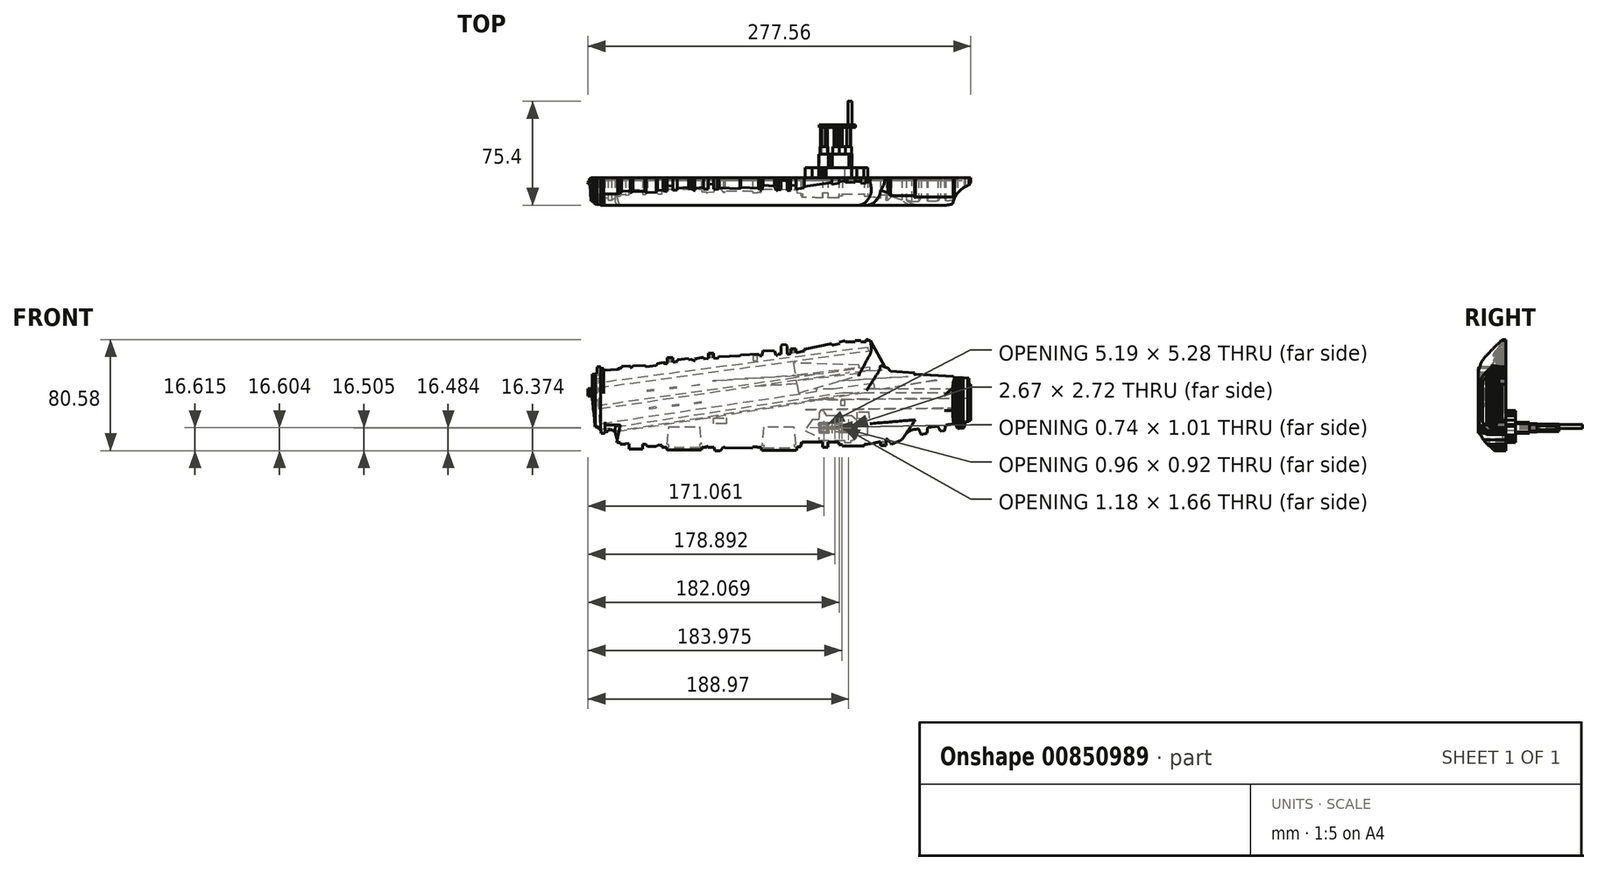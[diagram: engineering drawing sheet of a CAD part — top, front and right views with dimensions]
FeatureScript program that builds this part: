
annotation { "Feature Type Name" : "Feature", "Feature Type Description" : "" }
export const myFeature = defineFeature(function(context is Context, id is Id, definition is map)
    precondition{}
    {
        {
            var Q0;
            Q0=qCreatedBy(makeId("Front.planeOp"),FACE);
            var sketch = newSketch(context, id + "F0", { "sketchPlane" : qUnion([Q0])});
            skLineSegment(sketch, "E0", {"start": v(17.46, 94.58) * mm, "end": v(17.46, 84.08) * mm});
            skLineSegment(sketch, "E1", {"start": v(17.46, 84.08) * mm, "end": v(13.14, 84.08) * mm});
            skLineSegment(sketch, "E2", {"start": v(13.14, 84.08) * mm, "end": v(13.14, 78.8) * mm});
            skLineSegment(sketch, "E3", {"start": v(13.14, 78.8) * mm, "end": v(17.46, 78.8) * mm});
            skLineSegment(sketch, "E4", {"start": v(17.46, 78.8) * mm, "end": v(19.56, 56.5) * mm});
            skLineSegment(sketch, "E5", {"start": v(19.56, 56.5) * mm, "end": v(20.5, 56.3) * mm});
            skLineSegment(sketch, "E6", {"start": v(20.5, 56.3) * mm, "end": v(21.21, 56.3) * mm});
            skLineSegment(sketch, "E7", {"start": v(21.21, 56.3) * mm, "end": v(21.83, 57.14) * mm});
            skLineSegment(sketch, "E8", {"start": v(21.83, 57.14) * mm, "end": v(22.25, 54.43) * mm});
            skLineSegment(sketch, "E9", {"start": v(22.25, 54.43) * mm, "end": v(23.35, 54.6) * mm});
            skLineSegment(sketch, "E10", {"start": v(23.35, 54.6) * mm, "end": v(24.02, 54.26) * mm});
            skLineSegment(sketch, "E11", {"start": v(24.02, 54.26) * mm, "end": v(23.94, 51.57) * mm});
            skLineSegment(sketch, "E12", {"start": v(23.94, 51.57) * mm, "end": v(26.88, 51.57) * mm});
            skLineSegment(sketch, "E13", {"start": v(26.88, 51.57) * mm, "end": v(26.88, 53) * mm});
            skLineSegment(sketch, "E14", {"start": v(26.88, 53) * mm, "end": v(28.92, 53) * mm});
            skLineSegment(sketch, "E15", {"start": v(28.92, 53) * mm, "end": v(28.92, 54.15) * mm});
            skLineSegment(sketch, "E16", {"start": v(28.92, 54.15) * mm, "end": v(31.63, 54.21) * mm});
            skLineSegment(sketch, "E17", {"start": v(31.63, 54.21) * mm, "end": v(33.97, 52.9) * mm});
            skLineSegment(sketch, "E18", {"start": v(33.97, 52.9) * mm, "end": v(35.66, 46.84) * mm});
            skLineSegment(sketch, "E19", {"start": v(35.66, 46.84) * mm, "end": v(35.29, 45.02) * mm});
            skLineSegment(sketch, "E20", {"start": v(35.29, 45.02) * mm, "end": v(37.83, 45.02) * mm});
            skLineSegment(sketch, "E21", {"start": v(37.83, 45.02) * mm, "end": v(37.83, 43.82) * mm});
            skLineSegment(sketch, "E22", {"start": v(37.83, 43.82) * mm, "end": v(41.81, 43.7) * mm});
            skLineSegment(sketch, "E23", {"start": v(41.81, 43.7) * mm, "end": v(41.81, 44.43) * mm});
            skLineSegment(sketch, "E24", {"start": v(41.81, 44.43) * mm, "end": v(44.33, 44.18) * mm});
            skLineSegment(sketch, "E25", {"start": v(44.33, 44.18) * mm, "end": v(44.33, 40.16) * mm});
            skLineSegment(sketch, "E26", {"start": v(44.33, 40.16) * mm, "end": v(54.24, 40.16) * mm});
            skLineSegment(sketch, "E27", {"start": v(54.24, 40.16) * mm, "end": v(54.24, 43.75) * mm});
            skLineSegment(sketch, "E28", {"start": v(54.24, 43.75) * mm, "end": v(56.4, 43.75) * mm});
            skLineSegment(sketch, "E29", {"start": v(56.4, 43.75) * mm, "end": v(57.47, 42.08) * mm});
            skLineSegment(sketch, "E30", {"start": v(57.47, 42.08) * mm, "end": v(63.78, 42.08) * mm});
            skLineSegment(sketch, "E31", {"start": v(63.78, 42.08) * mm, "end": v(65.22, 43.15) * mm});
            skLineSegment(sketch, "E32", {"start": v(65.22, 43.15) * mm, "end": v(68.07, 43.15) * mm});
            skLineSegment(sketch, "E33", {"start": v(68.07, 43.15) * mm, "end": v(68.07, 41.42) * mm});
            skLineSegment(sketch, "E34", {"start": v(68.07, 41.42) * mm, "end": v(71.42, 41.42) * mm});
            skLineSegment(sketch, "E35", {"start": v(71.42, 41.42) * mm, "end": v(71.42, 39.98) * mm});
            skLineSegment(sketch, "E36", {"start": v(71.42, 39.98) * mm, "end": v(71.88, 39.65) * mm});
            skLineSegment(sketch, "E37", {"start": v(71.88, 39.65) * mm, "end": v(96.66, 39.72) * mm});
            skLineSegment(sketch, "E38", {"start": v(96.66, 39.72) * mm, "end": v(97.06, 40.28) * mm});
            skLineSegment(sketch, "E39", {"start": v(97.06, 40.28) * mm, "end": v(97.08, 41.63) * mm});
            skLineSegment(sketch, "E40", {"start": v(97.08, 41.63) * mm, "end": v(100.58, 41.58) * mm});
            skLineSegment(sketch, "E41", {"start": v(100.58, 41.58) * mm, "end": v(100.58, 42.76) * mm});
            skLineSegment(sketch, "E42", {"start": v(100.58, 42.76) * mm, "end": v(101.48, 41.63) * mm});
            skLineSegment(sketch, "E43", {"start": v(101.48, 41.63) * mm, "end": v(105.9, 41.55) * mm});
            skLineSegment(sketch, "E44", {"start": v(105.9, 41.55) * mm, "end": v(106.63, 39.13) * mm});
            skLineSegment(sketch, "E45", {"start": v(106.63, 39.13) * mm, "end": v(110.3, 39.13) * mm});
            skLineSegment(sketch, "E46", {"start": v(110.3, 39.13) * mm, "end": v(112.43, 41.6) * mm});
            skLineSegment(sketch, "E47", {"start": v(112.43, 41.6) * mm, "end": v(113.7, 41.6) * mm});
            skLineSegment(sketch, "E48", {"start": v(113.7, 41.6) * mm, "end": v(113.7, 41.14) * mm});
            skLineSegment(sketch, "E49", {"start": v(113.7, 41.14) * mm, "end": v(133.88, 41) * mm});
            skLineSegment(sketch, "E50", {"start": v(133.88, 41) * mm, "end": v(133.88, 41.77) * mm});
            skLineSegment(sketch, "E51", {"start": v(133.88, 41.77) * mm, "end": v(137.37, 41.75) * mm});
            skLineSegment(sketch, "E52", {"start": v(137.37, 41.75) * mm, "end": v(137.37, 41.45) * mm});
            skLineSegment(sketch, "E53", {"start": v(137.37, 41.45) * mm, "end": v(140.1, 41.43) * mm});
            skLineSegment(sketch, "E54", {"start": v(140.1, 41.43) * mm, "end": v(140.1, 39.91) * mm});
            skLineSegment(sketch, "E55", {"start": v(140.1, 39.91) * mm, "end": v(140.58, 39.34) * mm});
            skLineSegment(sketch, "E56", {"start": v(140.58, 39.34) * mm, "end": v(165.42, 39.34) * mm});
            skLineSegment(sketch, "E57", {"start": v(165.42, 39.34) * mm, "end": v(165.96, 39.92) * mm});
            skLineSegment(sketch, "E58", {"start": v(165.96, 39.92) * mm, "end": v(165.96, 41.75) * mm});
            skLineSegment(sketch, "E59", {"start": v(165.96, 41.75) * mm, "end": v(168.85, 41.9) * mm});
            skLineSegment(sketch, "E60", {"start": v(168.85, 41.9) * mm, "end": v(168.86, 43.4) * mm});
            skLineSegment(sketch, "E61", {"start": v(168.86, 43.4) * mm, "end": v(169.92, 45.23) * mm});
            skLineSegment(sketch, "E62", {"start": v(169.92, 45.23) * mm, "end": v(184.45, 45.23) * mm});
            skLineSegment(sketch, "E63", {"start": v(184.45, 45.23) * mm, "end": v(184.45, 41.6) * mm});
            skLineSegment(sketch, "E64", {"start": v(184.45, 41.6) * mm, "end": v(188.37, 41.56) * mm});
            skLineSegment(sketch, "E65", {"start": v(188.37, 41.56) * mm, "end": v(188.37, 45.38) * mm});
            skLineSegment(sketch, "E66", {"start": v(188.37, 45.38) * mm, "end": v(196.36, 45.38) * mm});
            skLineSegment(sketch, "E67", {"start": v(196.36, 45.38) * mm, "end": v(196.36, 43.58) * mm});
            skLineSegment(sketch, "E68", {"start": v(196.36, 43.58) * mm, "end": v(198.74, 43.56) * mm});
            skLineSegment(sketch, "E69", {"start": v(198.74, 43.56) * mm, "end": v(198.74, 42.38) * mm});
            skLineSegment(sketch, "E70", {"start": v(198.74, 42.38) * mm, "end": v(214.9, 42.38) * mm});
            skLineSegment(sketch, "E71", {"start": v(214.9, 42.38) * mm, "end": v(214.9, 43.75) * mm});
            skLineSegment(sketch, "E72", {"start": v(214.9, 43.75) * mm, "end": v(217.35, 43.73) * mm});
            skLineSegment(sketch, "E73", {"start": v(217.35, 43.73) * mm, "end": v(226.5, 45.59) * mm});
            skLineSegment(sketch, "E74", {"start": v(226.5, 45.59) * mm, "end": v(226.5, 42.93) * mm});
            skLineSegment(sketch, "E75", {"start": v(226.5, 42.93) * mm, "end": v(230.55, 42.93) * mm});
            skLineSegment(sketch, "E76", {"start": v(230.55, 42.93) * mm, "end": v(230.58, 47.27) * mm});
            skLineSegment(sketch, "E77", {"start": v(230.58, 47.27) * mm, "end": v(231.4, 47.6) * mm});
            skLineSegment(sketch, "E78", {"start": v(231.4, 47.6) * mm, "end": v(234.35, 43.8) * mm});
            skLineSegment(sketch, "E79", {"start": v(234.35, 43.8) * mm, "end": v(242.01, 46.9) * mm});
            skLineSegment(sketch, "E80", {"start": v(242.01, 46.9) * mm, "end": v(246.7, 53.94) * mm});
            skLineSegment(sketch, "E81", {"start": v(246.7, 53.94) * mm, "end": v(254.19, 54.94) * mm});
            skLineSegment(sketch, "E82", {"start": v(254.19, 54.94) * mm, "end": v(255.88, 50.81) * mm});
            skLineSegment(sketch, "E83", {"start": v(255.88, 50.81) * mm, "end": v(260.17, 51.58) * mm});
            skLineSegment(sketch, "E84", {"start": v(260.17, 51.58) * mm, "end": v(260.74, 56.02) * mm});
            skLineSegment(sketch, "E85", {"start": v(260.74, 56.02) * mm, "end": v(268.11, 56.83) * mm});
            skLineSegment(sketch, "E86", {"start": v(268.11, 56.83) * mm, "end": v(270.04, 53.3) * mm});
            skLineSegment(sketch, "E87", {"start": v(270.04, 53.3) * mm, "end": v(273, 53.67) * mm});
            skLineSegment(sketch, "E88", {"start": v(273, 53.67) * mm, "end": v(273.81, 57.7) * mm});
            skLineSegment(sketch, "E89", {"start": v(273.81, 57.7) * mm, "end": v(280.9, 58.7) * mm});
            skLineSegment(sketch, "E90", {"start": v(280.9, 58.7) * mm, "end": v(282.36, 55.14) * mm});
            skLineSegment(sketch, "E91", {"start": v(282.36, 55.14) * mm, "end": v(287.02, 55.7) * mm});
            skLineSegment(sketch, "E92", {"start": v(287.02, 55.7) * mm, "end": v(288, 59.97) * mm});
            skLineSegment(sketch, "E93", {"start": v(288, 59.97) * mm, "end": v(290.72, 60.26) * mm});
            skLineSegment(sketch, "E94", {"start": v(290.72, 60.26) * mm, "end": v(290.9, 60.95) * mm});
            skLineSegment(sketch, "E95", {"start": v(290.9, 60.95) * mm, "end": v(292, 60.94) * mm});
            skLineSegment(sketch, "E96", {"start": v(292, 60.94) * mm, "end": v(292, 87.32) * mm});
            skLineSegment(sketch, "E97", {"start": v(292, 87.32) * mm, "end": v(290.78, 87.33) * mm});
            skLineSegment(sketch, "E98", {"start": v(290.78, 87.33) * mm, "end": v(290.72, 91.74) * mm});
            skLineSegment(sketch, "E99", {"start": v(290.72, 91.74) * mm, "end": v(280.06, 92.14) * mm});
            skLineSegment(sketch, "E100", {"start": v(280.06, 92.14) * mm, "end": v(279.08, 92.88) * mm});
            skLineSegment(sketch, "E101", {"start": v(279.08, 92.88) * mm, "end": v(251.91, 94.68) * mm});
            skLineSegment(sketch, "E102", {"start": v(251.91, 94.68) * mm, "end": v(251.55, 94.22) * mm});
            skLineSegment(sketch, "E103", {"start": v(251.55, 94.22) * mm, "end": v(251.28, 94.44) * mm});
            skLineSegment(sketch, "E104", {"start": v(251.28, 94.44) * mm, "end": v(251.28, 95.53) * mm});
            skLineSegment(sketch, "E105", {"start": v(251.28, 95.53) * mm, "end": v(233.78, 96.7) * mm});
            skLineSegment(sketch, "E106", {"start": v(233.78, 96.7) * mm, "end": v(231.76, 99.17) * mm});
            skLineSegment(sketch, "E107", {"start": v(231.76, 99.17) * mm, "end": v(229.8, 99.83) * mm});
            skLineSegment(sketch, "E108", {"start": v(229.8, 99.83) * mm, "end": v(219.13, 119.12) * mm});
            skLineSegment(sketch, "E109", {"start": v(219.13, 119.12) * mm, "end": v(218.1, 118.56) * mm});
            skLineSegment(sketch, "E110", {"start": v(218.1, 118.56) * mm, "end": v(217.47, 119.7) * mm});
            skLineSegment(sketch, "E111", {"start": v(217.47, 119.7) * mm, "end": v(216.05, 119.7) * mm});
            skLineSegment(sketch, "E112", {"start": v(216.05, 119.7) * mm, "end": v(216.05, 117.93) * mm});
            skLineSegment(sketch, "E113", {"start": v(216.05, 117.93) * mm, "end": v(212.06, 117.95) * mm});
            skLineSegment(sketch, "E114", {"start": v(212.06, 117.95) * mm, "end": v(212.06, 119.12) * mm});
            skLineSegment(sketch, "E115", {"start": v(212.06, 119.12) * mm, "end": v(207.98, 119.15) * mm});
            skLineSegment(sketch, "E116", {"start": v(207.98, 119.15) * mm, "end": v(207.98, 117.97) * mm});
            skLineSegment(sketch, "E117", {"start": v(207.98, 117.97) * mm, "end": v(202.21, 117.97) * mm});
            skLineSegment(sketch, "E118", {"start": v(202.21, 117.97) * mm, "end": v(201.04, 117.66) * mm});
            skLineSegment(sketch, "E119", {"start": v(201.04, 117.66) * mm, "end": v(200.7, 118.91) * mm});
            skLineSegment(sketch, "E120", {"start": v(200.7, 118.91) * mm, "end": v(196.7, 117.85) * mm});
            skLineSegment(sketch, "E121", {"start": v(196.7, 117.85) * mm, "end": v(196.96, 116.88) * mm});
            skLineSegment(sketch, "E122", {"start": v(196.96, 116.88) * mm, "end": v(191.35, 115.66) * mm});
            skLineSegment(sketch, "E123", {"start": v(191.35, 115.66) * mm, "end": v(191.1, 116.78) * mm});
            skLineSegment(sketch, "E124", {"start": v(191.1, 116.78) * mm, "end": v(171.36, 112.66) * mm});
            skLineSegment(sketch, "E125", {"start": v(171.36, 112.66) * mm, "end": v(171.36, 111.56) * mm});
            skLineSegment(sketch, "E126", {"start": v(171.36, 111.56) * mm, "end": v(165.3, 110.2) * mm});
            skLineSegment(sketch, "E127", {"start": v(165.3, 110.2) * mm, "end": v(165.3, 113) * mm});
            skLineSegment(sketch, "E128", {"start": v(165.3, 113) * mm, "end": v(161.35, 113.04) * mm});
            skLineSegment(sketch, "E129", {"start": v(161.35, 113.04) * mm, "end": v(161.35, 109.4) * mm});
            skLineSegment(sketch, "E130", {"start": v(161.35, 109.4) * mm, "end": v(160.33, 109.04) * mm});
            skLineSegment(sketch, "E131", {"start": v(160.33, 109.04) * mm, "end": v(158.83, 109.05) * mm});
            skLineSegment(sketch, "E132", {"start": v(158.83, 109.05) * mm, "end": v(158.83, 114.8) * mm});
            skLineSegment(sketch, "E133", {"start": v(158.83, 114.8) * mm, "end": v(158.16, 116) * mm});
            skLineSegment(sketch, "E134", {"start": v(158.16, 116) * mm, "end": v(155.21, 116.02) * mm});
            skLineSegment(sketch, "E135", {"start": v(155.21, 116.02) * mm, "end": v(154.5, 114.8) * mm});
            skLineSegment(sketch, "E136", {"start": v(154.5, 114.8) * mm, "end": v(154.5, 109.29) * mm});
            skLineSegment(sketch, "E137", {"start": v(154.5, 109.29) * mm, "end": v(152.2, 109.17) * mm});
            skLineSegment(sketch, "E138", {"start": v(152.2, 109.17) * mm, "end": v(151.96, 108.28) * mm});
            skLineSegment(sketch, "E139", {"start": v(151.96, 108.28) * mm, "end": v(150.79, 108.3) * mm});
            skLineSegment(sketch, "E140", {"start": v(150.79, 108.3) * mm, "end": v(149.72, 111.51) * mm});
            skLineSegment(sketch, "E141", {"start": v(149.72, 111.51) * mm, "end": v(141.5, 111.57) * mm});
            skLineSegment(sketch, "E142", {"start": v(141.5, 111.57) * mm, "end": v(140.58, 107.83) * mm});
            skLineSegment(sketch, "E143", {"start": v(140.58, 107.83) * mm, "end": v(138.98, 107.84) * mm});
            skLineSegment(sketch, "E144", {"start": v(138.98, 107.84) * mm, "end": v(138.3, 109.06) * mm});
            skLineSegment(sketch, "E145", {"start": v(138.3, 109.06) * mm, "end": v(125.07, 108.65) * mm});
            skLineSegment(sketch, "E146", {"start": v(125.07, 108.65) * mm, "end": v(124.54, 107.84) * mm});
            skLineSegment(sketch, "E147", {"start": v(124.54, 107.84) * mm, "end": v(109.46, 107.3) * mm});
            skLineSegment(sketch, "E148", {"start": v(109.46, 107.3) * mm, "end": v(108.37, 106.06) * mm});
            skLineSegment(sketch, "E149", {"start": v(108.37, 106.06) * mm, "end": v(105.43, 106.25) * mm});
            skLineSegment(sketch, "E150", {"start": v(105.43, 106.25) * mm, "end": v(105.43, 109.69) * mm});
            skLineSegment(sketch, "E151", {"start": v(105.43, 109.69) * mm, "end": v(101.69, 109.69) * mm});
            skLineSegment(sketch, "E152", {"start": v(101.69, 109.69) * mm, "end": v(101.69, 106.06) * mm});
            skLineSegment(sketch, "E153", {"start": v(101.69, 106.06) * mm, "end": v(98.3, 105.58) * mm});
            skLineSegment(sketch, "E154", {"start": v(98.3, 105.58) * mm, "end": v(98.13, 106.82) * mm});
            skLineSegment(sketch, "E155", {"start": v(98.13, 106.82) * mm, "end": v(91.96, 105.8) * mm});
            skLineSegment(sketch, "E156", {"start": v(91.96, 105.8) * mm, "end": v(92.06, 104.38) * mm});
            skLineSegment(sketch, "E157", {"start": v(92.06, 104.38) * mm, "end": v(91.5, 104.34) * mm});
            skLineSegment(sketch, "E158", {"start": v(91.5, 104.34) * mm, "end": v(89.45, 105.28) * mm});
            skLineSegment(sketch, "E159", {"start": v(89.45, 105.28) * mm, "end": v(87.45, 105.03) * mm});
            skLineSegment(sketch, "E160", {"start": v(87.45, 105.03) * mm, "end": v(87.32, 106.06) * mm});
            skLineSegment(sketch, "E161", {"start": v(87.32, 106.06) * mm, "end": v(79.1, 104.92) * mm});
            skLineSegment(sketch, "E162", {"start": v(79.1, 104.92) * mm, "end": v(79.1, 103.75) * mm});
            skLineSegment(sketch, "E163", {"start": v(79.1, 103.75) * mm, "end": v(76, 103.25) * mm});
            skLineSegment(sketch, "E164", {"start": v(76, 103.25) * mm, "end": v(75.86, 106.5) * mm});
            skLineSegment(sketch, "E165", {"start": v(75.86, 106.5) * mm, "end": v(72.02, 106.53) * mm});
            skLineSegment(sketch, "E166", {"start": v(72.02, 106.53) * mm, "end": v(71.74, 102.31) * mm});
            skLineSegment(sketch, "E167", {"start": v(71.74, 102.31) * mm, "end": v(70.48, 102.21) * mm});
            skLineSegment(sketch, "E168", {"start": v(70.48, 102.21) * mm, "end": v(69.16, 103.07) * mm});
            skLineSegment(sketch, "E169", {"start": v(69.16, 103.07) * mm, "end": v(64.78, 102.32) * mm});
            skLineSegment(sketch, "E170", {"start": v(64.78, 102.32) * mm, "end": v(63.88, 100.91) * mm});
            skLineSegment(sketch, "E171", {"start": v(63.88, 100.91) * mm, "end": v(56.52, 100.1) * mm});
            skLineSegment(sketch, "E172", {"start": v(56.52, 100.1) * mm, "end": v(55.55, 101.04) * mm});
            skLineSegment(sketch, "E173", {"start": v(55.55, 101.04) * mm, "end": v(47.24, 100.47) * mm});
            skLineSegment(sketch, "E174", {"start": v(47.24, 100.47) * mm, "end": v(45.97, 99.37) * mm});
            skLineSegment(sketch, "E175", {"start": v(45.97, 99.37) * mm, "end": v(45.19, 99.37) * mm});
            skLineSegment(sketch, "E176", {"start": v(45.19, 99.37) * mm, "end": v(45.19, 100.47) * mm});
            skLineSegment(sketch, "E177", {"start": v(45.19, 100.47) * mm, "end": v(38.88, 100.3) * mm});
            skLineSegment(sketch, "E178", {"start": v(38.88, 100.3) * mm, "end": v(38.91, 98.97) * mm});
            skLineSegment(sketch, "E179", {"start": v(38.91, 98.97) * mm, "end": v(37.53, 98.98) * mm});
            skLineSegment(sketch, "E180", {"start": v(37.53, 98.98) * mm, "end": v(36.16, 97.95) * mm});
            skLineSegment(sketch, "E181", {"start": v(36.16, 97.95) * mm, "end": v(26, 97.3) * mm});
            skLineSegment(sketch, "E182", {"start": v(26, 97.3) * mm, "end": v(26, 98.56) * mm});
            skLineSegment(sketch, "E183", {"start": v(26, 98.56) * mm, "end": v(23.68, 98.72) * mm});
            skLineSegment(sketch, "E184", {"start": v(23.68, 98.72) * mm, "end": v(23.68, 99.83) * mm});
            skLineSegment(sketch, "E185", {"start": v(23.68, 99.83) * mm, "end": v(20.98, 100) * mm});
            skLineSegment(sketch, "E186", {"start": v(20.98, 100) * mm, "end": v(20.96, 95.8) * mm});
            skLineSegment(sketch, "E187", {"start": v(20.96, 95.8) * mm, "end": v(19.09, 94.58) * mm});
            skLineSegment(sketch, "E188", {"start": v(19.09, 94.58) * mm, "end": v(17.46, 94.58) * mm});
            skSolve(sketch);
        }
        {
            var Q0;
            Q0 = qSketchRegion(id + "F0", true);
            extrude(context, id + "F1", {"entities" : qUnion([Q0]), "oppositeDirection" : true, "depth" : 20 * mm, "offsetDistance" : 25 * mm});
        }
        {
            var Q0;
            Q0=qCreatedBy(makeId("Top.planeOp"),FACE);
            var sketch = newSketch(context, id + "F2", { "sketchPlane" : qUnion([Q0])});
            skLineSegment(sketch, "E189", {"start": v(17.01, 21.04) * mm, "end": v(17.01, 20.4) * mm});
            skLineSegment(sketch, "E190", {"start": v(17.01, 20.4) * mm, "end": v(16.02, 19.28) * mm});
            skLineSegment(sketch, "E191", {"start": v(16.02, 19.28) * mm, "end": v(15.49, 19.42) * mm});
            skLineSegment(sketch, "E192", {"start": v(15.49, 19.42) * mm, "end": v(15.49, 19.12) * mm});
            skLineSegment(sketch, "E193", {"start": v(15.49, 19.12) * mm, "end": v(18.13, 17.85) * mm});
            skLineSegment(sketch, "E194", {"start": v(18.13, 17.85) * mm, "end": v(18.47, 17.72) * mm});
            skLineSegment(sketch, "E195", {"start": v(18.47, 17.72) * mm, "end": v(18.47, 16.25) * mm});
            skLineSegment(sketch, "E196", {"start": v(18.47, 16.25) * mm, "end": v(16.5, 16.14) * mm});
            skLineSegment(sketch, "E197", {"start": v(16.5, 16.14) * mm, "end": v(16.5, 17.46) * mm});
            skLineSegment(sketch, "E198", {"start": v(16.5, 17.46) * mm, "end": v(16.43, 17.55) * mm});
            skLineSegment(sketch, "E199", {"start": v(16.43, 17.55) * mm, "end": v(16.28, 17.68) * mm});
            skLineSegment(sketch, "E200", {"start": v(16.28, 17.68) * mm, "end": v(16.2, 17.85) * mm});
            skLineSegment(sketch, "E201", {"start": v(16.2, 17.85) * mm, "end": v(16, 17.94) * mm});
            skLineSegment(sketch, "E202", {"start": v(16, 17.94) * mm, "end": v(15.9, 18.07) * mm});
            skLineSegment(sketch, "E203", {"start": v(15.9, 18.07) * mm, "end": v(15.6, 18.07) * mm});
            skLineSegment(sketch, "E204", {"start": v(15.6, 18.07) * mm, "end": v(15.24, 18.07) * mm});
            skLineSegment(sketch, "E205", {"start": v(15.24, 18.07) * mm, "end": v(15, 17.85) * mm});
            skLineSegment(sketch, "E206", {"start": v(15, 17.85) * mm, "end": v(14.79, 17.68) * mm});
            skLineSegment(sketch, "E207", {"start": v(14.79, 17.68) * mm, "end": v(14.62, 17.33) * mm});
            skLineSegment(sketch, "E208", {"start": v(14.62, 17.33) * mm, "end": v(14.54, 16.9) * mm});
            skLineSegment(sketch, "E209", {"start": v(14.54, 16.9) * mm, "end": v(14.63, 16.48) * mm});
            skLineSegment(sketch, "E210", {"start": v(14.63, 16.48) * mm, "end": v(14.7, 16.16) * mm});
            skLineSegment(sketch, "E211", {"start": v(14.7, 16.16) * mm, "end": v(14.45, 16.16) * mm});
            skLineSegment(sketch, "E212", {"start": v(14.45, 16.16) * mm, "end": v(14.45, 15.6) * mm});
            skLineSegment(sketch, "E213", {"start": v(14.45, 15.6) * mm, "end": v(15.23, 15.6) * mm});
            skLineSegment(sketch, "E214", {"start": v(15.23, 15.6) * mm, "end": v(15.23, 15.44) * mm});
            skLineSegment(sketch, "E215", {"start": v(15.23, 15.44) * mm, "end": v(15.74, 15.44) * mm});
            skLineSegment(sketch, "E216", {"start": v(15.74, 15.44) * mm, "end": v(15.74, 14.94) * mm});
            skLineSegment(sketch, "E217", {"start": v(15.74, 14.94) * mm, "end": v(15.95, 14.8) * mm});
            skLineSegment(sketch, "E218", {"start": v(15.95, 14.8) * mm, "end": v(16.5, 3.09) * mm});
            skLineSegment(sketch, "E219", {"start": v(16.5, 3.09) * mm, "end": v(17.59, 3.14) * mm});
            skLineSegment(sketch, "E220", {"start": v(17.59, 3.14) * mm, "end": v(17.47, 5.7) * mm});
            skLineSegment(sketch, "E221", {"start": v(17.47, 5.7) * mm, "end": v(18, 4.7) * mm});
            skLineSegment(sketch, "E222", {"start": v(18, 4.7) * mm, "end": v(18.13, 4.59) * mm});
            skLineSegment(sketch, "E223", {"start": v(18.13, 4.59) * mm, "end": v(18.28, 3.14) * mm});
            skLineSegment(sketch, "E224", {"start": v(18.28, 3.14) * mm, "end": v(18.38, 3.03) * mm});
            skLineSegment(sketch, "E225", {"start": v(18.38, 3.03) * mm, "end": v(18.47, 1.5) * mm});
            skLineSegment(sketch, "E226", {"start": v(18.47, 1.5) * mm, "end": v(19.06, 1.53) * mm});
            skLineSegment(sketch, "E227", {"start": v(19.06, 1.53) * mm, "end": v(19.65, 0.77) * mm});
            skLineSegment(sketch, "E228", {"start": v(19.65, 0.77) * mm, "end": v(23.67, 0.16) * mm});
            skLineSegment(sketch, "E229", {"start": v(23.67, 0.16) * mm, "end": v(23.67, -0.1) * mm});
            skLineSegment(sketch, "E230", {"start": v(23.67, -0.1) * mm, "end": v(11.26, -1.15) * mm});
            skLineSegment(sketch, "E231", {"start": v(11.26, -1.15) * mm, "end": v(11.26, 21.4) * mm});
            skLineSegment(sketch, "E232", {"start": v(11.26, 21.4) * mm, "end": v(17.01, 21.04) * mm});
            skLineSegment(sketch, "E233", {"start": v(294.55, 19.12) * mm, "end": v(291.95, 16.99) * mm});
            skLineSegment(sketch, "E234", {"start": v(291.95, 16.99) * mm, "end": v(291.7, 15.93) * mm});
            skLineSegment(sketch, "E235", {"start": v(291.7, 15.93) * mm, "end": v(291.1, 14.94) * mm});
            skLineSegment(sketch, "E236", {"start": v(291.1, 14.94) * mm, "end": v(289.71, 14.23) * mm});
            skLineSegment(sketch, "E237", {"start": v(289.71, 14.23) * mm, "end": v(286.46, 12.53) * mm});
            skLineSegment(sketch, "E238", {"start": v(286.46, 12.53) * mm, "end": v(284.52, 11.05) * mm});
            skLineSegment(sketch, "E239", {"start": v(284.52, 11.05) * mm, "end": v(283.26, 9.9) * mm});
            skLineSegment(sketch, "E240", {"start": v(283.26, 9.9) * mm, "end": v(281.72, 8.08) * mm});
            skLineSegment(sketch, "E241", {"start": v(281.72, 8.08) * mm, "end": v(280.52, 5.91) * mm});
            skLineSegment(sketch, "E242", {"start": v(280.52, 5.91) * mm, "end": v(279.38, 3.14) * mm});
            skLineSegment(sketch, "E243", {"start": v(279.38, 3.14) * mm, "end": v(278.8, 0.95) * mm});
            skLineSegment(sketch, "E244", {"start": v(278.8, 0.95) * mm, "end": v(278.9, -0.93) * mm});
            skLineSegment(sketch, "E245", {"start": v(278.9, -0.93) * mm, "end": v(293.76, -0.93) * mm});
            skLineSegment(sketch, "E246", {"start": v(293.76, -0.93) * mm, "end": v(295.93, 12.76) * mm});
            skLineSegment(sketch, "E247", {"start": v(295.93, 12.76) * mm, "end": v(294.55, 19.12) * mm});
            skSolve(sketch);
        }
        {
            var Q0;
            Q0 = qSketchRegion(id + "F2", true);
            extrude(context, id + "F3", {"entities" : qUnion([Q0]), "operationType" : NewBodyOperationType.REMOVE, "endBound" : BoundingType.THROUGH_ALL, "depth" : 25 * mm, "offsetDistance" : 25 * mm});
        }
        {
            var Q0;
            Q0=makeQuery(id+"F1.opExtrude","CAP_EDGE",EDGE,{"disambiguationData":[OSD([sQuery(id+"F0.wireOp",EDGE,"E49")])],"isStart":true});
            var Q1;
            Q1=makeQuery(id+"F1.opExtrude","CAP_EDGE",EDGE,{"disambiguationData":[OSD([sQuery(id+"F0.wireOp",EDGE,"E173")])],"isStart":true});
            chamfer(context, id + "F4", {"entities" : qUnion([Q0, Q1]), "width" : 10 * mm, "tangentPropagation" : true});
        }
        {
            var Q0;
            Q0=makeQuery(id+"F1.opExtrude","CAP_EDGE",EDGE,{"disambiguationData":[OSD([sQuery(id+"F0.wireOp",EDGE,"E101")])],"isStart":true});
            var Q1;
            Q1=makeQuery(id+"F1.opExtrude","CAP_EDGE",EDGE,{"disambiguationData":[OSD([sQuery(id+"F0.wireOp",EDGE,"E83")])],"isStart":true});
            var Q2;
            Q2=makeQuery(id+"F1.opExtrude","SWEPT_EDGE",EDGE,{"disambiguationData":[OSD([sQuery(id+"F0.wireOp",EDGE,"E80"),sQuery(id+"F0.wireOp",EDGE,"E81")])]});
            chamfer(context, id + "F5", {"entities" : qUnion([Q0, Q1, Q2]), "width" : 6 * mm, "tangentPropagation" : true});
        }
        {
            var Q0;
            Q0=makeQuery(id+"F1.opExtrude","CAP_EDGE",EDGE,{"disambiguationData":[OSD([sQuery(id+"F0.wireOp",EDGE,"E14")])],"isStart":true});
            chamfer(context, id + "F6", {"entities" : qUnion([Q0]), "width" : 5 * mm, "tangentPropagation" : true});
        }
        {
            var Q0;
            Q0=makeQuery(id+"F3.boolean.opBoolean","INTERSECT",EDGE,{"derivedFrom":[makeQuery(id+"F1.opExtrude","CAP_FACE",FACE,{"disambiguationData":[OSD([sQuery(id+"F0.wireOp",EDGE,"E0"),sQuery(id+"F0.wireOp",EDGE,"E1"),sQuery(id+"F0.wireOp",EDGE,"E2"),sQuery(id+"F0.wireOp",EDGE,"E3"),sQuery(id+"F0.wireOp",EDGE,"E4"),sQuery(id+"F0.wireOp",EDGE,"E5"),sQuery(id+"F0.wireOp",EDGE,"E6"),sQuery(id+"F0.wireOp",EDGE,"E7"),sQuery(id+"F0.wireOp",EDGE,"E8"),sQuery(id+"F0.wireOp",EDGE,"E9"),sQuery(id+"F0.wireOp",EDGE,"E10"),sQuery(id+"F0.wireOp",EDGE,"E11"),sQuery(id+"F0.wireOp",EDGE,"E12"),sQuery(id+"F0.wireOp",EDGE,"E13"),sQuery(id+"F0.wireOp",EDGE,"E14"),sQuery(id+"F0.wireOp",EDGE,"E15"),sQuery(id+"F0.wireOp",EDGE,"E16"),sQuery(id+"F0.wireOp",EDGE,"E17"),sQuery(id+"F0.wireOp",EDGE,"E18"),sQuery(id+"F0.wireOp",EDGE,"E19"),sQuery(id+"F0.wireOp",EDGE,"E20"),sQuery(id+"F0.wireOp",EDGE,"E21"),sQuery(id+"F0.wireOp",EDGE,"E22"),sQuery(id+"F0.wireOp",EDGE,"E23"),sQuery(id+"F0.wireOp",EDGE,"E24"),sQuery(id+"F0.wireOp",EDGE,"E25"),sQuery(id+"F0.wireOp",EDGE,"E26"),sQuery(id+"F0.wireOp",EDGE,"E27"),sQuery(id+"F0.wireOp",EDGE,"E28"),sQuery(id+"F0.wireOp",EDGE,"E29"),sQuery(id+"F0.wireOp",EDGE,"E30"),sQuery(id+"F0.wireOp",EDGE,"E31"),sQuery(id+"F0.wireOp",EDGE,"E32"),sQuery(id+"F0.wireOp",EDGE,"E33"),sQuery(id+"F0.wireOp",EDGE,"E34"),sQuery(id+"F0.wireOp",EDGE,"E35"),sQuery(id+"F0.wireOp",EDGE,"E36"),sQuery(id+"F0.wireOp",EDGE,"E37"),sQuery(id+"F0.wireOp",EDGE,"E38"),sQuery(id+"F0.wireOp",EDGE,"E39"),sQuery(id+"F0.wireOp",EDGE,"E40"),sQuery(id+"F0.wireOp",EDGE,"E41"),sQuery(id+"F0.wireOp",EDGE,"E42"),sQuery(id+"F0.wireOp",EDGE,"E43"),sQuery(id+"F0.wireOp",EDGE,"E44"),sQuery(id+"F0.wireOp",EDGE,"E45"),sQuery(id+"F0.wireOp",EDGE,"E46"),sQuery(id+"F0.wireOp",EDGE,"E47"),sQuery(id+"F0.wireOp",EDGE,"E48"),sQuery(id+"F0.wireOp",EDGE,"E49"),sQuery(id+"F0.wireOp",EDGE,"E50"),sQuery(id+"F0.wireOp",EDGE,"E51"),sQuery(id+"F0.wireOp",EDGE,"E52"),sQuery(id+"F0.wireOp",EDGE,"E53"),sQuery(id+"F0.wireOp",EDGE,"E54"),sQuery(id+"F0.wireOp",EDGE,"E55"),sQuery(id+"F0.wireOp",EDGE,"E56"),sQuery(id+"F0.wireOp",EDGE,"E57"),sQuery(id+"F0.wireOp",EDGE,"E58"),sQuery(id+"F0.wireOp",EDGE,"E59"),sQuery(id+"F0.wireOp",EDGE,"E60"),sQuery(id+"F0.wireOp",EDGE,"E61"),sQuery(id+"F0.wireOp",EDGE,"E62"),sQuery(id+"F0.wireOp",EDGE,"E63"),sQuery(id+"F0.wireOp",EDGE,"E64"),sQuery(id+"F0.wireOp",EDGE,"E65"),sQuery(id+"F0.wireOp",EDGE,"E66"),sQuery(id+"F0.wireOp",EDGE,"E67"),sQuery(id+"F0.wireOp",EDGE,"E68"),sQuery(id+"F0.wireOp",EDGE,"E69"),sQuery(id+"F0.wireOp",EDGE,"E70"),sQuery(id+"F0.wireOp",EDGE,"E71"),sQuery(id+"F0.wireOp",EDGE,"E72"),sQuery(id+"F0.wireOp",EDGE,"E73"),sQuery(id+"F0.wireOp",EDGE,"E74"),sQuery(id+"F0.wireOp",EDGE,"E75"),sQuery(id+"F0.wireOp",EDGE,"E76"),sQuery(id+"F0.wireOp",EDGE,"E77"),sQuery(id+"F0.wireOp",EDGE,"E78"),sQuery(id+"F0.wireOp",EDGE,"E79"),sQuery(id+"F0.wireOp",EDGE,"E80"),sQuery(id+"F0.wireOp",EDGE,"E81"),sQuery(id+"F0.wireOp",EDGE,"E82"),sQuery(id+"F0.wireOp",EDGE,"E83"),sQuery(id+"F0.wireOp",EDGE,"E84"),sQuery(id+"F0.wireOp",EDGE,"E85"),sQuery(id+"F0.wireOp",EDGE,"E86"),sQuery(id+"F0.wireOp",EDGE,"E87"),sQuery(id+"F0.wireOp",EDGE,"E88"),sQuery(id+"F0.wireOp",EDGE,"E89"),sQuery(id+"F0.wireOp",EDGE,"E90"),sQuery(id+"F0.wireOp",EDGE,"E91"),sQuery(id+"F0.wireOp",EDGE,"E92"),sQuery(id+"F0.wireOp",EDGE,"E93"),sQuery(id+"F0.wireOp",EDGE,"E94"),sQuery(id+"F0.wireOp",EDGE,"E95"),sQuery(id+"F0.wireOp",EDGE,"E96"),sQuery(id+"F0.wireOp",EDGE,"E97"),sQuery(id+"F0.wireOp",EDGE,"E98"),sQuery(id+"F0.wireOp",EDGE,"E99"),sQuery(id+"F0.wireOp",EDGE,"E100"),sQuery(id+"F0.wireOp",EDGE,"E101"),sQuery(id+"F0.wireOp",EDGE,"E102"),sQuery(id+"F0.wireOp",EDGE,"E103"),sQuery(id+"F0.wireOp",EDGE,"E104"),sQuery(id+"F0.wireOp",EDGE,"E105"),sQuery(id+"F0.wireOp",EDGE,"E106"),sQuery(id+"F0.wireOp",EDGE,"E107"),sQuery(id+"F0.wireOp",EDGE,"E108"),sQuery(id+"F0.wireOp",EDGE,"E109"),sQuery(id+"F0.wireOp",EDGE,"E110"),sQuery(id+"F0.wireOp",EDGE,"E111"),sQuery(id+"F0.wireOp",EDGE,"E112"),sQuery(id+"F0.wireOp",EDGE,"E113"),sQuery(id+"F0.wireOp",EDGE,"E114"),sQuery(id+"F0.wireOp",EDGE,"E115"),sQuery(id+"F0.wireOp",EDGE,"E116"),sQuery(id+"F0.wireOp",EDGE,"E117"),sQuery(id+"F0.wireOp",EDGE,"E118"),sQuery(id+"F0.wireOp",EDGE,"E119"),sQuery(id+"F0.wireOp",EDGE,"E120"),sQuery(id+"F0.wireOp",EDGE,"E121"),sQuery(id+"F0.wireOp",EDGE,"E122"),sQuery(id+"F0.wireOp",EDGE,"E123"),sQuery(id+"F0.wireOp",EDGE,"E124"),sQuery(id+"F0.wireOp",EDGE,"E125"),sQuery(id+"F0.wireOp",EDGE,"E126"),sQuery(id+"F0.wireOp",EDGE,"E127"),sQuery(id+"F0.wireOp",EDGE,"E128"),sQuery(id+"F0.wireOp",EDGE,"E129"),sQuery(id+"F0.wireOp",EDGE,"E130"),sQuery(id+"F0.wireOp",EDGE,"E131"),sQuery(id+"F0.wireOp",EDGE,"E132"),sQuery(id+"F0.wireOp",EDGE,"E133"),sQuery(id+"F0.wireOp",EDGE,"E134"),sQuery(id+"F0.wireOp",EDGE,"E135"),sQuery(id+"F0.wireOp",EDGE,"E136"),sQuery(id+"F0.wireOp",EDGE,"E137"),sQuery(id+"F0.wireOp",EDGE,"E138"),sQuery(id+"F0.wireOp",EDGE,"E139"),sQuery(id+"F0.wireOp",EDGE,"E140"),sQuery(id+"F0.wireOp",EDGE,"E141"),sQuery(id+"F0.wireOp",EDGE,"E142"),sQuery(id+"F0.wireOp",EDGE,"E143"),sQuery(id+"F0.wireOp",EDGE,"E144"),sQuery(id+"F0.wireOp",EDGE,"E145"),sQuery(id+"F0.wireOp",EDGE,"E146"),sQuery(id+"F0.wireOp",EDGE,"E147"),sQuery(id+"F0.wireOp",EDGE,"E148"),sQuery(id+"F0.wireOp",EDGE,"E149"),sQuery(id+"F0.wireOp",EDGE,"E150"),sQuery(id+"F0.wireOp",EDGE,"E151"),sQuery(id+"F0.wireOp",EDGE,"E152"),sQuery(id+"F0.wireOp",EDGE,"E153"),sQuery(id+"F0.wireOp",EDGE,"E154"),sQuery(id+"F0.wireOp",EDGE,"E155"),sQuery(id+"F0.wireOp",EDGE,"E156"),sQuery(id+"F0.wireOp",EDGE,"E157"),sQuery(id+"F0.wireOp",EDGE,"E158"),sQuery(id+"F0.wireOp",EDGE,"E159"),sQuery(id+"F0.wireOp",EDGE,"E160"),sQuery(id+"F0.wireOp",EDGE,"E161"),sQuery(id+"F0.wireOp",EDGE,"E162"),sQuery(id+"F0.wireOp",EDGE,"E163"),sQuery(id+"F0.wireOp",EDGE,"E164"),sQuery(id+"F0.wireOp",EDGE,"E165"),sQuery(id+"F0.wireOp",EDGE,"E166"),sQuery(id+"F0.wireOp",EDGE,"E167"),sQuery(id+"F0.wireOp",EDGE,"E168"),sQuery(id+"F0.wireOp",EDGE,"E169"),sQuery(id+"F0.wireOp",EDGE,"E170"),sQuery(id+"F0.wireOp",EDGE,"E171"),sQuery(id+"F0.wireOp",EDGE,"E172"),sQuery(id+"F0.wireOp",EDGE,"E173"),sQuery(id+"F0.wireOp",EDGE,"E174"),sQuery(id+"F0.wireOp",EDGE,"E175"),sQuery(id+"F0.wireOp",EDGE,"E176"),sQuery(id+"F0.wireOp",EDGE,"E177"),sQuery(id+"F0.wireOp",EDGE,"E178"),sQuery(id+"F0.wireOp",EDGE,"E179"),sQuery(id+"F0.wireOp",EDGE,"E180"),sQuery(id+"F0.wireOp",EDGE,"E181"),sQuery(id+"F0.wireOp",EDGE,"E182"),sQuery(id+"F0.wireOp",EDGE,"E183"),sQuery(id+"F0.wireOp",EDGE,"E184"),sQuery(id+"F0.wireOp",EDGE,"E185"),sQuery(id+"F0.wireOp",EDGE,"E186"),sQuery(id+"F0.wireOp",EDGE,"E187"),sQuery(id+"F0.wireOp",EDGE,"E188")])],"isStart":true}),makeQuery(id+"F3.opExtrude","SWEPT_FACE",FACE,{"disambiguationData":[OSD([sQuery(id+"F2.wireOp",EDGE,"E244")])]})]});
            fillet(context, id + "F7", {"entities" : qUnion([Q0]), "radius" : 20 * mm, "tangentPropagation" : true, "allowEdgeOverflow" : false});
        }
        {
            var Q0;
            {var subQ0=sQuery(id+"F0.wireOp",EDGE,"E49");Q0=makeQuery(id+"F4.opChamfer","BLEND_EDGE",EDGE,{"blendedFrom":[makeQuery(id+"F1.opExtrude","CAP_EDGE",EDGE,{"disambiguationData":[OSD([subQ0])],"isStart":true}),makeQuery(id+"F1.opExtrude","CAP_FACE",FACE,{"disambiguationData":[OSD([sQuery(id+"F0.wireOp",EDGE,"E0"),sQuery(id+"F0.wireOp",EDGE,"E1"),sQuery(id+"F0.wireOp",EDGE,"E2"),sQuery(id+"F0.wireOp",EDGE,"E3"),sQuery(id+"F0.wireOp",EDGE,"E4"),sQuery(id+"F0.wireOp",EDGE,"E5"),sQuery(id+"F0.wireOp",EDGE,"E6"),sQuery(id+"F0.wireOp",EDGE,"E7"),sQuery(id+"F0.wireOp",EDGE,"E8"),sQuery(id+"F0.wireOp",EDGE,"E9"),sQuery(id+"F0.wireOp",EDGE,"E10"),sQuery(id+"F0.wireOp",EDGE,"E11"),sQuery(id+"F0.wireOp",EDGE,"E12"),sQuery(id+"F0.wireOp",EDGE,"E13"),sQuery(id+"F0.wireOp",EDGE,"E14"),sQuery(id+"F0.wireOp",EDGE,"E15"),sQuery(id+"F0.wireOp",EDGE,"E16"),sQuery(id+"F0.wireOp",EDGE,"E17"),sQuery(id+"F0.wireOp",EDGE,"E18"),sQuery(id+"F0.wireOp",EDGE,"E19"),sQuery(id+"F0.wireOp",EDGE,"E20"),sQuery(id+"F0.wireOp",EDGE,"E21"),sQuery(id+"F0.wireOp",EDGE,"E22"),sQuery(id+"F0.wireOp",EDGE,"E23"),sQuery(id+"F0.wireOp",EDGE,"E24"),sQuery(id+"F0.wireOp",EDGE,"E25"),sQuery(id+"F0.wireOp",EDGE,"E26"),sQuery(id+"F0.wireOp",EDGE,"E27"),sQuery(id+"F0.wireOp",EDGE,"E28"),sQuery(id+"F0.wireOp",EDGE,"E29"),sQuery(id+"F0.wireOp",EDGE,"E30"),sQuery(id+"F0.wireOp",EDGE,"E31"),sQuery(id+"F0.wireOp",EDGE,"E32"),sQuery(id+"F0.wireOp",EDGE,"E33"),sQuery(id+"F0.wireOp",EDGE,"E34"),sQuery(id+"F0.wireOp",EDGE,"E35"),sQuery(id+"F0.wireOp",EDGE,"E36"),sQuery(id+"F0.wireOp",EDGE,"E37"),sQuery(id+"F0.wireOp",EDGE,"E38"),sQuery(id+"F0.wireOp",EDGE,"E39"),sQuery(id+"F0.wireOp",EDGE,"E40"),sQuery(id+"F0.wireOp",EDGE,"E41"),sQuery(id+"F0.wireOp",EDGE,"E42"),sQuery(id+"F0.wireOp",EDGE,"E43"),sQuery(id+"F0.wireOp",EDGE,"E44"),sQuery(id+"F0.wireOp",EDGE,"E45"),sQuery(id+"F0.wireOp",EDGE,"E46"),sQuery(id+"F0.wireOp",EDGE,"E47"),sQuery(id+"F0.wireOp",EDGE,"E48"),subQ0,sQuery(id+"F0.wireOp",EDGE,"E50"),sQuery(id+"F0.wireOp",EDGE,"E51"),sQuery(id+"F0.wireOp",EDGE,"E52"),sQuery(id+"F0.wireOp",EDGE,"E53"),sQuery(id+"F0.wireOp",EDGE,"E54"),sQuery(id+"F0.wireOp",EDGE,"E55"),sQuery(id+"F0.wireOp",EDGE,"E56"),sQuery(id+"F0.wireOp",EDGE,"E57"),sQuery(id+"F0.wireOp",EDGE,"E58"),sQuery(id+"F0.wireOp",EDGE,"E59"),sQuery(id+"F0.wireOp",EDGE,"E60"),sQuery(id+"F0.wireOp",EDGE,"E61"),sQuery(id+"F0.wireOp",EDGE,"E62"),sQuery(id+"F0.wireOp",EDGE,"E63"),sQuery(id+"F0.wireOp",EDGE,"E64"),sQuery(id+"F0.wireOp",EDGE,"E65"),sQuery(id+"F0.wireOp",EDGE,"E66"),sQuery(id+"F0.wireOp",EDGE,"E67"),sQuery(id+"F0.wireOp",EDGE,"E68"),sQuery(id+"F0.wireOp",EDGE,"E69"),sQuery(id+"F0.wireOp",EDGE,"E70"),sQuery(id+"F0.wireOp",EDGE,"E71"),sQuery(id+"F0.wireOp",EDGE,"E72"),sQuery(id+"F0.wireOp",EDGE,"E73"),sQuery(id+"F0.wireOp",EDGE,"E74"),sQuery(id+"F0.wireOp",EDGE,"E75"),sQuery(id+"F0.wireOp",EDGE,"E76"),sQuery(id+"F0.wireOp",EDGE,"E77"),sQuery(id+"F0.wireOp",EDGE,"E78"),sQuery(id+"F0.wireOp",EDGE,"E79"),sQuery(id+"F0.wireOp",EDGE,"E80"),sQuery(id+"F0.wireOp",EDGE,"E81"),sQuery(id+"F0.wireOp",EDGE,"E82"),sQuery(id+"F0.wireOp",EDGE,"E83"),sQuery(id+"F0.wireOp",EDGE,"E84"),sQuery(id+"F0.wireOp",EDGE,"E85"),sQuery(id+"F0.wireOp",EDGE,"E86"),sQuery(id+"F0.wireOp",EDGE,"E87"),sQuery(id+"F0.wireOp",EDGE,"E88"),sQuery(id+"F0.wireOp",EDGE,"E89"),sQuery(id+"F0.wireOp",EDGE,"E90"),sQuery(id+"F0.wireOp",EDGE,"E91"),sQuery(id+"F0.wireOp",EDGE,"E92"),sQuery(id+"F0.wireOp",EDGE,"E93"),sQuery(id+"F0.wireOp",EDGE,"E94"),sQuery(id+"F0.wireOp",EDGE,"E95"),sQuery(id+"F0.wireOp",EDGE,"E96"),sQuery(id+"F0.wireOp",EDGE,"E97"),sQuery(id+"F0.wireOp",EDGE,"E98"),sQuery(id+"F0.wireOp",EDGE,"E99"),sQuery(id+"F0.wireOp",EDGE,"E100"),sQuery(id+"F0.wireOp",EDGE,"E101"),sQuery(id+"F0.wireOp",EDGE,"E102"),sQuery(id+"F0.wireOp",EDGE,"E103"),sQuery(id+"F0.wireOp",EDGE,"E104"),sQuery(id+"F0.wireOp",EDGE,"E105"),sQuery(id+"F0.wireOp",EDGE,"E106"),sQuery(id+"F0.wireOp",EDGE,"E107"),sQuery(id+"F0.wireOp",EDGE,"E108"),sQuery(id+"F0.wireOp",EDGE,"E109"),sQuery(id+"F0.wireOp",EDGE,"E110"),sQuery(id+"F0.wireOp",EDGE,"E111"),sQuery(id+"F0.wireOp",EDGE,"E112"),sQuery(id+"F0.wireOp",EDGE,"E113"),sQuery(id+"F0.wireOp",EDGE,"E114"),sQuery(id+"F0.wireOp",EDGE,"E115"),sQuery(id+"F0.wireOp",EDGE,"E116"),sQuery(id+"F0.wireOp",EDGE,"E117"),sQuery(id+"F0.wireOp",EDGE,"E118"),sQuery(id+"F0.wireOp",EDGE,"E119"),sQuery(id+"F0.wireOp",EDGE,"E120"),sQuery(id+"F0.wireOp",EDGE,"E121"),sQuery(id+"F0.wireOp",EDGE,"E122"),sQuery(id+"F0.wireOp",EDGE,"E123"),sQuery(id+"F0.wireOp",EDGE,"E124"),sQuery(id+"F0.wireOp",EDGE,"E125"),sQuery(id+"F0.wireOp",EDGE,"E126"),sQuery(id+"F0.wireOp",EDGE,"E127"),sQuery(id+"F0.wireOp",EDGE,"E128"),sQuery(id+"F0.wireOp",EDGE,"E129"),sQuery(id+"F0.wireOp",EDGE,"E130"),sQuery(id+"F0.wireOp",EDGE,"E131"),sQuery(id+"F0.wireOp",EDGE,"E132"),sQuery(id+"F0.wireOp",EDGE,"E133"),sQuery(id+"F0.wireOp",EDGE,"E134"),sQuery(id+"F0.wireOp",EDGE,"E135"),sQuery(id+"F0.wireOp",EDGE,"E136"),sQuery(id+"F0.wireOp",EDGE,"E137"),sQuery(id+"F0.wireOp",EDGE,"E138"),sQuery(id+"F0.wireOp",EDGE,"E139"),sQuery(id+"F0.wireOp",EDGE,"E140"),sQuery(id+"F0.wireOp",EDGE,"E141"),sQuery(id+"F0.wireOp",EDGE,"E142"),sQuery(id+"F0.wireOp",EDGE,"E143"),sQuery(id+"F0.wireOp",EDGE,"E144"),sQuery(id+"F0.wireOp",EDGE,"E145"),sQuery(id+"F0.wireOp",EDGE,"E146"),sQuery(id+"F0.wireOp",EDGE,"E147"),sQuery(id+"F0.wireOp",EDGE,"E148"),sQuery(id+"F0.wireOp",EDGE,"E149"),sQuery(id+"F0.wireOp",EDGE,"E150"),sQuery(id+"F0.wireOp",EDGE,"E151"),sQuery(id+"F0.wireOp",EDGE,"E152"),sQuery(id+"F0.wireOp",EDGE,"E153"),sQuery(id+"F0.wireOp",EDGE,"E154"),sQuery(id+"F0.wireOp",EDGE,"E155"),sQuery(id+"F0.wireOp",EDGE,"E156"),sQuery(id+"F0.wireOp",EDGE,"E157"),sQuery(id+"F0.wireOp",EDGE,"E158"),sQuery(id+"F0.wireOp",EDGE,"E159"),sQuery(id+"F0.wireOp",EDGE,"E160"),sQuery(id+"F0.wireOp",EDGE,"E161"),sQuery(id+"F0.wireOp",EDGE,"E162"),sQuery(id+"F0.wireOp",EDGE,"E163"),sQuery(id+"F0.wireOp",EDGE,"E164"),sQuery(id+"F0.wireOp",EDGE,"E165"),sQuery(id+"F0.wireOp",EDGE,"E166"),sQuery(id+"F0.wireOp",EDGE,"E167"),sQuery(id+"F0.wireOp",EDGE,"E168"),sQuery(id+"F0.wireOp",EDGE,"E169"),sQuery(id+"F0.wireOp",EDGE,"E170"),sQuery(id+"F0.wireOp",EDGE,"E171"),sQuery(id+"F0.wireOp",EDGE,"E172"),sQuery(id+"F0.wireOp",EDGE,"E173"),sQuery(id+"F0.wireOp",EDGE,"E174"),sQuery(id+"F0.wireOp",EDGE,"E175"),sQuery(id+"F0.wireOp",EDGE,"E176"),sQuery(id+"F0.wireOp",EDGE,"E177"),sQuery(id+"F0.wireOp",EDGE,"E178"),sQuery(id+"F0.wireOp",EDGE,"E179"),sQuery(id+"F0.wireOp",EDGE,"E180"),sQuery(id+"F0.wireOp",EDGE,"E181"),sQuery(id+"F0.wireOp",EDGE,"E182"),sQuery(id+"F0.wireOp",EDGE,"E183"),sQuery(id+"F0.wireOp",EDGE,"E184"),sQuery(id+"F0.wireOp",EDGE,"E185"),sQuery(id+"F0.wireOp",EDGE,"E186"),sQuery(id+"F0.wireOp",EDGE,"E187"),sQuery(id+"F0.wireOp",EDGE,"E188")])],"isStart":true})],"blendedInto":[makeQuery(id+"F1.opExtrude","CAP_FACE",FACE,{"disambiguationData":[OSD([sQuery(id+"F0.wireOp",EDGE,"E0"),sQuery(id+"F0.wireOp",EDGE,"E1"),sQuery(id+"F0.wireOp",EDGE,"E2"),sQuery(id+"F0.wireOp",EDGE,"E3"),sQuery(id+"F0.wireOp",EDGE,"E4"),sQuery(id+"F0.wireOp",EDGE,"E5"),sQuery(id+"F0.wireOp",EDGE,"E6"),sQuery(id+"F0.wireOp",EDGE,"E7"),sQuery(id+"F0.wireOp",EDGE,"E8"),sQuery(id+"F0.wireOp",EDGE,"E9"),sQuery(id+"F0.wireOp",EDGE,"E10"),sQuery(id+"F0.wireOp",EDGE,"E11"),sQuery(id+"F0.wireOp",EDGE,"E12"),sQuery(id+"F0.wireOp",EDGE,"E13"),sQuery(id+"F0.wireOp",EDGE,"E14"),sQuery(id+"F0.wireOp",EDGE,"E15"),sQuery(id+"F0.wireOp",EDGE,"E16"),sQuery(id+"F0.wireOp",EDGE,"E17"),sQuery(id+"F0.wireOp",EDGE,"E18"),sQuery(id+"F0.wireOp",EDGE,"E19"),sQuery(id+"F0.wireOp",EDGE,"E20"),sQuery(id+"F0.wireOp",EDGE,"E21"),sQuery(id+"F0.wireOp",EDGE,"E22"),sQuery(id+"F0.wireOp",EDGE,"E23"),sQuery(id+"F0.wireOp",EDGE,"E24"),sQuery(id+"F0.wireOp",EDGE,"E25"),sQuery(id+"F0.wireOp",EDGE,"E26"),sQuery(id+"F0.wireOp",EDGE,"E27"),sQuery(id+"F0.wireOp",EDGE,"E28"),sQuery(id+"F0.wireOp",EDGE,"E29"),sQuery(id+"F0.wireOp",EDGE,"E30"),sQuery(id+"F0.wireOp",EDGE,"E31"),sQuery(id+"F0.wireOp",EDGE,"E32"),sQuery(id+"F0.wireOp",EDGE,"E33"),sQuery(id+"F0.wireOp",EDGE,"E34"),sQuery(id+"F0.wireOp",EDGE,"E35"),sQuery(id+"F0.wireOp",EDGE,"E36"),sQuery(id+"F0.wireOp",EDGE,"E37"),sQuery(id+"F0.wireOp",EDGE,"E38"),sQuery(id+"F0.wireOp",EDGE,"E39"),sQuery(id+"F0.wireOp",EDGE,"E40"),sQuery(id+"F0.wireOp",EDGE,"E41"),sQuery(id+"F0.wireOp",EDGE,"E42"),sQuery(id+"F0.wireOp",EDGE,"E43"),sQuery(id+"F0.wireOp",EDGE,"E44"),sQuery(id+"F0.wireOp",EDGE,"E45"),sQuery(id+"F0.wireOp",EDGE,"E46"),sQuery(id+"F0.wireOp",EDGE,"E47"),sQuery(id+"F0.wireOp",EDGE,"E48"),subQ0,sQuery(id+"F0.wireOp",EDGE,"E50"),sQuery(id+"F0.wireOp",EDGE,"E51"),sQuery(id+"F0.wireOp",EDGE,"E52"),sQuery(id+"F0.wireOp",EDGE,"E53"),sQuery(id+"F0.wireOp",EDGE,"E54"),sQuery(id+"F0.wireOp",EDGE,"E55"),sQuery(id+"F0.wireOp",EDGE,"E56"),sQuery(id+"F0.wireOp",EDGE,"E57"),sQuery(id+"F0.wireOp",EDGE,"E58"),sQuery(id+"F0.wireOp",EDGE,"E59"),sQuery(id+"F0.wireOp",EDGE,"E60"),sQuery(id+"F0.wireOp",EDGE,"E61"),sQuery(id+"F0.wireOp",EDGE,"E62"),sQuery(id+"F0.wireOp",EDGE,"E63"),sQuery(id+"F0.wireOp",EDGE,"E64"),sQuery(id+"F0.wireOp",EDGE,"E65"),sQuery(id+"F0.wireOp",EDGE,"E66"),sQuery(id+"F0.wireOp",EDGE,"E67"),sQuery(id+"F0.wireOp",EDGE,"E68"),sQuery(id+"F0.wireOp",EDGE,"E69"),sQuery(id+"F0.wireOp",EDGE,"E70"),sQuery(id+"F0.wireOp",EDGE,"E71"),sQuery(id+"F0.wireOp",EDGE,"E72"),sQuery(id+"F0.wireOp",EDGE,"E73"),sQuery(id+"F0.wireOp",EDGE,"E74"),sQuery(id+"F0.wireOp",EDGE,"E75"),sQuery(id+"F0.wireOp",EDGE,"E76"),sQuery(id+"F0.wireOp",EDGE,"E77"),sQuery(id+"F0.wireOp",EDGE,"E78"),sQuery(id+"F0.wireOp",EDGE,"E79"),sQuery(id+"F0.wireOp",EDGE,"E80"),sQuery(id+"F0.wireOp",EDGE,"E81"),sQuery(id+"F0.wireOp",EDGE,"E82"),sQuery(id+"F0.wireOp",EDGE,"E83"),sQuery(id+"F0.wireOp",EDGE,"E84"),sQuery(id+"F0.wireOp",EDGE,"E85"),sQuery(id+"F0.wireOp",EDGE,"E86"),sQuery(id+"F0.wireOp",EDGE,"E87"),sQuery(id+"F0.wireOp",EDGE,"E88"),sQuery(id+"F0.wireOp",EDGE,"E89"),sQuery(id+"F0.wireOp",EDGE,"E90"),sQuery(id+"F0.wireOp",EDGE,"E91"),sQuery(id+"F0.wireOp",EDGE,"E92"),sQuery(id+"F0.wireOp",EDGE,"E93"),sQuery(id+"F0.wireOp",EDGE,"E94"),sQuery(id+"F0.wireOp",EDGE,"E95"),sQuery(id+"F0.wireOp",EDGE,"E96"),sQuery(id+"F0.wireOp",EDGE,"E97"),sQuery(id+"F0.wireOp",EDGE,"E98"),sQuery(id+"F0.wireOp",EDGE,"E99"),sQuery(id+"F0.wireOp",EDGE,"E100"),sQuery(id+"F0.wireOp",EDGE,"E101"),sQuery(id+"F0.wireOp",EDGE,"E102"),sQuery(id+"F0.wireOp",EDGE,"E103"),sQuery(id+"F0.wireOp",EDGE,"E104"),sQuery(id+"F0.wireOp",EDGE,"E105"),sQuery(id+"F0.wireOp",EDGE,"E106"),sQuery(id+"F0.wireOp",EDGE,"E107"),sQuery(id+"F0.wireOp",EDGE,"E108"),sQuery(id+"F0.wireOp",EDGE,"E109"),sQuery(id+"F0.wireOp",EDGE,"E110"),sQuery(id+"F0.wireOp",EDGE,"E111"),sQuery(id+"F0.wireOp",EDGE,"E112"),sQuery(id+"F0.wireOp",EDGE,"E113"),sQuery(id+"F0.wireOp",EDGE,"E114"),sQuery(id+"F0.wireOp",EDGE,"E115"),sQuery(id+"F0.wireOp",EDGE,"E116"),sQuery(id+"F0.wireOp",EDGE,"E117"),sQuery(id+"F0.wireOp",EDGE,"E118"),sQuery(id+"F0.wireOp",EDGE,"E119"),sQuery(id+"F0.wireOp",EDGE,"E120"),sQuery(id+"F0.wireOp",EDGE,"E121"),sQuery(id+"F0.wireOp",EDGE,"E122"),sQuery(id+"F0.wireOp",EDGE,"E123"),sQuery(id+"F0.wireOp",EDGE,"E124"),sQuery(id+"F0.wireOp",EDGE,"E125"),sQuery(id+"F0.wireOp",EDGE,"E126"),sQuery(id+"F0.wireOp",EDGE,"E127"),sQuery(id+"F0.wireOp",EDGE,"E128"),sQuery(id+"F0.wireOp",EDGE,"E129"),sQuery(id+"F0.wireOp",EDGE,"E130"),sQuery(id+"F0.wireOp",EDGE,"E131"),sQuery(id+"F0.wireOp",EDGE,"E132"),sQuery(id+"F0.wireOp",EDGE,"E133"),sQuery(id+"F0.wireOp",EDGE,"E134"),sQuery(id+"F0.wireOp",EDGE,"E135"),sQuery(id+"F0.wireOp",EDGE,"E136"),sQuery(id+"F0.wireOp",EDGE,"E137"),sQuery(id+"F0.wireOp",EDGE,"E138"),sQuery(id+"F0.wireOp",EDGE,"E139"),sQuery(id+"F0.wireOp",EDGE,"E140"),sQuery(id+"F0.wireOp",EDGE,"E141"),sQuery(id+"F0.wireOp",EDGE,"E142"),sQuery(id+"F0.wireOp",EDGE,"E143"),sQuery(id+"F0.wireOp",EDGE,"E144"),sQuery(id+"F0.wireOp",EDGE,"E145"),sQuery(id+"F0.wireOp",EDGE,"E146"),sQuery(id+"F0.wireOp",EDGE,"E147"),sQuery(id+"F0.wireOp",EDGE,"E148"),sQuery(id+"F0.wireOp",EDGE,"E149"),sQuery(id+"F0.wireOp",EDGE,"E150"),sQuery(id+"F0.wireOp",EDGE,"E151"),sQuery(id+"F0.wireOp",EDGE,"E152"),sQuery(id+"F0.wireOp",EDGE,"E153"),sQuery(id+"F0.wireOp",EDGE,"E154"),sQuery(id+"F0.wireOp",EDGE,"E155"),sQuery(id+"F0.wireOp",EDGE,"E156"),sQuery(id+"F0.wireOp",EDGE,"E157"),sQuery(id+"F0.wireOp",EDGE,"E158"),sQuery(id+"F0.wireOp",EDGE,"E159"),sQuery(id+"F0.wireOp",EDGE,"E160"),sQuery(id+"F0.wireOp",EDGE,"E161"),sQuery(id+"F0.wireOp",EDGE,"E162"),sQuery(id+"F0.wireOp",EDGE,"E163"),sQuery(id+"F0.wireOp",EDGE,"E164"),sQuery(id+"F0.wireOp",EDGE,"E165"),sQuery(id+"F0.wireOp",EDGE,"E166"),sQuery(id+"F0.wireOp",EDGE,"E167"),sQuery(id+"F0.wireOp",EDGE,"E168"),sQuery(id+"F0.wireOp",EDGE,"E169"),sQuery(id+"F0.wireOp",EDGE,"E170"),sQuery(id+"F0.wireOp",EDGE,"E171"),sQuery(id+"F0.wireOp",EDGE,"E172"),sQuery(id+"F0.wireOp",EDGE,"E173"),sQuery(id+"F0.wireOp",EDGE,"E174"),sQuery(id+"F0.wireOp",EDGE,"E175"),sQuery(id+"F0.wireOp",EDGE,"E176"),sQuery(id+"F0.wireOp",EDGE,"E177"),sQuery(id+"F0.wireOp",EDGE,"E178"),sQuery(id+"F0.wireOp",EDGE,"E179"),sQuery(id+"F0.wireOp",EDGE,"E180"),sQuery(id+"F0.wireOp",EDGE,"E181"),sQuery(id+"F0.wireOp",EDGE,"E182"),sQuery(id+"F0.wireOp",EDGE,"E183"),sQuery(id+"F0.wireOp",EDGE,"E184"),sQuery(id+"F0.wireOp",EDGE,"E185"),sQuery(id+"F0.wireOp",EDGE,"E186"),sQuery(id+"F0.wireOp",EDGE,"E187"),sQuery(id+"F0.wireOp",EDGE,"E188")])],"isStart":true})]});}
            var Q1;
            {var subQ0=sQuery(id+"F0.wireOp",EDGE,"E173");Q1=makeQuery(id+"F4.opChamfer","BLEND_EDGE",EDGE,{"blendedFrom":[makeQuery(id+"F1.opExtrude","CAP_EDGE",EDGE,{"disambiguationData":[OSD([subQ0])],"isStart":true}),makeQuery(id+"F1.opExtrude","CAP_FACE",FACE,{"disambiguationData":[OSD([sQuery(id+"F0.wireOp",EDGE,"E0"),sQuery(id+"F0.wireOp",EDGE,"E1"),sQuery(id+"F0.wireOp",EDGE,"E2"),sQuery(id+"F0.wireOp",EDGE,"E3"),sQuery(id+"F0.wireOp",EDGE,"E4"),sQuery(id+"F0.wireOp",EDGE,"E5"),sQuery(id+"F0.wireOp",EDGE,"E6"),sQuery(id+"F0.wireOp",EDGE,"E7"),sQuery(id+"F0.wireOp",EDGE,"E8"),sQuery(id+"F0.wireOp",EDGE,"E9"),sQuery(id+"F0.wireOp",EDGE,"E10"),sQuery(id+"F0.wireOp",EDGE,"E11"),sQuery(id+"F0.wireOp",EDGE,"E12"),sQuery(id+"F0.wireOp",EDGE,"E13"),sQuery(id+"F0.wireOp",EDGE,"E14"),sQuery(id+"F0.wireOp",EDGE,"E15"),sQuery(id+"F0.wireOp",EDGE,"E16"),sQuery(id+"F0.wireOp",EDGE,"E17"),sQuery(id+"F0.wireOp",EDGE,"E18"),sQuery(id+"F0.wireOp",EDGE,"E19"),sQuery(id+"F0.wireOp",EDGE,"E20"),sQuery(id+"F0.wireOp",EDGE,"E21"),sQuery(id+"F0.wireOp",EDGE,"E22"),sQuery(id+"F0.wireOp",EDGE,"E23"),sQuery(id+"F0.wireOp",EDGE,"E24"),sQuery(id+"F0.wireOp",EDGE,"E25"),sQuery(id+"F0.wireOp",EDGE,"E26"),sQuery(id+"F0.wireOp",EDGE,"E27"),sQuery(id+"F0.wireOp",EDGE,"E28"),sQuery(id+"F0.wireOp",EDGE,"E29"),sQuery(id+"F0.wireOp",EDGE,"E30"),sQuery(id+"F0.wireOp",EDGE,"E31"),sQuery(id+"F0.wireOp",EDGE,"E32"),sQuery(id+"F0.wireOp",EDGE,"E33"),sQuery(id+"F0.wireOp",EDGE,"E34"),sQuery(id+"F0.wireOp",EDGE,"E35"),sQuery(id+"F0.wireOp",EDGE,"E36"),sQuery(id+"F0.wireOp",EDGE,"E37"),sQuery(id+"F0.wireOp",EDGE,"E38"),sQuery(id+"F0.wireOp",EDGE,"E39"),sQuery(id+"F0.wireOp",EDGE,"E40"),sQuery(id+"F0.wireOp",EDGE,"E41"),sQuery(id+"F0.wireOp",EDGE,"E42"),sQuery(id+"F0.wireOp",EDGE,"E43"),sQuery(id+"F0.wireOp",EDGE,"E44"),sQuery(id+"F0.wireOp",EDGE,"E45"),sQuery(id+"F0.wireOp",EDGE,"E46"),sQuery(id+"F0.wireOp",EDGE,"E47"),sQuery(id+"F0.wireOp",EDGE,"E48"),sQuery(id+"F0.wireOp",EDGE,"E49"),sQuery(id+"F0.wireOp",EDGE,"E50"),sQuery(id+"F0.wireOp",EDGE,"E51"),sQuery(id+"F0.wireOp",EDGE,"E52"),sQuery(id+"F0.wireOp",EDGE,"E53"),sQuery(id+"F0.wireOp",EDGE,"E54"),sQuery(id+"F0.wireOp",EDGE,"E55"),sQuery(id+"F0.wireOp",EDGE,"E56"),sQuery(id+"F0.wireOp",EDGE,"E57"),sQuery(id+"F0.wireOp",EDGE,"E58"),sQuery(id+"F0.wireOp",EDGE,"E59"),sQuery(id+"F0.wireOp",EDGE,"E60"),sQuery(id+"F0.wireOp",EDGE,"E61"),sQuery(id+"F0.wireOp",EDGE,"E62"),sQuery(id+"F0.wireOp",EDGE,"E63"),sQuery(id+"F0.wireOp",EDGE,"E64"),sQuery(id+"F0.wireOp",EDGE,"E65"),sQuery(id+"F0.wireOp",EDGE,"E66"),sQuery(id+"F0.wireOp",EDGE,"E67"),sQuery(id+"F0.wireOp",EDGE,"E68"),sQuery(id+"F0.wireOp",EDGE,"E69"),sQuery(id+"F0.wireOp",EDGE,"E70"),sQuery(id+"F0.wireOp",EDGE,"E71"),sQuery(id+"F0.wireOp",EDGE,"E72"),sQuery(id+"F0.wireOp",EDGE,"E73"),sQuery(id+"F0.wireOp",EDGE,"E74"),sQuery(id+"F0.wireOp",EDGE,"E75"),sQuery(id+"F0.wireOp",EDGE,"E76"),sQuery(id+"F0.wireOp",EDGE,"E77"),sQuery(id+"F0.wireOp",EDGE,"E78"),sQuery(id+"F0.wireOp",EDGE,"E79"),sQuery(id+"F0.wireOp",EDGE,"E80"),sQuery(id+"F0.wireOp",EDGE,"E81"),sQuery(id+"F0.wireOp",EDGE,"E82"),sQuery(id+"F0.wireOp",EDGE,"E83"),sQuery(id+"F0.wireOp",EDGE,"E84"),sQuery(id+"F0.wireOp",EDGE,"E85"),sQuery(id+"F0.wireOp",EDGE,"E86"),sQuery(id+"F0.wireOp",EDGE,"E87"),sQuery(id+"F0.wireOp",EDGE,"E88"),sQuery(id+"F0.wireOp",EDGE,"E89"),sQuery(id+"F0.wireOp",EDGE,"E90"),sQuery(id+"F0.wireOp",EDGE,"E91"),sQuery(id+"F0.wireOp",EDGE,"E92"),sQuery(id+"F0.wireOp",EDGE,"E93"),sQuery(id+"F0.wireOp",EDGE,"E94"),sQuery(id+"F0.wireOp",EDGE,"E95"),sQuery(id+"F0.wireOp",EDGE,"E96"),sQuery(id+"F0.wireOp",EDGE,"E97"),sQuery(id+"F0.wireOp",EDGE,"E98"),sQuery(id+"F0.wireOp",EDGE,"E99"),sQuery(id+"F0.wireOp",EDGE,"E100"),sQuery(id+"F0.wireOp",EDGE,"E101"),sQuery(id+"F0.wireOp",EDGE,"E102"),sQuery(id+"F0.wireOp",EDGE,"E103"),sQuery(id+"F0.wireOp",EDGE,"E104"),sQuery(id+"F0.wireOp",EDGE,"E105"),sQuery(id+"F0.wireOp",EDGE,"E106"),sQuery(id+"F0.wireOp",EDGE,"E107"),sQuery(id+"F0.wireOp",EDGE,"E108"),sQuery(id+"F0.wireOp",EDGE,"E109"),sQuery(id+"F0.wireOp",EDGE,"E110"),sQuery(id+"F0.wireOp",EDGE,"E111"),sQuery(id+"F0.wireOp",EDGE,"E112"),sQuery(id+"F0.wireOp",EDGE,"E113"),sQuery(id+"F0.wireOp",EDGE,"E114"),sQuery(id+"F0.wireOp",EDGE,"E115"),sQuery(id+"F0.wireOp",EDGE,"E116"),sQuery(id+"F0.wireOp",EDGE,"E117"),sQuery(id+"F0.wireOp",EDGE,"E118"),sQuery(id+"F0.wireOp",EDGE,"E119"),sQuery(id+"F0.wireOp",EDGE,"E120"),sQuery(id+"F0.wireOp",EDGE,"E121"),sQuery(id+"F0.wireOp",EDGE,"E122"),sQuery(id+"F0.wireOp",EDGE,"E123"),sQuery(id+"F0.wireOp",EDGE,"E124"),sQuery(id+"F0.wireOp",EDGE,"E125"),sQuery(id+"F0.wireOp",EDGE,"E126"),sQuery(id+"F0.wireOp",EDGE,"E127"),sQuery(id+"F0.wireOp",EDGE,"E128"),sQuery(id+"F0.wireOp",EDGE,"E129"),sQuery(id+"F0.wireOp",EDGE,"E130"),sQuery(id+"F0.wireOp",EDGE,"E131"),sQuery(id+"F0.wireOp",EDGE,"E132"),sQuery(id+"F0.wireOp",EDGE,"E133"),sQuery(id+"F0.wireOp",EDGE,"E134"),sQuery(id+"F0.wireOp",EDGE,"E135"),sQuery(id+"F0.wireOp",EDGE,"E136"),sQuery(id+"F0.wireOp",EDGE,"E137"),sQuery(id+"F0.wireOp",EDGE,"E138"),sQuery(id+"F0.wireOp",EDGE,"E139"),sQuery(id+"F0.wireOp",EDGE,"E140"),sQuery(id+"F0.wireOp",EDGE,"E141"),sQuery(id+"F0.wireOp",EDGE,"E142"),sQuery(id+"F0.wireOp",EDGE,"E143"),sQuery(id+"F0.wireOp",EDGE,"E144"),sQuery(id+"F0.wireOp",EDGE,"E145"),sQuery(id+"F0.wireOp",EDGE,"E146"),sQuery(id+"F0.wireOp",EDGE,"E147"),sQuery(id+"F0.wireOp",EDGE,"E148"),sQuery(id+"F0.wireOp",EDGE,"E149"),sQuery(id+"F0.wireOp",EDGE,"E150"),sQuery(id+"F0.wireOp",EDGE,"E151"),sQuery(id+"F0.wireOp",EDGE,"E152"),sQuery(id+"F0.wireOp",EDGE,"E153"),sQuery(id+"F0.wireOp",EDGE,"E154"),sQuery(id+"F0.wireOp",EDGE,"E155"),sQuery(id+"F0.wireOp",EDGE,"E156"),sQuery(id+"F0.wireOp",EDGE,"E157"),sQuery(id+"F0.wireOp",EDGE,"E158"),sQuery(id+"F0.wireOp",EDGE,"E159"),sQuery(id+"F0.wireOp",EDGE,"E160"),sQuery(id+"F0.wireOp",EDGE,"E161"),sQuery(id+"F0.wireOp",EDGE,"E162"),sQuery(id+"F0.wireOp",EDGE,"E163"),sQuery(id+"F0.wireOp",EDGE,"E164"),sQuery(id+"F0.wireOp",EDGE,"E165"),sQuery(id+"F0.wireOp",EDGE,"E166"),sQuery(id+"F0.wireOp",EDGE,"E167"),sQuery(id+"F0.wireOp",EDGE,"E168"),sQuery(id+"F0.wireOp",EDGE,"E169"),sQuery(id+"F0.wireOp",EDGE,"E170"),sQuery(id+"F0.wireOp",EDGE,"E171"),sQuery(id+"F0.wireOp",EDGE,"E172"),subQ0,sQuery(id+"F0.wireOp",EDGE,"E174"),sQuery(id+"F0.wireOp",EDGE,"E175"),sQuery(id+"F0.wireOp",EDGE,"E176"),sQuery(id+"F0.wireOp",EDGE,"E177"),sQuery(id+"F0.wireOp",EDGE,"E178"),sQuery(id+"F0.wireOp",EDGE,"E179"),sQuery(id+"F0.wireOp",EDGE,"E180"),sQuery(id+"F0.wireOp",EDGE,"E181"),sQuery(id+"F0.wireOp",EDGE,"E182"),sQuery(id+"F0.wireOp",EDGE,"E183"),sQuery(id+"F0.wireOp",EDGE,"E184"),sQuery(id+"F0.wireOp",EDGE,"E185"),sQuery(id+"F0.wireOp",EDGE,"E186"),sQuery(id+"F0.wireOp",EDGE,"E187"),sQuery(id+"F0.wireOp",EDGE,"E188")])],"isStart":true})],"blendedInto":[makeQuery(id+"F1.opExtrude","CAP_FACE",FACE,{"disambiguationData":[OSD([sQuery(id+"F0.wireOp",EDGE,"E0"),sQuery(id+"F0.wireOp",EDGE,"E1"),sQuery(id+"F0.wireOp",EDGE,"E2"),sQuery(id+"F0.wireOp",EDGE,"E3"),sQuery(id+"F0.wireOp",EDGE,"E4"),sQuery(id+"F0.wireOp",EDGE,"E5"),sQuery(id+"F0.wireOp",EDGE,"E6"),sQuery(id+"F0.wireOp",EDGE,"E7"),sQuery(id+"F0.wireOp",EDGE,"E8"),sQuery(id+"F0.wireOp",EDGE,"E9"),sQuery(id+"F0.wireOp",EDGE,"E10"),sQuery(id+"F0.wireOp",EDGE,"E11"),sQuery(id+"F0.wireOp",EDGE,"E12"),sQuery(id+"F0.wireOp",EDGE,"E13"),sQuery(id+"F0.wireOp",EDGE,"E14"),sQuery(id+"F0.wireOp",EDGE,"E15"),sQuery(id+"F0.wireOp",EDGE,"E16"),sQuery(id+"F0.wireOp",EDGE,"E17"),sQuery(id+"F0.wireOp",EDGE,"E18"),sQuery(id+"F0.wireOp",EDGE,"E19"),sQuery(id+"F0.wireOp",EDGE,"E20"),sQuery(id+"F0.wireOp",EDGE,"E21"),sQuery(id+"F0.wireOp",EDGE,"E22"),sQuery(id+"F0.wireOp",EDGE,"E23"),sQuery(id+"F0.wireOp",EDGE,"E24"),sQuery(id+"F0.wireOp",EDGE,"E25"),sQuery(id+"F0.wireOp",EDGE,"E26"),sQuery(id+"F0.wireOp",EDGE,"E27"),sQuery(id+"F0.wireOp",EDGE,"E28"),sQuery(id+"F0.wireOp",EDGE,"E29"),sQuery(id+"F0.wireOp",EDGE,"E30"),sQuery(id+"F0.wireOp",EDGE,"E31"),sQuery(id+"F0.wireOp",EDGE,"E32"),sQuery(id+"F0.wireOp",EDGE,"E33"),sQuery(id+"F0.wireOp",EDGE,"E34"),sQuery(id+"F0.wireOp",EDGE,"E35"),sQuery(id+"F0.wireOp",EDGE,"E36"),sQuery(id+"F0.wireOp",EDGE,"E37"),sQuery(id+"F0.wireOp",EDGE,"E38"),sQuery(id+"F0.wireOp",EDGE,"E39"),sQuery(id+"F0.wireOp",EDGE,"E40"),sQuery(id+"F0.wireOp",EDGE,"E41"),sQuery(id+"F0.wireOp",EDGE,"E42"),sQuery(id+"F0.wireOp",EDGE,"E43"),sQuery(id+"F0.wireOp",EDGE,"E44"),sQuery(id+"F0.wireOp",EDGE,"E45"),sQuery(id+"F0.wireOp",EDGE,"E46"),sQuery(id+"F0.wireOp",EDGE,"E47"),sQuery(id+"F0.wireOp",EDGE,"E48"),sQuery(id+"F0.wireOp",EDGE,"E49"),sQuery(id+"F0.wireOp",EDGE,"E50"),sQuery(id+"F0.wireOp",EDGE,"E51"),sQuery(id+"F0.wireOp",EDGE,"E52"),sQuery(id+"F0.wireOp",EDGE,"E53"),sQuery(id+"F0.wireOp",EDGE,"E54"),sQuery(id+"F0.wireOp",EDGE,"E55"),sQuery(id+"F0.wireOp",EDGE,"E56"),sQuery(id+"F0.wireOp",EDGE,"E57"),sQuery(id+"F0.wireOp",EDGE,"E58"),sQuery(id+"F0.wireOp",EDGE,"E59"),sQuery(id+"F0.wireOp",EDGE,"E60"),sQuery(id+"F0.wireOp",EDGE,"E61"),sQuery(id+"F0.wireOp",EDGE,"E62"),sQuery(id+"F0.wireOp",EDGE,"E63"),sQuery(id+"F0.wireOp",EDGE,"E64"),sQuery(id+"F0.wireOp",EDGE,"E65"),sQuery(id+"F0.wireOp",EDGE,"E66"),sQuery(id+"F0.wireOp",EDGE,"E67"),sQuery(id+"F0.wireOp",EDGE,"E68"),sQuery(id+"F0.wireOp",EDGE,"E69"),sQuery(id+"F0.wireOp",EDGE,"E70"),sQuery(id+"F0.wireOp",EDGE,"E71"),sQuery(id+"F0.wireOp",EDGE,"E72"),sQuery(id+"F0.wireOp",EDGE,"E73"),sQuery(id+"F0.wireOp",EDGE,"E74"),sQuery(id+"F0.wireOp",EDGE,"E75"),sQuery(id+"F0.wireOp",EDGE,"E76"),sQuery(id+"F0.wireOp",EDGE,"E77"),sQuery(id+"F0.wireOp",EDGE,"E78"),sQuery(id+"F0.wireOp",EDGE,"E79"),sQuery(id+"F0.wireOp",EDGE,"E80"),sQuery(id+"F0.wireOp",EDGE,"E81"),sQuery(id+"F0.wireOp",EDGE,"E82"),sQuery(id+"F0.wireOp",EDGE,"E83"),sQuery(id+"F0.wireOp",EDGE,"E84"),sQuery(id+"F0.wireOp",EDGE,"E85"),sQuery(id+"F0.wireOp",EDGE,"E86"),sQuery(id+"F0.wireOp",EDGE,"E87"),sQuery(id+"F0.wireOp",EDGE,"E88"),sQuery(id+"F0.wireOp",EDGE,"E89"),sQuery(id+"F0.wireOp",EDGE,"E90"),sQuery(id+"F0.wireOp",EDGE,"E91"),sQuery(id+"F0.wireOp",EDGE,"E92"),sQuery(id+"F0.wireOp",EDGE,"E93"),sQuery(id+"F0.wireOp",EDGE,"E94"),sQuery(id+"F0.wireOp",EDGE,"E95"),sQuery(id+"F0.wireOp",EDGE,"E96"),sQuery(id+"F0.wireOp",EDGE,"E97"),sQuery(id+"F0.wireOp",EDGE,"E98"),sQuery(id+"F0.wireOp",EDGE,"E99"),sQuery(id+"F0.wireOp",EDGE,"E100"),sQuery(id+"F0.wireOp",EDGE,"E101"),sQuery(id+"F0.wireOp",EDGE,"E102"),sQuery(id+"F0.wireOp",EDGE,"E103"),sQuery(id+"F0.wireOp",EDGE,"E104"),sQuery(id+"F0.wireOp",EDGE,"E105"),sQuery(id+"F0.wireOp",EDGE,"E106"),sQuery(id+"F0.wireOp",EDGE,"E107"),sQuery(id+"F0.wireOp",EDGE,"E108"),sQuery(id+"F0.wireOp",EDGE,"E109"),sQuery(id+"F0.wireOp",EDGE,"E110"),sQuery(id+"F0.wireOp",EDGE,"E111"),sQuery(id+"F0.wireOp",EDGE,"E112"),sQuery(id+"F0.wireOp",EDGE,"E113"),sQuery(id+"F0.wireOp",EDGE,"E114"),sQuery(id+"F0.wireOp",EDGE,"E115"),sQuery(id+"F0.wireOp",EDGE,"E116"),sQuery(id+"F0.wireOp",EDGE,"E117"),sQuery(id+"F0.wireOp",EDGE,"E118"),sQuery(id+"F0.wireOp",EDGE,"E119"),sQuery(id+"F0.wireOp",EDGE,"E120"),sQuery(id+"F0.wireOp",EDGE,"E121"),sQuery(id+"F0.wireOp",EDGE,"E122"),sQuery(id+"F0.wireOp",EDGE,"E123"),sQuery(id+"F0.wireOp",EDGE,"E124"),sQuery(id+"F0.wireOp",EDGE,"E125"),sQuery(id+"F0.wireOp",EDGE,"E126"),sQuery(id+"F0.wireOp",EDGE,"E127"),sQuery(id+"F0.wireOp",EDGE,"E128"),sQuery(id+"F0.wireOp",EDGE,"E129"),sQuery(id+"F0.wireOp",EDGE,"E130"),sQuery(id+"F0.wireOp",EDGE,"E131"),sQuery(id+"F0.wireOp",EDGE,"E132"),sQuery(id+"F0.wireOp",EDGE,"E133"),sQuery(id+"F0.wireOp",EDGE,"E134"),sQuery(id+"F0.wireOp",EDGE,"E135"),sQuery(id+"F0.wireOp",EDGE,"E136"),sQuery(id+"F0.wireOp",EDGE,"E137"),sQuery(id+"F0.wireOp",EDGE,"E138"),sQuery(id+"F0.wireOp",EDGE,"E139"),sQuery(id+"F0.wireOp",EDGE,"E140"),sQuery(id+"F0.wireOp",EDGE,"E141"),sQuery(id+"F0.wireOp",EDGE,"E142"),sQuery(id+"F0.wireOp",EDGE,"E143"),sQuery(id+"F0.wireOp",EDGE,"E144"),sQuery(id+"F0.wireOp",EDGE,"E145"),sQuery(id+"F0.wireOp",EDGE,"E146"),sQuery(id+"F0.wireOp",EDGE,"E147"),sQuery(id+"F0.wireOp",EDGE,"E148"),sQuery(id+"F0.wireOp",EDGE,"E149"),sQuery(id+"F0.wireOp",EDGE,"E150"),sQuery(id+"F0.wireOp",EDGE,"E151"),sQuery(id+"F0.wireOp",EDGE,"E152"),sQuery(id+"F0.wireOp",EDGE,"E153"),sQuery(id+"F0.wireOp",EDGE,"E154"),sQuery(id+"F0.wireOp",EDGE,"E155"),sQuery(id+"F0.wireOp",EDGE,"E156"),sQuery(id+"F0.wireOp",EDGE,"E157"),sQuery(id+"F0.wireOp",EDGE,"E158"),sQuery(id+"F0.wireOp",EDGE,"E159"),sQuery(id+"F0.wireOp",EDGE,"E160"),sQuery(id+"F0.wireOp",EDGE,"E161"),sQuery(id+"F0.wireOp",EDGE,"E162"),sQuery(id+"F0.wireOp",EDGE,"E163"),sQuery(id+"F0.wireOp",EDGE,"E164"),sQuery(id+"F0.wireOp",EDGE,"E165"),sQuery(id+"F0.wireOp",EDGE,"E166"),sQuery(id+"F0.wireOp",EDGE,"E167"),sQuery(id+"F0.wireOp",EDGE,"E168"),sQuery(id+"F0.wireOp",EDGE,"E169"),sQuery(id+"F0.wireOp",EDGE,"E170"),sQuery(id+"F0.wireOp",EDGE,"E171"),sQuery(id+"F0.wireOp",EDGE,"E172"),subQ0,sQuery(id+"F0.wireOp",EDGE,"E174"),sQuery(id+"F0.wireOp",EDGE,"E175"),sQuery(id+"F0.wireOp",EDGE,"E176"),sQuery(id+"F0.wireOp",EDGE,"E177"),sQuery(id+"F0.wireOp",EDGE,"E178"),sQuery(id+"F0.wireOp",EDGE,"E179"),sQuery(id+"F0.wireOp",EDGE,"E180"),sQuery(id+"F0.wireOp",EDGE,"E181"),sQuery(id+"F0.wireOp",EDGE,"E182"),sQuery(id+"F0.wireOp",EDGE,"E183"),sQuery(id+"F0.wireOp",EDGE,"E184"),sQuery(id+"F0.wireOp",EDGE,"E185"),sQuery(id+"F0.wireOp",EDGE,"E186"),sQuery(id+"F0.wireOp",EDGE,"E187"),sQuery(id+"F0.wireOp",EDGE,"E188")])],"isStart":true})]});}
            var Q2;
            Q2=makeQuery(id+"F1.opExtrude","CAP_EDGE",EDGE,{"disambiguationData":[OSD([sQuery(id+"F0.wireOp",EDGE,"E108")])],"isStart":true});
            var Q3;
            {var subQ0=sQuery(id+"F0.wireOp",EDGE,"E101");Q3=makeQuery(id+"F5.opChamfer","BLEND_EDGE",EDGE,{"blendedFrom":[makeQuery(id+"F1.opExtrude","CAP_EDGE",EDGE,{"disambiguationData":[OSD([subQ0])],"isStart":true}),makeQuery(id+"F1.opExtrude","CAP_FACE",FACE,{"disambiguationData":[OSD([sQuery(id+"F0.wireOp",EDGE,"E0"),sQuery(id+"F0.wireOp",EDGE,"E1"),sQuery(id+"F0.wireOp",EDGE,"E2"),sQuery(id+"F0.wireOp",EDGE,"E3"),sQuery(id+"F0.wireOp",EDGE,"E4"),sQuery(id+"F0.wireOp",EDGE,"E5"),sQuery(id+"F0.wireOp",EDGE,"E6"),sQuery(id+"F0.wireOp",EDGE,"E7"),sQuery(id+"F0.wireOp",EDGE,"E8"),sQuery(id+"F0.wireOp",EDGE,"E9"),sQuery(id+"F0.wireOp",EDGE,"E10"),sQuery(id+"F0.wireOp",EDGE,"E11"),sQuery(id+"F0.wireOp",EDGE,"E12"),sQuery(id+"F0.wireOp",EDGE,"E13"),sQuery(id+"F0.wireOp",EDGE,"E14"),sQuery(id+"F0.wireOp",EDGE,"E15"),sQuery(id+"F0.wireOp",EDGE,"E16"),sQuery(id+"F0.wireOp",EDGE,"E17"),sQuery(id+"F0.wireOp",EDGE,"E18"),sQuery(id+"F0.wireOp",EDGE,"E19"),sQuery(id+"F0.wireOp",EDGE,"E20"),sQuery(id+"F0.wireOp",EDGE,"E21"),sQuery(id+"F0.wireOp",EDGE,"E22"),sQuery(id+"F0.wireOp",EDGE,"E23"),sQuery(id+"F0.wireOp",EDGE,"E24"),sQuery(id+"F0.wireOp",EDGE,"E25"),sQuery(id+"F0.wireOp",EDGE,"E26"),sQuery(id+"F0.wireOp",EDGE,"E27"),sQuery(id+"F0.wireOp",EDGE,"E28"),sQuery(id+"F0.wireOp",EDGE,"E29"),sQuery(id+"F0.wireOp",EDGE,"E30"),sQuery(id+"F0.wireOp",EDGE,"E31"),sQuery(id+"F0.wireOp",EDGE,"E32"),sQuery(id+"F0.wireOp",EDGE,"E33"),sQuery(id+"F0.wireOp",EDGE,"E34"),sQuery(id+"F0.wireOp",EDGE,"E35"),sQuery(id+"F0.wireOp",EDGE,"E36"),sQuery(id+"F0.wireOp",EDGE,"E37"),sQuery(id+"F0.wireOp",EDGE,"E38"),sQuery(id+"F0.wireOp",EDGE,"E39"),sQuery(id+"F0.wireOp",EDGE,"E40"),sQuery(id+"F0.wireOp",EDGE,"E41"),sQuery(id+"F0.wireOp",EDGE,"E42"),sQuery(id+"F0.wireOp",EDGE,"E43"),sQuery(id+"F0.wireOp",EDGE,"E44"),sQuery(id+"F0.wireOp",EDGE,"E45"),sQuery(id+"F0.wireOp",EDGE,"E46"),sQuery(id+"F0.wireOp",EDGE,"E47"),sQuery(id+"F0.wireOp",EDGE,"E48"),sQuery(id+"F0.wireOp",EDGE,"E49"),sQuery(id+"F0.wireOp",EDGE,"E50"),sQuery(id+"F0.wireOp",EDGE,"E51"),sQuery(id+"F0.wireOp",EDGE,"E52"),sQuery(id+"F0.wireOp",EDGE,"E53"),sQuery(id+"F0.wireOp",EDGE,"E54"),sQuery(id+"F0.wireOp",EDGE,"E55"),sQuery(id+"F0.wireOp",EDGE,"E56"),sQuery(id+"F0.wireOp",EDGE,"E57"),sQuery(id+"F0.wireOp",EDGE,"E58"),sQuery(id+"F0.wireOp",EDGE,"E59"),sQuery(id+"F0.wireOp",EDGE,"E60"),sQuery(id+"F0.wireOp",EDGE,"E61"),sQuery(id+"F0.wireOp",EDGE,"E62"),sQuery(id+"F0.wireOp",EDGE,"E63"),sQuery(id+"F0.wireOp",EDGE,"E64"),sQuery(id+"F0.wireOp",EDGE,"E65"),sQuery(id+"F0.wireOp",EDGE,"E66"),sQuery(id+"F0.wireOp",EDGE,"E67"),sQuery(id+"F0.wireOp",EDGE,"E68"),sQuery(id+"F0.wireOp",EDGE,"E69"),sQuery(id+"F0.wireOp",EDGE,"E70"),sQuery(id+"F0.wireOp",EDGE,"E71"),sQuery(id+"F0.wireOp",EDGE,"E72"),sQuery(id+"F0.wireOp",EDGE,"E73"),sQuery(id+"F0.wireOp",EDGE,"E74"),sQuery(id+"F0.wireOp",EDGE,"E75"),sQuery(id+"F0.wireOp",EDGE,"E76"),sQuery(id+"F0.wireOp",EDGE,"E77"),sQuery(id+"F0.wireOp",EDGE,"E78"),sQuery(id+"F0.wireOp",EDGE,"E79"),sQuery(id+"F0.wireOp",EDGE,"E80"),sQuery(id+"F0.wireOp",EDGE,"E81"),sQuery(id+"F0.wireOp",EDGE,"E82"),sQuery(id+"F0.wireOp",EDGE,"E83"),sQuery(id+"F0.wireOp",EDGE,"E84"),sQuery(id+"F0.wireOp",EDGE,"E85"),sQuery(id+"F0.wireOp",EDGE,"E86"),sQuery(id+"F0.wireOp",EDGE,"E87"),sQuery(id+"F0.wireOp",EDGE,"E88"),sQuery(id+"F0.wireOp",EDGE,"E89"),sQuery(id+"F0.wireOp",EDGE,"E90"),sQuery(id+"F0.wireOp",EDGE,"E91"),sQuery(id+"F0.wireOp",EDGE,"E92"),sQuery(id+"F0.wireOp",EDGE,"E93"),sQuery(id+"F0.wireOp",EDGE,"E94"),sQuery(id+"F0.wireOp",EDGE,"E95"),sQuery(id+"F0.wireOp",EDGE,"E96"),sQuery(id+"F0.wireOp",EDGE,"E97"),sQuery(id+"F0.wireOp",EDGE,"E98"),sQuery(id+"F0.wireOp",EDGE,"E99"),sQuery(id+"F0.wireOp",EDGE,"E100"),subQ0,sQuery(id+"F0.wireOp",EDGE,"E102"),sQuery(id+"F0.wireOp",EDGE,"E103"),sQuery(id+"F0.wireOp",EDGE,"E104"),sQuery(id+"F0.wireOp",EDGE,"E105"),sQuery(id+"F0.wireOp",EDGE,"E106"),sQuery(id+"F0.wireOp",EDGE,"E107"),sQuery(id+"F0.wireOp",EDGE,"E108"),sQuery(id+"F0.wireOp",EDGE,"E109"),sQuery(id+"F0.wireOp",EDGE,"E110"),sQuery(id+"F0.wireOp",EDGE,"E111"),sQuery(id+"F0.wireOp",EDGE,"E112"),sQuery(id+"F0.wireOp",EDGE,"E113"),sQuery(id+"F0.wireOp",EDGE,"E114"),sQuery(id+"F0.wireOp",EDGE,"E115"),sQuery(id+"F0.wireOp",EDGE,"E116"),sQuery(id+"F0.wireOp",EDGE,"E117"),sQuery(id+"F0.wireOp",EDGE,"E118"),sQuery(id+"F0.wireOp",EDGE,"E119"),sQuery(id+"F0.wireOp",EDGE,"E120"),sQuery(id+"F0.wireOp",EDGE,"E121"),sQuery(id+"F0.wireOp",EDGE,"E122"),sQuery(id+"F0.wireOp",EDGE,"E123"),sQuery(id+"F0.wireOp",EDGE,"E124"),sQuery(id+"F0.wireOp",EDGE,"E125"),sQuery(id+"F0.wireOp",EDGE,"E126"),sQuery(id+"F0.wireOp",EDGE,"E127"),sQuery(id+"F0.wireOp",EDGE,"E128"),sQuery(id+"F0.wireOp",EDGE,"E129"),sQuery(id+"F0.wireOp",EDGE,"E130"),sQuery(id+"F0.wireOp",EDGE,"E131"),sQuery(id+"F0.wireOp",EDGE,"E132"),sQuery(id+"F0.wireOp",EDGE,"E133"),sQuery(id+"F0.wireOp",EDGE,"E134"),sQuery(id+"F0.wireOp",EDGE,"E135"),sQuery(id+"F0.wireOp",EDGE,"E136"),sQuery(id+"F0.wireOp",EDGE,"E137"),sQuery(id+"F0.wireOp",EDGE,"E138"),sQuery(id+"F0.wireOp",EDGE,"E139"),sQuery(id+"F0.wireOp",EDGE,"E140"),sQuery(id+"F0.wireOp",EDGE,"E141"),sQuery(id+"F0.wireOp",EDGE,"E142"),sQuery(id+"F0.wireOp",EDGE,"E143"),sQuery(id+"F0.wireOp",EDGE,"E144"),sQuery(id+"F0.wireOp",EDGE,"E145"),sQuery(id+"F0.wireOp",EDGE,"E146"),sQuery(id+"F0.wireOp",EDGE,"E147"),sQuery(id+"F0.wireOp",EDGE,"E148"),sQuery(id+"F0.wireOp",EDGE,"E149"),sQuery(id+"F0.wireOp",EDGE,"E150"),sQuery(id+"F0.wireOp",EDGE,"E151"),sQuery(id+"F0.wireOp",EDGE,"E152"),sQuery(id+"F0.wireOp",EDGE,"E153"),sQuery(id+"F0.wireOp",EDGE,"E154"),sQuery(id+"F0.wireOp",EDGE,"E155"),sQuery(id+"F0.wireOp",EDGE,"E156"),sQuery(id+"F0.wireOp",EDGE,"E157"),sQuery(id+"F0.wireOp",EDGE,"E158"),sQuery(id+"F0.wireOp",EDGE,"E159"),sQuery(id+"F0.wireOp",EDGE,"E160"),sQuery(id+"F0.wireOp",EDGE,"E161"),sQuery(id+"F0.wireOp",EDGE,"E162"),sQuery(id+"F0.wireOp",EDGE,"E163"),sQuery(id+"F0.wireOp",EDGE,"E164"),sQuery(id+"F0.wireOp",EDGE,"E165"),sQuery(id+"F0.wireOp",EDGE,"E166"),sQuery(id+"F0.wireOp",EDGE,"E167"),sQuery(id+"F0.wireOp",EDGE,"E168"),sQuery(id+"F0.wireOp",EDGE,"E169"),sQuery(id+"F0.wireOp",EDGE,"E170"),sQuery(id+"F0.wireOp",EDGE,"E171"),sQuery(id+"F0.wireOp",EDGE,"E172"),sQuery(id+"F0.wireOp",EDGE,"E173"),sQuery(id+"F0.wireOp",EDGE,"E174"),sQuery(id+"F0.wireOp",EDGE,"E175"),sQuery(id+"F0.wireOp",EDGE,"E176"),sQuery(id+"F0.wireOp",EDGE,"E177"),sQuery(id+"F0.wireOp",EDGE,"E178"),sQuery(id+"F0.wireOp",EDGE,"E179"),sQuery(id+"F0.wireOp",EDGE,"E180"),sQuery(id+"F0.wireOp",EDGE,"E181"),sQuery(id+"F0.wireOp",EDGE,"E182"),sQuery(id+"F0.wireOp",EDGE,"E183"),sQuery(id+"F0.wireOp",EDGE,"E184"),sQuery(id+"F0.wireOp",EDGE,"E185"),sQuery(id+"F0.wireOp",EDGE,"E186"),sQuery(id+"F0.wireOp",EDGE,"E187"),sQuery(id+"F0.wireOp",EDGE,"E188")])],"isStart":true})],"blendedInto":[makeQuery(id+"F1.opExtrude","CAP_FACE",FACE,{"disambiguationData":[OSD([sQuery(id+"F0.wireOp",EDGE,"E0"),sQuery(id+"F0.wireOp",EDGE,"E1"),sQuery(id+"F0.wireOp",EDGE,"E2"),sQuery(id+"F0.wireOp",EDGE,"E3"),sQuery(id+"F0.wireOp",EDGE,"E4"),sQuery(id+"F0.wireOp",EDGE,"E5"),sQuery(id+"F0.wireOp",EDGE,"E6"),sQuery(id+"F0.wireOp",EDGE,"E7"),sQuery(id+"F0.wireOp",EDGE,"E8"),sQuery(id+"F0.wireOp",EDGE,"E9"),sQuery(id+"F0.wireOp",EDGE,"E10"),sQuery(id+"F0.wireOp",EDGE,"E11"),sQuery(id+"F0.wireOp",EDGE,"E12"),sQuery(id+"F0.wireOp",EDGE,"E13"),sQuery(id+"F0.wireOp",EDGE,"E14"),sQuery(id+"F0.wireOp",EDGE,"E15"),sQuery(id+"F0.wireOp",EDGE,"E16"),sQuery(id+"F0.wireOp",EDGE,"E17"),sQuery(id+"F0.wireOp",EDGE,"E18"),sQuery(id+"F0.wireOp",EDGE,"E19"),sQuery(id+"F0.wireOp",EDGE,"E20"),sQuery(id+"F0.wireOp",EDGE,"E21"),sQuery(id+"F0.wireOp",EDGE,"E22"),sQuery(id+"F0.wireOp",EDGE,"E23"),sQuery(id+"F0.wireOp",EDGE,"E24"),sQuery(id+"F0.wireOp",EDGE,"E25"),sQuery(id+"F0.wireOp",EDGE,"E26"),sQuery(id+"F0.wireOp",EDGE,"E27"),sQuery(id+"F0.wireOp",EDGE,"E28"),sQuery(id+"F0.wireOp",EDGE,"E29"),sQuery(id+"F0.wireOp",EDGE,"E30"),sQuery(id+"F0.wireOp",EDGE,"E31"),sQuery(id+"F0.wireOp",EDGE,"E32"),sQuery(id+"F0.wireOp",EDGE,"E33"),sQuery(id+"F0.wireOp",EDGE,"E34"),sQuery(id+"F0.wireOp",EDGE,"E35"),sQuery(id+"F0.wireOp",EDGE,"E36"),sQuery(id+"F0.wireOp",EDGE,"E37"),sQuery(id+"F0.wireOp",EDGE,"E38"),sQuery(id+"F0.wireOp",EDGE,"E39"),sQuery(id+"F0.wireOp",EDGE,"E40"),sQuery(id+"F0.wireOp",EDGE,"E41"),sQuery(id+"F0.wireOp",EDGE,"E42"),sQuery(id+"F0.wireOp",EDGE,"E43"),sQuery(id+"F0.wireOp",EDGE,"E44"),sQuery(id+"F0.wireOp",EDGE,"E45"),sQuery(id+"F0.wireOp",EDGE,"E46"),sQuery(id+"F0.wireOp",EDGE,"E47"),sQuery(id+"F0.wireOp",EDGE,"E48"),sQuery(id+"F0.wireOp",EDGE,"E49"),sQuery(id+"F0.wireOp",EDGE,"E50"),sQuery(id+"F0.wireOp",EDGE,"E51"),sQuery(id+"F0.wireOp",EDGE,"E52"),sQuery(id+"F0.wireOp",EDGE,"E53"),sQuery(id+"F0.wireOp",EDGE,"E54"),sQuery(id+"F0.wireOp",EDGE,"E55"),sQuery(id+"F0.wireOp",EDGE,"E56"),sQuery(id+"F0.wireOp",EDGE,"E57"),sQuery(id+"F0.wireOp",EDGE,"E58"),sQuery(id+"F0.wireOp",EDGE,"E59"),sQuery(id+"F0.wireOp",EDGE,"E60"),sQuery(id+"F0.wireOp",EDGE,"E61"),sQuery(id+"F0.wireOp",EDGE,"E62"),sQuery(id+"F0.wireOp",EDGE,"E63"),sQuery(id+"F0.wireOp",EDGE,"E64"),sQuery(id+"F0.wireOp",EDGE,"E65"),sQuery(id+"F0.wireOp",EDGE,"E66"),sQuery(id+"F0.wireOp",EDGE,"E67"),sQuery(id+"F0.wireOp",EDGE,"E68"),sQuery(id+"F0.wireOp",EDGE,"E69"),sQuery(id+"F0.wireOp",EDGE,"E70"),sQuery(id+"F0.wireOp",EDGE,"E71"),sQuery(id+"F0.wireOp",EDGE,"E72"),sQuery(id+"F0.wireOp",EDGE,"E73"),sQuery(id+"F0.wireOp",EDGE,"E74"),sQuery(id+"F0.wireOp",EDGE,"E75"),sQuery(id+"F0.wireOp",EDGE,"E76"),sQuery(id+"F0.wireOp",EDGE,"E77"),sQuery(id+"F0.wireOp",EDGE,"E78"),sQuery(id+"F0.wireOp",EDGE,"E79"),sQuery(id+"F0.wireOp",EDGE,"E80"),sQuery(id+"F0.wireOp",EDGE,"E81"),sQuery(id+"F0.wireOp",EDGE,"E82"),sQuery(id+"F0.wireOp",EDGE,"E83"),sQuery(id+"F0.wireOp",EDGE,"E84"),sQuery(id+"F0.wireOp",EDGE,"E85"),sQuery(id+"F0.wireOp",EDGE,"E86"),sQuery(id+"F0.wireOp",EDGE,"E87"),sQuery(id+"F0.wireOp",EDGE,"E88"),sQuery(id+"F0.wireOp",EDGE,"E89"),sQuery(id+"F0.wireOp",EDGE,"E90"),sQuery(id+"F0.wireOp",EDGE,"E91"),sQuery(id+"F0.wireOp",EDGE,"E92"),sQuery(id+"F0.wireOp",EDGE,"E93"),sQuery(id+"F0.wireOp",EDGE,"E94"),sQuery(id+"F0.wireOp",EDGE,"E95"),sQuery(id+"F0.wireOp",EDGE,"E96"),sQuery(id+"F0.wireOp",EDGE,"E97"),sQuery(id+"F0.wireOp",EDGE,"E98"),sQuery(id+"F0.wireOp",EDGE,"E99"),sQuery(id+"F0.wireOp",EDGE,"E100"),subQ0,sQuery(id+"F0.wireOp",EDGE,"E102"),sQuery(id+"F0.wireOp",EDGE,"E103"),sQuery(id+"F0.wireOp",EDGE,"E104"),sQuery(id+"F0.wireOp",EDGE,"E105"),sQuery(id+"F0.wireOp",EDGE,"E106"),sQuery(id+"F0.wireOp",EDGE,"E107"),sQuery(id+"F0.wireOp",EDGE,"E108"),sQuery(id+"F0.wireOp",EDGE,"E109"),sQuery(id+"F0.wireOp",EDGE,"E110"),sQuery(id+"F0.wireOp",EDGE,"E111"),sQuery(id+"F0.wireOp",EDGE,"E112"),sQuery(id+"F0.wireOp",EDGE,"E113"),sQuery(id+"F0.wireOp",EDGE,"E114"),sQuery(id+"F0.wireOp",EDGE,"E115"),sQuery(id+"F0.wireOp",EDGE,"E116"),sQuery(id+"F0.wireOp",EDGE,"E117"),sQuery(id+"F0.wireOp",EDGE,"E118"),sQuery(id+"F0.wireOp",EDGE,"E119"),sQuery(id+"F0.wireOp",EDGE,"E120"),sQuery(id+"F0.wireOp",EDGE,"E121"),sQuery(id+"F0.wireOp",EDGE,"E122"),sQuery(id+"F0.wireOp",EDGE,"E123"),sQuery(id+"F0.wireOp",EDGE,"E124"),sQuery(id+"F0.wireOp",EDGE,"E125"),sQuery(id+"F0.wireOp",EDGE,"E126"),sQuery(id+"F0.wireOp",EDGE,"E127"),sQuery(id+"F0.wireOp",EDGE,"E128"),sQuery(id+"F0.wireOp",EDGE,"E129"),sQuery(id+"F0.wireOp",EDGE,"E130"),sQuery(id+"F0.wireOp",EDGE,"E131"),sQuery(id+"F0.wireOp",EDGE,"E132"),sQuery(id+"F0.wireOp",EDGE,"E133"),sQuery(id+"F0.wireOp",EDGE,"E134"),sQuery(id+"F0.wireOp",EDGE,"E135"),sQuery(id+"F0.wireOp",EDGE,"E136"),sQuery(id+"F0.wireOp",EDGE,"E137"),sQuery(id+"F0.wireOp",EDGE,"E138"),sQuery(id+"F0.wireOp",EDGE,"E139"),sQuery(id+"F0.wireOp",EDGE,"E140"),sQuery(id+"F0.wireOp",EDGE,"E141"),sQuery(id+"F0.wireOp",EDGE,"E142"),sQuery(id+"F0.wireOp",EDGE,"E143"),sQuery(id+"F0.wireOp",EDGE,"E144"),sQuery(id+"F0.wireOp",EDGE,"E145"),sQuery(id+"F0.wireOp",EDGE,"E146"),sQuery(id+"F0.wireOp",EDGE,"E147"),sQuery(id+"F0.wireOp",EDGE,"E148"),sQuery(id+"F0.wireOp",EDGE,"E149"),sQuery(id+"F0.wireOp",EDGE,"E150"),sQuery(id+"F0.wireOp",EDGE,"E151"),sQuery(id+"F0.wireOp",EDGE,"E152"),sQuery(id+"F0.wireOp",EDGE,"E153"),sQuery(id+"F0.wireOp",EDGE,"E154"),sQuery(id+"F0.wireOp",EDGE,"E155"),sQuery(id+"F0.wireOp",EDGE,"E156"),sQuery(id+"F0.wireOp",EDGE,"E157"),sQuery(id+"F0.wireOp",EDGE,"E158"),sQuery(id+"F0.wireOp",EDGE,"E159"),sQuery(id+"F0.wireOp",EDGE,"E160"),sQuery(id+"F0.wireOp",EDGE,"E161"),sQuery(id+"F0.wireOp",EDGE,"E162"),sQuery(id+"F0.wireOp",EDGE,"E163"),sQuery(id+"F0.wireOp",EDGE,"E164"),sQuery(id+"F0.wireOp",EDGE,"E165"),sQuery(id+"F0.wireOp",EDGE,"E166"),sQuery(id+"F0.wireOp",EDGE,"E167"),sQuery(id+"F0.wireOp",EDGE,"E168"),sQuery(id+"F0.wireOp",EDGE,"E169"),sQuery(id+"F0.wireOp",EDGE,"E170"),sQuery(id+"F0.wireOp",EDGE,"E171"),sQuery(id+"F0.wireOp",EDGE,"E172"),sQuery(id+"F0.wireOp",EDGE,"E173"),sQuery(id+"F0.wireOp",EDGE,"E174"),sQuery(id+"F0.wireOp",EDGE,"E175"),sQuery(id+"F0.wireOp",EDGE,"E176"),sQuery(id+"F0.wireOp",EDGE,"E177"),sQuery(id+"F0.wireOp",EDGE,"E178"),sQuery(id+"F0.wireOp",EDGE,"E179"),sQuery(id+"F0.wireOp",EDGE,"E180"),sQuery(id+"F0.wireOp",EDGE,"E181"),sQuery(id+"F0.wireOp",EDGE,"E182"),sQuery(id+"F0.wireOp",EDGE,"E183"),sQuery(id+"F0.wireOp",EDGE,"E184"),sQuery(id+"F0.wireOp",EDGE,"E185"),sQuery(id+"F0.wireOp",EDGE,"E186"),sQuery(id+"F0.wireOp",EDGE,"E187"),sQuery(id+"F0.wireOp",EDGE,"E188")])],"isStart":true})]});}
            fillet(context, id + "F8", {"entities" : qUnion([Q0, Q1, Q2, Q3]), "radius" : 20 * mm, "tangentPropagation" : true, "allowEdgeOverflow" : false});
        }
        {
            var Q0;
            {var subQ0=sQuery(id+"F0.wireOp",EDGE,"E83");Q0=makeQuery(id+"F5.opChamfer","BLEND_EDGE",EDGE,{"blendedFrom":[makeQuery(id+"F1.opExtrude","CAP_EDGE",EDGE,{"disambiguationData":[OSD([subQ0])],"isStart":true}),makeQuery(id+"F1.opExtrude","CAP_FACE",FACE,{"disambiguationData":[OSD([sQuery(id+"F0.wireOp",EDGE,"E0"),sQuery(id+"F0.wireOp",EDGE,"E1"),sQuery(id+"F0.wireOp",EDGE,"E2"),sQuery(id+"F0.wireOp",EDGE,"E3"),sQuery(id+"F0.wireOp",EDGE,"E4"),sQuery(id+"F0.wireOp",EDGE,"E5"),sQuery(id+"F0.wireOp",EDGE,"E6"),sQuery(id+"F0.wireOp",EDGE,"E7"),sQuery(id+"F0.wireOp",EDGE,"E8"),sQuery(id+"F0.wireOp",EDGE,"E9"),sQuery(id+"F0.wireOp",EDGE,"E10"),sQuery(id+"F0.wireOp",EDGE,"E11"),sQuery(id+"F0.wireOp",EDGE,"E12"),sQuery(id+"F0.wireOp",EDGE,"E13"),sQuery(id+"F0.wireOp",EDGE,"E14"),sQuery(id+"F0.wireOp",EDGE,"E15"),sQuery(id+"F0.wireOp",EDGE,"E16"),sQuery(id+"F0.wireOp",EDGE,"E17"),sQuery(id+"F0.wireOp",EDGE,"E18"),sQuery(id+"F0.wireOp",EDGE,"E19"),sQuery(id+"F0.wireOp",EDGE,"E20"),sQuery(id+"F0.wireOp",EDGE,"E21"),sQuery(id+"F0.wireOp",EDGE,"E22"),sQuery(id+"F0.wireOp",EDGE,"E23"),sQuery(id+"F0.wireOp",EDGE,"E24"),sQuery(id+"F0.wireOp",EDGE,"E25"),sQuery(id+"F0.wireOp",EDGE,"E26"),sQuery(id+"F0.wireOp",EDGE,"E27"),sQuery(id+"F0.wireOp",EDGE,"E28"),sQuery(id+"F0.wireOp",EDGE,"E29"),sQuery(id+"F0.wireOp",EDGE,"E30"),sQuery(id+"F0.wireOp",EDGE,"E31"),sQuery(id+"F0.wireOp",EDGE,"E32"),sQuery(id+"F0.wireOp",EDGE,"E33"),sQuery(id+"F0.wireOp",EDGE,"E34"),sQuery(id+"F0.wireOp",EDGE,"E35"),sQuery(id+"F0.wireOp",EDGE,"E36"),sQuery(id+"F0.wireOp",EDGE,"E37"),sQuery(id+"F0.wireOp",EDGE,"E38"),sQuery(id+"F0.wireOp",EDGE,"E39"),sQuery(id+"F0.wireOp",EDGE,"E40"),sQuery(id+"F0.wireOp",EDGE,"E41"),sQuery(id+"F0.wireOp",EDGE,"E42"),sQuery(id+"F0.wireOp",EDGE,"E43"),sQuery(id+"F0.wireOp",EDGE,"E44"),sQuery(id+"F0.wireOp",EDGE,"E45"),sQuery(id+"F0.wireOp",EDGE,"E46"),sQuery(id+"F0.wireOp",EDGE,"E47"),sQuery(id+"F0.wireOp",EDGE,"E48"),sQuery(id+"F0.wireOp",EDGE,"E49"),sQuery(id+"F0.wireOp",EDGE,"E50"),sQuery(id+"F0.wireOp",EDGE,"E51"),sQuery(id+"F0.wireOp",EDGE,"E52"),sQuery(id+"F0.wireOp",EDGE,"E53"),sQuery(id+"F0.wireOp",EDGE,"E54"),sQuery(id+"F0.wireOp",EDGE,"E55"),sQuery(id+"F0.wireOp",EDGE,"E56"),sQuery(id+"F0.wireOp",EDGE,"E57"),sQuery(id+"F0.wireOp",EDGE,"E58"),sQuery(id+"F0.wireOp",EDGE,"E59"),sQuery(id+"F0.wireOp",EDGE,"E60"),sQuery(id+"F0.wireOp",EDGE,"E61"),sQuery(id+"F0.wireOp",EDGE,"E62"),sQuery(id+"F0.wireOp",EDGE,"E63"),sQuery(id+"F0.wireOp",EDGE,"E64"),sQuery(id+"F0.wireOp",EDGE,"E65"),sQuery(id+"F0.wireOp",EDGE,"E66"),sQuery(id+"F0.wireOp",EDGE,"E67"),sQuery(id+"F0.wireOp",EDGE,"E68"),sQuery(id+"F0.wireOp",EDGE,"E69"),sQuery(id+"F0.wireOp",EDGE,"E70"),sQuery(id+"F0.wireOp",EDGE,"E71"),sQuery(id+"F0.wireOp",EDGE,"E72"),sQuery(id+"F0.wireOp",EDGE,"E73"),sQuery(id+"F0.wireOp",EDGE,"E74"),sQuery(id+"F0.wireOp",EDGE,"E75"),sQuery(id+"F0.wireOp",EDGE,"E76"),sQuery(id+"F0.wireOp",EDGE,"E77"),sQuery(id+"F0.wireOp",EDGE,"E78"),sQuery(id+"F0.wireOp",EDGE,"E79"),sQuery(id+"F0.wireOp",EDGE,"E80"),sQuery(id+"F0.wireOp",EDGE,"E81"),sQuery(id+"F0.wireOp",EDGE,"E82"),subQ0,sQuery(id+"F0.wireOp",EDGE,"E84"),sQuery(id+"F0.wireOp",EDGE,"E85"),sQuery(id+"F0.wireOp",EDGE,"E86"),sQuery(id+"F0.wireOp",EDGE,"E87"),sQuery(id+"F0.wireOp",EDGE,"E88"),sQuery(id+"F0.wireOp",EDGE,"E89"),sQuery(id+"F0.wireOp",EDGE,"E90"),sQuery(id+"F0.wireOp",EDGE,"E91"),sQuery(id+"F0.wireOp",EDGE,"E92"),sQuery(id+"F0.wireOp",EDGE,"E93"),sQuery(id+"F0.wireOp",EDGE,"E94"),sQuery(id+"F0.wireOp",EDGE,"E95"),sQuery(id+"F0.wireOp",EDGE,"E96"),sQuery(id+"F0.wireOp",EDGE,"E97"),sQuery(id+"F0.wireOp",EDGE,"E98"),sQuery(id+"F0.wireOp",EDGE,"E99"),sQuery(id+"F0.wireOp",EDGE,"E100"),sQuery(id+"F0.wireOp",EDGE,"E101"),sQuery(id+"F0.wireOp",EDGE,"E102"),sQuery(id+"F0.wireOp",EDGE,"E103"),sQuery(id+"F0.wireOp",EDGE,"E104"),sQuery(id+"F0.wireOp",EDGE,"E105"),sQuery(id+"F0.wireOp",EDGE,"E106"),sQuery(id+"F0.wireOp",EDGE,"E107"),sQuery(id+"F0.wireOp",EDGE,"E108"),sQuery(id+"F0.wireOp",EDGE,"E109"),sQuery(id+"F0.wireOp",EDGE,"E110"),sQuery(id+"F0.wireOp",EDGE,"E111"),sQuery(id+"F0.wireOp",EDGE,"E112"),sQuery(id+"F0.wireOp",EDGE,"E113"),sQuery(id+"F0.wireOp",EDGE,"E114"),sQuery(id+"F0.wireOp",EDGE,"E115"),sQuery(id+"F0.wireOp",EDGE,"E116"),sQuery(id+"F0.wireOp",EDGE,"E117"),sQuery(id+"F0.wireOp",EDGE,"E118"),sQuery(id+"F0.wireOp",EDGE,"E119"),sQuery(id+"F0.wireOp",EDGE,"E120"),sQuery(id+"F0.wireOp",EDGE,"E121"),sQuery(id+"F0.wireOp",EDGE,"E122"),sQuery(id+"F0.wireOp",EDGE,"E123"),sQuery(id+"F0.wireOp",EDGE,"E124"),sQuery(id+"F0.wireOp",EDGE,"E125"),sQuery(id+"F0.wireOp",EDGE,"E126"),sQuery(id+"F0.wireOp",EDGE,"E127"),sQuery(id+"F0.wireOp",EDGE,"E128"),sQuery(id+"F0.wireOp",EDGE,"E129"),sQuery(id+"F0.wireOp",EDGE,"E130"),sQuery(id+"F0.wireOp",EDGE,"E131"),sQuery(id+"F0.wireOp",EDGE,"E132"),sQuery(id+"F0.wireOp",EDGE,"E133"),sQuery(id+"F0.wireOp",EDGE,"E134"),sQuery(id+"F0.wireOp",EDGE,"E135"),sQuery(id+"F0.wireOp",EDGE,"E136"),sQuery(id+"F0.wireOp",EDGE,"E137"),sQuery(id+"F0.wireOp",EDGE,"E138"),sQuery(id+"F0.wireOp",EDGE,"E139"),sQuery(id+"F0.wireOp",EDGE,"E140"),sQuery(id+"F0.wireOp",EDGE,"E141"),sQuery(id+"F0.wireOp",EDGE,"E142"),sQuery(id+"F0.wireOp",EDGE,"E143"),sQuery(id+"F0.wireOp",EDGE,"E144"),sQuery(id+"F0.wireOp",EDGE,"E145"),sQuery(id+"F0.wireOp",EDGE,"E146"),sQuery(id+"F0.wireOp",EDGE,"E147"),sQuery(id+"F0.wireOp",EDGE,"E148"),sQuery(id+"F0.wireOp",EDGE,"E149"),sQuery(id+"F0.wireOp",EDGE,"E150"),sQuery(id+"F0.wireOp",EDGE,"E151"),sQuery(id+"F0.wireOp",EDGE,"E152"),sQuery(id+"F0.wireOp",EDGE,"E153"),sQuery(id+"F0.wireOp",EDGE,"E154"),sQuery(id+"F0.wireOp",EDGE,"E155"),sQuery(id+"F0.wireOp",EDGE,"E156"),sQuery(id+"F0.wireOp",EDGE,"E157"),sQuery(id+"F0.wireOp",EDGE,"E158"),sQuery(id+"F0.wireOp",EDGE,"E159"),sQuery(id+"F0.wireOp",EDGE,"E160"),sQuery(id+"F0.wireOp",EDGE,"E161"),sQuery(id+"F0.wireOp",EDGE,"E162"),sQuery(id+"F0.wireOp",EDGE,"E163"),sQuery(id+"F0.wireOp",EDGE,"E164"),sQuery(id+"F0.wireOp",EDGE,"E165"),sQuery(id+"F0.wireOp",EDGE,"E166"),sQuery(id+"F0.wireOp",EDGE,"E167"),sQuery(id+"F0.wireOp",EDGE,"E168"),sQuery(id+"F0.wireOp",EDGE,"E169"),sQuery(id+"F0.wireOp",EDGE,"E170"),sQuery(id+"F0.wireOp",EDGE,"E171"),sQuery(id+"F0.wireOp",EDGE,"E172"),sQuery(id+"F0.wireOp",EDGE,"E173"),sQuery(id+"F0.wireOp",EDGE,"E174"),sQuery(id+"F0.wireOp",EDGE,"E175"),sQuery(id+"F0.wireOp",EDGE,"E176"),sQuery(id+"F0.wireOp",EDGE,"E177"),sQuery(id+"F0.wireOp",EDGE,"E178"),sQuery(id+"F0.wireOp",EDGE,"E179"),sQuery(id+"F0.wireOp",EDGE,"E180"),sQuery(id+"F0.wireOp",EDGE,"E181"),sQuery(id+"F0.wireOp",EDGE,"E182"),sQuery(id+"F0.wireOp",EDGE,"E183"),sQuery(id+"F0.wireOp",EDGE,"E184"),sQuery(id+"F0.wireOp",EDGE,"E185"),sQuery(id+"F0.wireOp",EDGE,"E186"),sQuery(id+"F0.wireOp",EDGE,"E187"),sQuery(id+"F0.wireOp",EDGE,"E188")])],"isStart":true})],"blendedInto":[makeQuery(id+"F1.opExtrude","CAP_FACE",FACE,{"disambiguationData":[OSD([sQuery(id+"F0.wireOp",EDGE,"E0"),sQuery(id+"F0.wireOp",EDGE,"E1"),sQuery(id+"F0.wireOp",EDGE,"E2"),sQuery(id+"F0.wireOp",EDGE,"E3"),sQuery(id+"F0.wireOp",EDGE,"E4"),sQuery(id+"F0.wireOp",EDGE,"E5"),sQuery(id+"F0.wireOp",EDGE,"E6"),sQuery(id+"F0.wireOp",EDGE,"E7"),sQuery(id+"F0.wireOp",EDGE,"E8"),sQuery(id+"F0.wireOp",EDGE,"E9"),sQuery(id+"F0.wireOp",EDGE,"E10"),sQuery(id+"F0.wireOp",EDGE,"E11"),sQuery(id+"F0.wireOp",EDGE,"E12"),sQuery(id+"F0.wireOp",EDGE,"E13"),sQuery(id+"F0.wireOp",EDGE,"E14"),sQuery(id+"F0.wireOp",EDGE,"E15"),sQuery(id+"F0.wireOp",EDGE,"E16"),sQuery(id+"F0.wireOp",EDGE,"E17"),sQuery(id+"F0.wireOp",EDGE,"E18"),sQuery(id+"F0.wireOp",EDGE,"E19"),sQuery(id+"F0.wireOp",EDGE,"E20"),sQuery(id+"F0.wireOp",EDGE,"E21"),sQuery(id+"F0.wireOp",EDGE,"E22"),sQuery(id+"F0.wireOp",EDGE,"E23"),sQuery(id+"F0.wireOp",EDGE,"E24"),sQuery(id+"F0.wireOp",EDGE,"E25"),sQuery(id+"F0.wireOp",EDGE,"E26"),sQuery(id+"F0.wireOp",EDGE,"E27"),sQuery(id+"F0.wireOp",EDGE,"E28"),sQuery(id+"F0.wireOp",EDGE,"E29"),sQuery(id+"F0.wireOp",EDGE,"E30"),sQuery(id+"F0.wireOp",EDGE,"E31"),sQuery(id+"F0.wireOp",EDGE,"E32"),sQuery(id+"F0.wireOp",EDGE,"E33"),sQuery(id+"F0.wireOp",EDGE,"E34"),sQuery(id+"F0.wireOp",EDGE,"E35"),sQuery(id+"F0.wireOp",EDGE,"E36"),sQuery(id+"F0.wireOp",EDGE,"E37"),sQuery(id+"F0.wireOp",EDGE,"E38"),sQuery(id+"F0.wireOp",EDGE,"E39"),sQuery(id+"F0.wireOp",EDGE,"E40"),sQuery(id+"F0.wireOp",EDGE,"E41"),sQuery(id+"F0.wireOp",EDGE,"E42"),sQuery(id+"F0.wireOp",EDGE,"E43"),sQuery(id+"F0.wireOp",EDGE,"E44"),sQuery(id+"F0.wireOp",EDGE,"E45"),sQuery(id+"F0.wireOp",EDGE,"E46"),sQuery(id+"F0.wireOp",EDGE,"E47"),sQuery(id+"F0.wireOp",EDGE,"E48"),sQuery(id+"F0.wireOp",EDGE,"E49"),sQuery(id+"F0.wireOp",EDGE,"E50"),sQuery(id+"F0.wireOp",EDGE,"E51"),sQuery(id+"F0.wireOp",EDGE,"E52"),sQuery(id+"F0.wireOp",EDGE,"E53"),sQuery(id+"F0.wireOp",EDGE,"E54"),sQuery(id+"F0.wireOp",EDGE,"E55"),sQuery(id+"F0.wireOp",EDGE,"E56"),sQuery(id+"F0.wireOp",EDGE,"E57"),sQuery(id+"F0.wireOp",EDGE,"E58"),sQuery(id+"F0.wireOp",EDGE,"E59"),sQuery(id+"F0.wireOp",EDGE,"E60"),sQuery(id+"F0.wireOp",EDGE,"E61"),sQuery(id+"F0.wireOp",EDGE,"E62"),sQuery(id+"F0.wireOp",EDGE,"E63"),sQuery(id+"F0.wireOp",EDGE,"E64"),sQuery(id+"F0.wireOp",EDGE,"E65"),sQuery(id+"F0.wireOp",EDGE,"E66"),sQuery(id+"F0.wireOp",EDGE,"E67"),sQuery(id+"F0.wireOp",EDGE,"E68"),sQuery(id+"F0.wireOp",EDGE,"E69"),sQuery(id+"F0.wireOp",EDGE,"E70"),sQuery(id+"F0.wireOp",EDGE,"E71"),sQuery(id+"F0.wireOp",EDGE,"E72"),sQuery(id+"F0.wireOp",EDGE,"E73"),sQuery(id+"F0.wireOp",EDGE,"E74"),sQuery(id+"F0.wireOp",EDGE,"E75"),sQuery(id+"F0.wireOp",EDGE,"E76"),sQuery(id+"F0.wireOp",EDGE,"E77"),sQuery(id+"F0.wireOp",EDGE,"E78"),sQuery(id+"F0.wireOp",EDGE,"E79"),sQuery(id+"F0.wireOp",EDGE,"E80"),sQuery(id+"F0.wireOp",EDGE,"E81"),sQuery(id+"F0.wireOp",EDGE,"E82"),subQ0,sQuery(id+"F0.wireOp",EDGE,"E84"),sQuery(id+"F0.wireOp",EDGE,"E85"),sQuery(id+"F0.wireOp",EDGE,"E86"),sQuery(id+"F0.wireOp",EDGE,"E87"),sQuery(id+"F0.wireOp",EDGE,"E88"),sQuery(id+"F0.wireOp",EDGE,"E89"),sQuery(id+"F0.wireOp",EDGE,"E90"),sQuery(id+"F0.wireOp",EDGE,"E91"),sQuery(id+"F0.wireOp",EDGE,"E92"),sQuery(id+"F0.wireOp",EDGE,"E93"),sQuery(id+"F0.wireOp",EDGE,"E94"),sQuery(id+"F0.wireOp",EDGE,"E95"),sQuery(id+"F0.wireOp",EDGE,"E96"),sQuery(id+"F0.wireOp",EDGE,"E97"),sQuery(id+"F0.wireOp",EDGE,"E98"),sQuery(id+"F0.wireOp",EDGE,"E99"),sQuery(id+"F0.wireOp",EDGE,"E100"),sQuery(id+"F0.wireOp",EDGE,"E101"),sQuery(id+"F0.wireOp",EDGE,"E102"),sQuery(id+"F0.wireOp",EDGE,"E103"),sQuery(id+"F0.wireOp",EDGE,"E104"),sQuery(id+"F0.wireOp",EDGE,"E105"),sQuery(id+"F0.wireOp",EDGE,"E106"),sQuery(id+"F0.wireOp",EDGE,"E107"),sQuery(id+"F0.wireOp",EDGE,"E108"),sQuery(id+"F0.wireOp",EDGE,"E109"),sQuery(id+"F0.wireOp",EDGE,"E110"),sQuery(id+"F0.wireOp",EDGE,"E111"),sQuery(id+"F0.wireOp",EDGE,"E112"),sQuery(id+"F0.wireOp",EDGE,"E113"),sQuery(id+"F0.wireOp",EDGE,"E114"),sQuery(id+"F0.wireOp",EDGE,"E115"),sQuery(id+"F0.wireOp",EDGE,"E116"),sQuery(id+"F0.wireOp",EDGE,"E117"),sQuery(id+"F0.wireOp",EDGE,"E118"),sQuery(id+"F0.wireOp",EDGE,"E119"),sQuery(id+"F0.wireOp",EDGE,"E120"),sQuery(id+"F0.wireOp",EDGE,"E121"),sQuery(id+"F0.wireOp",EDGE,"E122"),sQuery(id+"F0.wireOp",EDGE,"E123"),sQuery(id+"F0.wireOp",EDGE,"E124"),sQuery(id+"F0.wireOp",EDGE,"E125"),sQuery(id+"F0.wireOp",EDGE,"E126"),sQuery(id+"F0.wireOp",EDGE,"E127"),sQuery(id+"F0.wireOp",EDGE,"E128"),sQuery(id+"F0.wireOp",EDGE,"E129"),sQuery(id+"F0.wireOp",EDGE,"E130"),sQuery(id+"F0.wireOp",EDGE,"E131"),sQuery(id+"F0.wireOp",EDGE,"E132"),sQuery(id+"F0.wireOp",EDGE,"E133"),sQuery(id+"F0.wireOp",EDGE,"E134"),sQuery(id+"F0.wireOp",EDGE,"E135"),sQuery(id+"F0.wireOp",EDGE,"E136"),sQuery(id+"F0.wireOp",EDGE,"E137"),sQuery(id+"F0.wireOp",EDGE,"E138"),sQuery(id+"F0.wireOp",EDGE,"E139"),sQuery(id+"F0.wireOp",EDGE,"E140"),sQuery(id+"F0.wireOp",EDGE,"E141"),sQuery(id+"F0.wireOp",EDGE,"E142"),sQuery(id+"F0.wireOp",EDGE,"E143"),sQuery(id+"F0.wireOp",EDGE,"E144"),sQuery(id+"F0.wireOp",EDGE,"E145"),sQuery(id+"F0.wireOp",EDGE,"E146"),sQuery(id+"F0.wireOp",EDGE,"E147"),sQuery(id+"F0.wireOp",EDGE,"E148"),sQuery(id+"F0.wireOp",EDGE,"E149"),sQuery(id+"F0.wireOp",EDGE,"E150"),sQuery(id+"F0.wireOp",EDGE,"E151"),sQuery(id+"F0.wireOp",EDGE,"E152"),sQuery(id+"F0.wireOp",EDGE,"E153"),sQuery(id+"F0.wireOp",EDGE,"E154"),sQuery(id+"F0.wireOp",EDGE,"E155"),sQuery(id+"F0.wireOp",EDGE,"E156"),sQuery(id+"F0.wireOp",EDGE,"E157"),sQuery(id+"F0.wireOp",EDGE,"E158"),sQuery(id+"F0.wireOp",EDGE,"E159"),sQuery(id+"F0.wireOp",EDGE,"E160"),sQuery(id+"F0.wireOp",EDGE,"E161"),sQuery(id+"F0.wireOp",EDGE,"E162"),sQuery(id+"F0.wireOp",EDGE,"E163"),sQuery(id+"F0.wireOp",EDGE,"E164"),sQuery(id+"F0.wireOp",EDGE,"E165"),sQuery(id+"F0.wireOp",EDGE,"E166"),sQuery(id+"F0.wireOp",EDGE,"E167"),sQuery(id+"F0.wireOp",EDGE,"E168"),sQuery(id+"F0.wireOp",EDGE,"E169"),sQuery(id+"F0.wireOp",EDGE,"E170"),sQuery(id+"F0.wireOp",EDGE,"E171"),sQuery(id+"F0.wireOp",EDGE,"E172"),sQuery(id+"F0.wireOp",EDGE,"E173"),sQuery(id+"F0.wireOp",EDGE,"E174"),sQuery(id+"F0.wireOp",EDGE,"E175"),sQuery(id+"F0.wireOp",EDGE,"E176"),sQuery(id+"F0.wireOp",EDGE,"E177"),sQuery(id+"F0.wireOp",EDGE,"E178"),sQuery(id+"F0.wireOp",EDGE,"E179"),sQuery(id+"F0.wireOp",EDGE,"E180"),sQuery(id+"F0.wireOp",EDGE,"E181"),sQuery(id+"F0.wireOp",EDGE,"E182"),sQuery(id+"F0.wireOp",EDGE,"E183"),sQuery(id+"F0.wireOp",EDGE,"E184"),sQuery(id+"F0.wireOp",EDGE,"E185"),sQuery(id+"F0.wireOp",EDGE,"E186"),sQuery(id+"F0.wireOp",EDGE,"E187"),sQuery(id+"F0.wireOp",EDGE,"E188")])],"isStart":true})]});}
            fillet(context, id + "F9", {"entities" : qUnion([Q0]), "radius" : 20 * mm, "tangentPropagation" : true, "allowEdgeOverflow" : false});
        }
        {
            var Q0;
            {var subQ0=sQuery(id+"F0.wireOp",EDGE,"E18");var subQ1=sQuery(id+"F0.wireOp",EDGE,"E49");Q0=makeQuery(id+"F8.opFillet","BLEND_EDGE",EDGE,{"blendedFrom":[makeQuery(id+"F4.opChamfer","BLEND_EDGE",EDGE,{"blendedFrom":[makeQuery(id+"F1.opExtrude","CAP_EDGE",EDGE,{"disambiguationData":[OSD([subQ1])],"isStart":true}),makeQuery(id+"F1.opExtrude","CAP_FACE",FACE,{"disambiguationData":[OSD([sQuery(id+"F0.wireOp",EDGE,"E0"),sQuery(id+"F0.wireOp",EDGE,"E1"),sQuery(id+"F0.wireOp",EDGE,"E2"),sQuery(id+"F0.wireOp",EDGE,"E3"),sQuery(id+"F0.wireOp",EDGE,"E4"),sQuery(id+"F0.wireOp",EDGE,"E5"),sQuery(id+"F0.wireOp",EDGE,"E6"),sQuery(id+"F0.wireOp",EDGE,"E7"),sQuery(id+"F0.wireOp",EDGE,"E8"),sQuery(id+"F0.wireOp",EDGE,"E9"),sQuery(id+"F0.wireOp",EDGE,"E10"),sQuery(id+"F0.wireOp",EDGE,"E11"),sQuery(id+"F0.wireOp",EDGE,"E12"),sQuery(id+"F0.wireOp",EDGE,"E13"),sQuery(id+"F0.wireOp",EDGE,"E14"),sQuery(id+"F0.wireOp",EDGE,"E15"),sQuery(id+"F0.wireOp",EDGE,"E16"),sQuery(id+"F0.wireOp",EDGE,"E17"),subQ0,sQuery(id+"F0.wireOp",EDGE,"E19"),sQuery(id+"F0.wireOp",EDGE,"E20"),sQuery(id+"F0.wireOp",EDGE,"E21"),sQuery(id+"F0.wireOp",EDGE,"E22"),sQuery(id+"F0.wireOp",EDGE,"E23"),sQuery(id+"F0.wireOp",EDGE,"E24"),sQuery(id+"F0.wireOp",EDGE,"E25"),sQuery(id+"F0.wireOp",EDGE,"E26"),sQuery(id+"F0.wireOp",EDGE,"E27"),sQuery(id+"F0.wireOp",EDGE,"E28"),sQuery(id+"F0.wireOp",EDGE,"E29"),sQuery(id+"F0.wireOp",EDGE,"E30"),sQuery(id+"F0.wireOp",EDGE,"E31"),sQuery(id+"F0.wireOp",EDGE,"E32"),sQuery(id+"F0.wireOp",EDGE,"E33"),sQuery(id+"F0.wireOp",EDGE,"E34"),sQuery(id+"F0.wireOp",EDGE,"E35"),sQuery(id+"F0.wireOp",EDGE,"E36"),sQuery(id+"F0.wireOp",EDGE,"E37"),sQuery(id+"F0.wireOp",EDGE,"E38"),sQuery(id+"F0.wireOp",EDGE,"E39"),sQuery(id+"F0.wireOp",EDGE,"E40"),sQuery(id+"F0.wireOp",EDGE,"E41"),sQuery(id+"F0.wireOp",EDGE,"E42"),sQuery(id+"F0.wireOp",EDGE,"E43"),sQuery(id+"F0.wireOp",EDGE,"E44"),sQuery(id+"F0.wireOp",EDGE,"E45"),sQuery(id+"F0.wireOp",EDGE,"E46"),sQuery(id+"F0.wireOp",EDGE,"E47"),sQuery(id+"F0.wireOp",EDGE,"E48"),subQ1,sQuery(id+"F0.wireOp",EDGE,"E50"),sQuery(id+"F0.wireOp",EDGE,"E51"),sQuery(id+"F0.wireOp",EDGE,"E52"),sQuery(id+"F0.wireOp",EDGE,"E53"),sQuery(id+"F0.wireOp",EDGE,"E54"),sQuery(id+"F0.wireOp",EDGE,"E55"),sQuery(id+"F0.wireOp",EDGE,"E56"),sQuery(id+"F0.wireOp",EDGE,"E57"),sQuery(id+"F0.wireOp",EDGE,"E58"),sQuery(id+"F0.wireOp",EDGE,"E59"),sQuery(id+"F0.wireOp",EDGE,"E60"),sQuery(id+"F0.wireOp",EDGE,"E61"),sQuery(id+"F0.wireOp",EDGE,"E62"),sQuery(id+"F0.wireOp",EDGE,"E63"),sQuery(id+"F0.wireOp",EDGE,"E64"),sQuery(id+"F0.wireOp",EDGE,"E65"),sQuery(id+"F0.wireOp",EDGE,"E66"),sQuery(id+"F0.wireOp",EDGE,"E67"),sQuery(id+"F0.wireOp",EDGE,"E68"),sQuery(id+"F0.wireOp",EDGE,"E69"),sQuery(id+"F0.wireOp",EDGE,"E70"),sQuery(id+"F0.wireOp",EDGE,"E71"),sQuery(id+"F0.wireOp",EDGE,"E72"),sQuery(id+"F0.wireOp",EDGE,"E73"),sQuery(id+"F0.wireOp",EDGE,"E74"),sQuery(id+"F0.wireOp",EDGE,"E75"),sQuery(id+"F0.wireOp",EDGE,"E76"),sQuery(id+"F0.wireOp",EDGE,"E77"),sQuery(id+"F0.wireOp",EDGE,"E78"),sQuery(id+"F0.wireOp",EDGE,"E79"),sQuery(id+"F0.wireOp",EDGE,"E80"),sQuery(id+"F0.wireOp",EDGE,"E81"),sQuery(id+"F0.wireOp",EDGE,"E82"),sQuery(id+"F0.wireOp",EDGE,"E83"),sQuery(id+"F0.wireOp",EDGE,"E84"),sQuery(id+"F0.wireOp",EDGE,"E85"),sQuery(id+"F0.wireOp",EDGE,"E86"),sQuery(id+"F0.wireOp",EDGE,"E87"),sQuery(id+"F0.wireOp",EDGE,"E88"),sQuery(id+"F0.wireOp",EDGE,"E89"),sQuery(id+"F0.wireOp",EDGE,"E90"),sQuery(id+"F0.wireOp",EDGE,"E91"),sQuery(id+"F0.wireOp",EDGE,"E92"),sQuery(id+"F0.wireOp",EDGE,"E93"),sQuery(id+"F0.wireOp",EDGE,"E94"),sQuery(id+"F0.wireOp",EDGE,"E95"),sQuery(id+"F0.wireOp",EDGE,"E96"),sQuery(id+"F0.wireOp",EDGE,"E97"),sQuery(id+"F0.wireOp",EDGE,"E98"),sQuery(id+"F0.wireOp",EDGE,"E99"),sQuery(id+"F0.wireOp",EDGE,"E100"),sQuery(id+"F0.wireOp",EDGE,"E101"),sQuery(id+"F0.wireOp",EDGE,"E102"),sQuery(id+"F0.wireOp",EDGE,"E103"),sQuery(id+"F0.wireOp",EDGE,"E104"),sQuery(id+"F0.wireOp",EDGE,"E105"),sQuery(id+"F0.wireOp",EDGE,"E106"),sQuery(id+"F0.wireOp",EDGE,"E107"),sQuery(id+"F0.wireOp",EDGE,"E108"),sQuery(id+"F0.wireOp",EDGE,"E109"),sQuery(id+"F0.wireOp",EDGE,"E110"),sQuery(id+"F0.wireOp",EDGE,"E111"),sQuery(id+"F0.wireOp",EDGE,"E112"),sQuery(id+"F0.wireOp",EDGE,"E113"),sQuery(id+"F0.wireOp",EDGE,"E114"),sQuery(id+"F0.wireOp",EDGE,"E115"),sQuery(id+"F0.wireOp",EDGE,"E116"),sQuery(id+"F0.wireOp",EDGE,"E117"),sQuery(id+"F0.wireOp",EDGE,"E118"),sQuery(id+"F0.wireOp",EDGE,"E119"),sQuery(id+"F0.wireOp",EDGE,"E120"),sQuery(id+"F0.wireOp",EDGE,"E121"),sQuery(id+"F0.wireOp",EDGE,"E122"),sQuery(id+"F0.wireOp",EDGE,"E123"),sQuery(id+"F0.wireOp",EDGE,"E124"),sQuery(id+"F0.wireOp",EDGE,"E125"),sQuery(id+"F0.wireOp",EDGE,"E126"),sQuery(id+"F0.wireOp",EDGE,"E127"),sQuery(id+"F0.wireOp",EDGE,"E128"),sQuery(id+"F0.wireOp",EDGE,"E129"),sQuery(id+"F0.wireOp",EDGE,"E130"),sQuery(id+"F0.wireOp",EDGE,"E131"),sQuery(id+"F0.wireOp",EDGE,"E132"),sQuery(id+"F0.wireOp",EDGE,"E133"),sQuery(id+"F0.wireOp",EDGE,"E134"),sQuery(id+"F0.wireOp",EDGE,"E135"),sQuery(id+"F0.wireOp",EDGE,"E136"),sQuery(id+"F0.wireOp",EDGE,"E137"),sQuery(id+"F0.wireOp",EDGE,"E138"),sQuery(id+"F0.wireOp",EDGE,"E139"),sQuery(id+"F0.wireOp",EDGE,"E140"),sQuery(id+"F0.wireOp",EDGE,"E141"),sQuery(id+"F0.wireOp",EDGE,"E142"),sQuery(id+"F0.wireOp",EDGE,"E143"),sQuery(id+"F0.wireOp",EDGE,"E144"),sQuery(id+"F0.wireOp",EDGE,"E145"),sQuery(id+"F0.wireOp",EDGE,"E146"),sQuery(id+"F0.wireOp",EDGE,"E147"),sQuery(id+"F0.wireOp",EDGE,"E148"),sQuery(id+"F0.wireOp",EDGE,"E149"),sQuery(id+"F0.wireOp",EDGE,"E150"),sQuery(id+"F0.wireOp",EDGE,"E151"),sQuery(id+"F0.wireOp",EDGE,"E152"),sQuery(id+"F0.wireOp",EDGE,"E153"),sQuery(id+"F0.wireOp",EDGE,"E154"),sQuery(id+"F0.wireOp",EDGE,"E155"),sQuery(id+"F0.wireOp",EDGE,"E156"),sQuery(id+"F0.wireOp",EDGE,"E157"),sQuery(id+"F0.wireOp",EDGE,"E158"),sQuery(id+"F0.wireOp",EDGE,"E159"),sQuery(id+"F0.wireOp",EDGE,"E160"),sQuery(id+"F0.wireOp",EDGE,"E161"),sQuery(id+"F0.wireOp",EDGE,"E162"),sQuery(id+"F0.wireOp",EDGE,"E163"),sQuery(id+"F0.wireOp",EDGE,"E164"),sQuery(id+"F0.wireOp",EDGE,"E165"),sQuery(id+"F0.wireOp",EDGE,"E166"),sQuery(id+"F0.wireOp",EDGE,"E167"),sQuery(id+"F0.wireOp",EDGE,"E168"),sQuery(id+"F0.wireOp",EDGE,"E169"),sQuery(id+"F0.wireOp",EDGE,"E170"),sQuery(id+"F0.wireOp",EDGE,"E171"),sQuery(id+"F0.wireOp",EDGE,"E172"),sQuery(id+"F0.wireOp",EDGE,"E173"),sQuery(id+"F0.wireOp",EDGE,"E174"),sQuery(id+"F0.wireOp",EDGE,"E175"),sQuery(id+"F0.wireOp",EDGE,"E176"),sQuery(id+"F0.wireOp",EDGE,"E177"),sQuery(id+"F0.wireOp",EDGE,"E178"),sQuery(id+"F0.wireOp",EDGE,"E179"),sQuery(id+"F0.wireOp",EDGE,"E180"),sQuery(id+"F0.wireOp",EDGE,"E181"),sQuery(id+"F0.wireOp",EDGE,"E182"),sQuery(id+"F0.wireOp",EDGE,"E183"),sQuery(id+"F0.wireOp",EDGE,"E184"),sQuery(id+"F0.wireOp",EDGE,"E185"),sQuery(id+"F0.wireOp",EDGE,"E186"),sQuery(id+"F0.wireOp",EDGE,"E187"),sQuery(id+"F0.wireOp",EDGE,"E188")])],"isStart":true})],"blendedInto":[makeQuery(id+"F1.opExtrude","CAP_FACE",FACE,{"disambiguationData":[OSD([sQuery(id+"F0.wireOp",EDGE,"E0"),sQuery(id+"F0.wireOp",EDGE,"E1"),sQuery(id+"F0.wireOp",EDGE,"E2"),sQuery(id+"F0.wireOp",EDGE,"E3"),sQuery(id+"F0.wireOp",EDGE,"E4"),sQuery(id+"F0.wireOp",EDGE,"E5"),sQuery(id+"F0.wireOp",EDGE,"E6"),sQuery(id+"F0.wireOp",EDGE,"E7"),sQuery(id+"F0.wireOp",EDGE,"E8"),sQuery(id+"F0.wireOp",EDGE,"E9"),sQuery(id+"F0.wireOp",EDGE,"E10"),sQuery(id+"F0.wireOp",EDGE,"E11"),sQuery(id+"F0.wireOp",EDGE,"E12"),sQuery(id+"F0.wireOp",EDGE,"E13"),sQuery(id+"F0.wireOp",EDGE,"E14"),sQuery(id+"F0.wireOp",EDGE,"E15"),sQuery(id+"F0.wireOp",EDGE,"E16"),sQuery(id+"F0.wireOp",EDGE,"E17"),subQ0,sQuery(id+"F0.wireOp",EDGE,"E19"),sQuery(id+"F0.wireOp",EDGE,"E20"),sQuery(id+"F0.wireOp",EDGE,"E21"),sQuery(id+"F0.wireOp",EDGE,"E22"),sQuery(id+"F0.wireOp",EDGE,"E23"),sQuery(id+"F0.wireOp",EDGE,"E24"),sQuery(id+"F0.wireOp",EDGE,"E25"),sQuery(id+"F0.wireOp",EDGE,"E26"),sQuery(id+"F0.wireOp",EDGE,"E27"),sQuery(id+"F0.wireOp",EDGE,"E28"),sQuery(id+"F0.wireOp",EDGE,"E29"),sQuery(id+"F0.wireOp",EDGE,"E30"),sQuery(id+"F0.wireOp",EDGE,"E31"),sQuery(id+"F0.wireOp",EDGE,"E32"),sQuery(id+"F0.wireOp",EDGE,"E33"),sQuery(id+"F0.wireOp",EDGE,"E34"),sQuery(id+"F0.wireOp",EDGE,"E35"),sQuery(id+"F0.wireOp",EDGE,"E36"),sQuery(id+"F0.wireOp",EDGE,"E37"),sQuery(id+"F0.wireOp",EDGE,"E38"),sQuery(id+"F0.wireOp",EDGE,"E39"),sQuery(id+"F0.wireOp",EDGE,"E40"),sQuery(id+"F0.wireOp",EDGE,"E41"),sQuery(id+"F0.wireOp",EDGE,"E42"),sQuery(id+"F0.wireOp",EDGE,"E43"),sQuery(id+"F0.wireOp",EDGE,"E44"),sQuery(id+"F0.wireOp",EDGE,"E45"),sQuery(id+"F0.wireOp",EDGE,"E46"),sQuery(id+"F0.wireOp",EDGE,"E47"),sQuery(id+"F0.wireOp",EDGE,"E48"),subQ1,sQuery(id+"F0.wireOp",EDGE,"E50"),sQuery(id+"F0.wireOp",EDGE,"E51"),sQuery(id+"F0.wireOp",EDGE,"E52"),sQuery(id+"F0.wireOp",EDGE,"E53"),sQuery(id+"F0.wireOp",EDGE,"E54"),sQuery(id+"F0.wireOp",EDGE,"E55"),sQuery(id+"F0.wireOp",EDGE,"E56"),sQuery(id+"F0.wireOp",EDGE,"E57"),sQuery(id+"F0.wireOp",EDGE,"E58"),sQuery(id+"F0.wireOp",EDGE,"E59"),sQuery(id+"F0.wireOp",EDGE,"E60"),sQuery(id+"F0.wireOp",EDGE,"E61"),sQuery(id+"F0.wireOp",EDGE,"E62"),sQuery(id+"F0.wireOp",EDGE,"E63"),sQuery(id+"F0.wireOp",EDGE,"E64"),sQuery(id+"F0.wireOp",EDGE,"E65"),sQuery(id+"F0.wireOp",EDGE,"E66"),sQuery(id+"F0.wireOp",EDGE,"E67"),sQuery(id+"F0.wireOp",EDGE,"E68"),sQuery(id+"F0.wireOp",EDGE,"E69"),sQuery(id+"F0.wireOp",EDGE,"E70"),sQuery(id+"F0.wireOp",EDGE,"E71"),sQuery(id+"F0.wireOp",EDGE,"E72"),sQuery(id+"F0.wireOp",EDGE,"E73"),sQuery(id+"F0.wireOp",EDGE,"E74"),sQuery(id+"F0.wireOp",EDGE,"E75"),sQuery(id+"F0.wireOp",EDGE,"E76"),sQuery(id+"F0.wireOp",EDGE,"E77"),sQuery(id+"F0.wireOp",EDGE,"E78"),sQuery(id+"F0.wireOp",EDGE,"E79"),sQuery(id+"F0.wireOp",EDGE,"E80"),sQuery(id+"F0.wireOp",EDGE,"E81"),sQuery(id+"F0.wireOp",EDGE,"E82"),sQuery(id+"F0.wireOp",EDGE,"E83"),sQuery(id+"F0.wireOp",EDGE,"E84"),sQuery(id+"F0.wireOp",EDGE,"E85"),sQuery(id+"F0.wireOp",EDGE,"E86"),sQuery(id+"F0.wireOp",EDGE,"E87"),sQuery(id+"F0.wireOp",EDGE,"E88"),sQuery(id+"F0.wireOp",EDGE,"E89"),sQuery(id+"F0.wireOp",EDGE,"E90"),sQuery(id+"F0.wireOp",EDGE,"E91"),sQuery(id+"F0.wireOp",EDGE,"E92"),sQuery(id+"F0.wireOp",EDGE,"E93"),sQuery(id+"F0.wireOp",EDGE,"E94"),sQuery(id+"F0.wireOp",EDGE,"E95"),sQuery(id+"F0.wireOp",EDGE,"E96"),sQuery(id+"F0.wireOp",EDGE,"E97"),sQuery(id+"F0.wireOp",EDGE,"E98"),sQuery(id+"F0.wireOp",EDGE,"E99"),sQuery(id+"F0.wireOp",EDGE,"E100"),sQuery(id+"F0.wireOp",EDGE,"E101"),sQuery(id+"F0.wireOp",EDGE,"E102"),sQuery(id+"F0.wireOp",EDGE,"E103"),sQuery(id+"F0.wireOp",EDGE,"E104"),sQuery(id+"F0.wireOp",EDGE,"E105"),sQuery(id+"F0.wireOp",EDGE,"E106"),sQuery(id+"F0.wireOp",EDGE,"E107"),sQuery(id+"F0.wireOp",EDGE,"E108"),sQuery(id+"F0.wireOp",EDGE,"E109"),sQuery(id+"F0.wireOp",EDGE,"E110"),sQuery(id+"F0.wireOp",EDGE,"E111"),sQuery(id+"F0.wireOp",EDGE,"E112"),sQuery(id+"F0.wireOp",EDGE,"E113"),sQuery(id+"F0.wireOp",EDGE,"E114"),sQuery(id+"F0.wireOp",EDGE,"E115"),sQuery(id+"F0.wireOp",EDGE,"E116"),sQuery(id+"F0.wireOp",EDGE,"E117"),sQuery(id+"F0.wireOp",EDGE,"E118"),sQuery(id+"F0.wireOp",EDGE,"E119"),sQuery(id+"F0.wireOp",EDGE,"E120"),sQuery(id+"F0.wireOp",EDGE,"E121"),sQuery(id+"F0.wireOp",EDGE,"E122"),sQuery(id+"F0.wireOp",EDGE,"E123"),sQuery(id+"F0.wireOp",EDGE,"E124"),sQuery(id+"F0.wireOp",EDGE,"E125"),sQuery(id+"F0.wireOp",EDGE,"E126"),sQuery(id+"F0.wireOp",EDGE,"E127"),sQuery(id+"F0.wireOp",EDGE,"E128"),sQuery(id+"F0.wireOp",EDGE,"E129"),sQuery(id+"F0.wireOp",EDGE,"E130"),sQuery(id+"F0.wireOp",EDGE,"E131"),sQuery(id+"F0.wireOp",EDGE,"E132"),sQuery(id+"F0.wireOp",EDGE,"E133"),sQuery(id+"F0.wireOp",EDGE,"E134"),sQuery(id+"F0.wireOp",EDGE,"E135"),sQuery(id+"F0.wireOp",EDGE,"E136"),sQuery(id+"F0.wireOp",EDGE,"E137"),sQuery(id+"F0.wireOp",EDGE,"E138"),sQuery(id+"F0.wireOp",EDGE,"E139"),sQuery(id+"F0.wireOp",EDGE,"E140"),sQuery(id+"F0.wireOp",EDGE,"E141"),sQuery(id+"F0.wireOp",EDGE,"E142"),sQuery(id+"F0.wireOp",EDGE,"E143"),sQuery(id+"F0.wireOp",EDGE,"E144"),sQuery(id+"F0.wireOp",EDGE,"E145"),sQuery(id+"F0.wireOp",EDGE,"E146"),sQuery(id+"F0.wireOp",EDGE,"E147"),sQuery(id+"F0.wireOp",EDGE,"E148"),sQuery(id+"F0.wireOp",EDGE,"E149"),sQuery(id+"F0.wireOp",EDGE,"E150"),sQuery(id+"F0.wireOp",EDGE,"E151"),sQuery(id+"F0.wireOp",EDGE,"E152"),sQuery(id+"F0.wireOp",EDGE,"E153"),sQuery(id+"F0.wireOp",EDGE,"E154"),sQuery(id+"F0.wireOp",EDGE,"E155"),sQuery(id+"F0.wireOp",EDGE,"E156"),sQuery(id+"F0.wireOp",EDGE,"E157"),sQuery(id+"F0.wireOp",EDGE,"E158"),sQuery(id+"F0.wireOp",EDGE,"E159"),sQuery(id+"F0.wireOp",EDGE,"E160"),sQuery(id+"F0.wireOp",EDGE,"E161"),sQuery(id+"F0.wireOp",EDGE,"E162"),sQuery(id+"F0.wireOp",EDGE,"E163"),sQuery(id+"F0.wireOp",EDGE,"E164"),sQuery(id+"F0.wireOp",EDGE,"E165"),sQuery(id+"F0.wireOp",EDGE,"E166"),sQuery(id+"F0.wireOp",EDGE,"E167"),sQuery(id+"F0.wireOp",EDGE,"E168"),sQuery(id+"F0.wireOp",EDGE,"E169"),sQuery(id+"F0.wireOp",EDGE,"E170"),sQuery(id+"F0.wireOp",EDGE,"E171"),sQuery(id+"F0.wireOp",EDGE,"E172"),sQuery(id+"F0.wireOp",EDGE,"E173"),sQuery(id+"F0.wireOp",EDGE,"E174"),sQuery(id+"F0.wireOp",EDGE,"E175"),sQuery(id+"F0.wireOp",EDGE,"E176"),sQuery(id+"F0.wireOp",EDGE,"E177"),sQuery(id+"F0.wireOp",EDGE,"E178"),sQuery(id+"F0.wireOp",EDGE,"E179"),sQuery(id+"F0.wireOp",EDGE,"E180"),sQuery(id+"F0.wireOp",EDGE,"E181"),sQuery(id+"F0.wireOp",EDGE,"E182"),sQuery(id+"F0.wireOp",EDGE,"E183"),sQuery(id+"F0.wireOp",EDGE,"E184"),sQuery(id+"F0.wireOp",EDGE,"E185"),sQuery(id+"F0.wireOp",EDGE,"E186"),sQuery(id+"F0.wireOp",EDGE,"E187"),sQuery(id+"F0.wireOp",EDGE,"E188")])],"isStart":true})]}),makeQuery(id+"F1.opExtrude","SWEPT_FACE",FACE,{"disambiguationData":[OSD([subQ0])]})],"blendedInto":[makeQuery(id+"F1.opExtrude","SWEPT_FACE",FACE,{"disambiguationData":[OSD([subQ0])]})]});}
            fillet(context, id + "F10", {"entities" : qUnion([Q0]), "radius" : 5 * mm, "tangentPropagation" : true, "allowEdgeOverflow" : false});
        }
        {
            var Q0;
            Q0=makeQuery(id+"F1.opExtrude","CAP_FACE",FACE,{"disambiguationData":[OSD([sQuery(id+"F0.wireOp",EDGE,"E0"),sQuery(id+"F0.wireOp",EDGE,"E1"),sQuery(id+"F0.wireOp",EDGE,"E2"),sQuery(id+"F0.wireOp",EDGE,"E3"),sQuery(id+"F0.wireOp",EDGE,"E4"),sQuery(id+"F0.wireOp",EDGE,"E5"),sQuery(id+"F0.wireOp",EDGE,"E6"),sQuery(id+"F0.wireOp",EDGE,"E7"),sQuery(id+"F0.wireOp",EDGE,"E8"),sQuery(id+"F0.wireOp",EDGE,"E9"),sQuery(id+"F0.wireOp",EDGE,"E10"),sQuery(id+"F0.wireOp",EDGE,"E11"),sQuery(id+"F0.wireOp",EDGE,"E12"),sQuery(id+"F0.wireOp",EDGE,"E13"),sQuery(id+"F0.wireOp",EDGE,"E14"),sQuery(id+"F0.wireOp",EDGE,"E15"),sQuery(id+"F0.wireOp",EDGE,"E16"),sQuery(id+"F0.wireOp",EDGE,"E17"),sQuery(id+"F0.wireOp",EDGE,"E18"),sQuery(id+"F0.wireOp",EDGE,"E19"),sQuery(id+"F0.wireOp",EDGE,"E20"),sQuery(id+"F0.wireOp",EDGE,"E21"),sQuery(id+"F0.wireOp",EDGE,"E22"),sQuery(id+"F0.wireOp",EDGE,"E23"),sQuery(id+"F0.wireOp",EDGE,"E24"),sQuery(id+"F0.wireOp",EDGE,"E25"),sQuery(id+"F0.wireOp",EDGE,"E26"),sQuery(id+"F0.wireOp",EDGE,"E27"),sQuery(id+"F0.wireOp",EDGE,"E28"),sQuery(id+"F0.wireOp",EDGE,"E29"),sQuery(id+"F0.wireOp",EDGE,"E30"),sQuery(id+"F0.wireOp",EDGE,"E31"),sQuery(id+"F0.wireOp",EDGE,"E32"),sQuery(id+"F0.wireOp",EDGE,"E33"),sQuery(id+"F0.wireOp",EDGE,"E34"),sQuery(id+"F0.wireOp",EDGE,"E35"),sQuery(id+"F0.wireOp",EDGE,"E36"),sQuery(id+"F0.wireOp",EDGE,"E37"),sQuery(id+"F0.wireOp",EDGE,"E38"),sQuery(id+"F0.wireOp",EDGE,"E39"),sQuery(id+"F0.wireOp",EDGE,"E40"),sQuery(id+"F0.wireOp",EDGE,"E41"),sQuery(id+"F0.wireOp",EDGE,"E42"),sQuery(id+"F0.wireOp",EDGE,"E43"),sQuery(id+"F0.wireOp",EDGE,"E44"),sQuery(id+"F0.wireOp",EDGE,"E45"),sQuery(id+"F0.wireOp",EDGE,"E46"),sQuery(id+"F0.wireOp",EDGE,"E47"),sQuery(id+"F0.wireOp",EDGE,"E48"),sQuery(id+"F0.wireOp",EDGE,"E49"),sQuery(id+"F0.wireOp",EDGE,"E50"),sQuery(id+"F0.wireOp",EDGE,"E51"),sQuery(id+"F0.wireOp",EDGE,"E52"),sQuery(id+"F0.wireOp",EDGE,"E53"),sQuery(id+"F0.wireOp",EDGE,"E54"),sQuery(id+"F0.wireOp",EDGE,"E55"),sQuery(id+"F0.wireOp",EDGE,"E56"),sQuery(id+"F0.wireOp",EDGE,"E57"),sQuery(id+"F0.wireOp",EDGE,"E58"),sQuery(id+"F0.wireOp",EDGE,"E59"),sQuery(id+"F0.wireOp",EDGE,"E60"),sQuery(id+"F0.wireOp",EDGE,"E61"),sQuery(id+"F0.wireOp",EDGE,"E62"),sQuery(id+"F0.wireOp",EDGE,"E63"),sQuery(id+"F0.wireOp",EDGE,"E64"),sQuery(id+"F0.wireOp",EDGE,"E65"),sQuery(id+"F0.wireOp",EDGE,"E66"),sQuery(id+"F0.wireOp",EDGE,"E67"),sQuery(id+"F0.wireOp",EDGE,"E68"),sQuery(id+"F0.wireOp",EDGE,"E69"),sQuery(id+"F0.wireOp",EDGE,"E70"),sQuery(id+"F0.wireOp",EDGE,"E71"),sQuery(id+"F0.wireOp",EDGE,"E72"),sQuery(id+"F0.wireOp",EDGE,"E73"),sQuery(id+"F0.wireOp",EDGE,"E74"),sQuery(id+"F0.wireOp",EDGE,"E75"),sQuery(id+"F0.wireOp",EDGE,"E76"),sQuery(id+"F0.wireOp",EDGE,"E77"),sQuery(id+"F0.wireOp",EDGE,"E78"),sQuery(id+"F0.wireOp",EDGE,"E79"),sQuery(id+"F0.wireOp",EDGE,"E80"),sQuery(id+"F0.wireOp",EDGE,"E81"),sQuery(id+"F0.wireOp",EDGE,"E82"),sQuery(id+"F0.wireOp",EDGE,"E83"),sQuery(id+"F0.wireOp",EDGE,"E84"),sQuery(id+"F0.wireOp",EDGE,"E85"),sQuery(id+"F0.wireOp",EDGE,"E86"),sQuery(id+"F0.wireOp",EDGE,"E87"),sQuery(id+"F0.wireOp",EDGE,"E88"),sQuery(id+"F0.wireOp",EDGE,"E89"),sQuery(id+"F0.wireOp",EDGE,"E90"),sQuery(id+"F0.wireOp",EDGE,"E91"),sQuery(id+"F0.wireOp",EDGE,"E92"),sQuery(id+"F0.wireOp",EDGE,"E93"),sQuery(id+"F0.wireOp",EDGE,"E94"),sQuery(id+"F0.wireOp",EDGE,"E95"),sQuery(id+"F0.wireOp",EDGE,"E96"),sQuery(id+"F0.wireOp",EDGE,"E97"),sQuery(id+"F0.wireOp",EDGE,"E98"),sQuery(id+"F0.wireOp",EDGE,"E99"),sQuery(id+"F0.wireOp",EDGE,"E100"),sQuery(id+"F0.wireOp",EDGE,"E101"),sQuery(id+"F0.wireOp",EDGE,"E102"),sQuery(id+"F0.wireOp",EDGE,"E103"),sQuery(id+"F0.wireOp",EDGE,"E104"),sQuery(id+"F0.wireOp",EDGE,"E105"),sQuery(id+"F0.wireOp",EDGE,"E106"),sQuery(id+"F0.wireOp",EDGE,"E107"),sQuery(id+"F0.wireOp",EDGE,"E108"),sQuery(id+"F0.wireOp",EDGE,"E109"),sQuery(id+"F0.wireOp",EDGE,"E110"),sQuery(id+"F0.wireOp",EDGE,"E111"),sQuery(id+"F0.wireOp",EDGE,"E112"),sQuery(id+"F0.wireOp",EDGE,"E113"),sQuery(id+"F0.wireOp",EDGE,"E114"),sQuery(id+"F0.wireOp",EDGE,"E115"),sQuery(id+"F0.wireOp",EDGE,"E116"),sQuery(id+"F0.wireOp",EDGE,"E117"),sQuery(id+"F0.wireOp",EDGE,"E118"),sQuery(id+"F0.wireOp",EDGE,"E119"),sQuery(id+"F0.wireOp",EDGE,"E120"),sQuery(id+"F0.wireOp",EDGE,"E121"),sQuery(id+"F0.wireOp",EDGE,"E122"),sQuery(id+"F0.wireOp",EDGE,"E123"),sQuery(id+"F0.wireOp",EDGE,"E124"),sQuery(id+"F0.wireOp",EDGE,"E125"),sQuery(id+"F0.wireOp",EDGE,"E126"),sQuery(id+"F0.wireOp",EDGE,"E127"),sQuery(id+"F0.wireOp",EDGE,"E128"),sQuery(id+"F0.wireOp",EDGE,"E129"),sQuery(id+"F0.wireOp",EDGE,"E130"),sQuery(id+"F0.wireOp",EDGE,"E131"),sQuery(id+"F0.wireOp",EDGE,"E132"),sQuery(id+"F0.wireOp",EDGE,"E133"),sQuery(id+"F0.wireOp",EDGE,"E134"),sQuery(id+"F0.wireOp",EDGE,"E135"),sQuery(id+"F0.wireOp",EDGE,"E136"),sQuery(id+"F0.wireOp",EDGE,"E137"),sQuery(id+"F0.wireOp",EDGE,"E138"),sQuery(id+"F0.wireOp",EDGE,"E139"),sQuery(id+"F0.wireOp",EDGE,"E140"),sQuery(id+"F0.wireOp",EDGE,"E141"),sQuery(id+"F0.wireOp",EDGE,"E142"),sQuery(id+"F0.wireOp",EDGE,"E143"),sQuery(id+"F0.wireOp",EDGE,"E144"),sQuery(id+"F0.wireOp",EDGE,"E145"),sQuery(id+"F0.wireOp",EDGE,"E146"),sQuery(id+"F0.wireOp",EDGE,"E147"),sQuery(id+"F0.wireOp",EDGE,"E148"),sQuery(id+"F0.wireOp",EDGE,"E149"),sQuery(id+"F0.wireOp",EDGE,"E150"),sQuery(id+"F0.wireOp",EDGE,"E151"),sQuery(id+"F0.wireOp",EDGE,"E152"),sQuery(id+"F0.wireOp",EDGE,"E153"),sQuery(id+"F0.wireOp",EDGE,"E154"),sQuery(id+"F0.wireOp",EDGE,"E155"),sQuery(id+"F0.wireOp",EDGE,"E156"),sQuery(id+"F0.wireOp",EDGE,"E157"),sQuery(id+"F0.wireOp",EDGE,"E158"),sQuery(id+"F0.wireOp",EDGE,"E159"),sQuery(id+"F0.wireOp",EDGE,"E160"),sQuery(id+"F0.wireOp",EDGE,"E161"),sQuery(id+"F0.wireOp",EDGE,"E162"),sQuery(id+"F0.wireOp",EDGE,"E163"),sQuery(id+"F0.wireOp",EDGE,"E164"),sQuery(id+"F0.wireOp",EDGE,"E165"),sQuery(id+"F0.wireOp",EDGE,"E166"),sQuery(id+"F0.wireOp",EDGE,"E167"),sQuery(id+"F0.wireOp",EDGE,"E168"),sQuery(id+"F0.wireOp",EDGE,"E169"),sQuery(id+"F0.wireOp",EDGE,"E170"),sQuery(id+"F0.wireOp",EDGE,"E171"),sQuery(id+"F0.wireOp",EDGE,"E172"),sQuery(id+"F0.wireOp",EDGE,"E173"),sQuery(id+"F0.wireOp",EDGE,"E174"),sQuery(id+"F0.wireOp",EDGE,"E175"),sQuery(id+"F0.wireOp",EDGE,"E176"),sQuery(id+"F0.wireOp",EDGE,"E177"),sQuery(id+"F0.wireOp",EDGE,"E178"),sQuery(id+"F0.wireOp",EDGE,"E179"),sQuery(id+"F0.wireOp",EDGE,"E180"),sQuery(id+"F0.wireOp",EDGE,"E181"),sQuery(id+"F0.wireOp",EDGE,"E182"),sQuery(id+"F0.wireOp",EDGE,"E183"),sQuery(id+"F0.wireOp",EDGE,"E184"),sQuery(id+"F0.wireOp",EDGE,"E185"),sQuery(id+"F0.wireOp",EDGE,"E186"),sQuery(id+"F0.wireOp",EDGE,"E187"),sQuery(id+"F0.wireOp",EDGE,"E188")])],"isStart":false});
            var sketch = newSketch(context, id + "F11", { "sketchPlane" : qUnion([Q0])});
            skLineSegment(sketch, "E248", {"start": v(-287.8, 77.45) * mm, "end": v(-287.8, 76.93) * mm});
            skLineSegment(sketch, "E249", {"start": v(-287.8, 76.93) * mm, "end": v(-174.98, 75.72) * mm});
            skLineSegment(sketch, "E250", {"start": v(-174.98, 75.72) * mm, "end": v(-174.98, 76.3) * mm});
            skLineSegment(sketch, "E251", {"start": v(-174.98, 76.3) * mm, "end": v(-287.8, 77.45) * mm});
            skLineSegment(sketch, "E252", {"start": v(-282.65, 70.2) * mm, "end": v(-282.66, 69.75) * mm});
            skLineSegment(sketch, "E253", {"start": v(-282.66, 69.75) * mm, "end": v(-172.65, 68.57) * mm});
            skLineSegment(sketch, "E254", {"start": v(-172.65, 68.57) * mm, "end": v(-172.65, 69.12) * mm});
            skLineSegment(sketch, "E255", {"start": v(-172.65, 69.12) * mm, "end": v(-282.65, 70.2) * mm});
            skLineSegment(sketch, "E256", {"start": v(-165.28, 43.76) * mm, "end": v(-163.93, 56.06) * mm});
            skLineSegment(sketch, "E257", {"start": v(-163.93, 56.06) * mm, "end": v(-141.83, 56.06) * mm});
            skLineSegment(sketch, "E258", {"start": v(-141.83, 56.06) * mm, "end": v(-140.58, 43.12) * mm});
            skLineSegment(sketch, "E259", {"start": v(-140.58, 43.12) * mm, "end": v(-141.9, 43) * mm});
            skLineSegment(sketch, "E260", {"start": v(-141.9, 43) * mm, "end": v(-141.73, 41.17) * mm});
            skLineSegment(sketch, "E261", {"start": v(-141.73, 41.17) * mm, "end": v(-164.5, 41.17) * mm});
            skLineSegment(sketch, "E262", {"start": v(-164.5, 41.17) * mm, "end": v(-164.07, 43.57) * mm});
            skLineSegment(sketch, "E263", {"start": v(-164.07, 43.57) * mm, "end": v(-165.28, 43.76) * mm});
            skLineSegment(sketch, "E264", {"start": v(-96.55, 43.76) * mm, "end": v(-95.5, 43.76) * mm});
            skLineSegment(sketch, "E265", {"start": v(-95.5, 43.76) * mm, "end": v(-95.82, 41.34) * mm});
            skLineSegment(sketch, "E266", {"start": v(-95.82, 41.34) * mm, "end": v(-73.11, 41.18) * mm});
            skLineSegment(sketch, "E267", {"start": v(-73.11, 41.18) * mm, "end": v(-73.11, 43.48) * mm});
            skLineSegment(sketch, "E268", {"start": v(-73.11, 43.48) * mm, "end": v(-71.95, 43.52) * mm});
            skLineSegment(sketch, "E269", {"start": v(-71.95, 43.52) * mm, "end": v(-73.11, 56.32) * mm});
            skLineSegment(sketch, "E270", {"start": v(-73.11, 56.32) * mm, "end": v(-95.27, 56.32) * mm});
            skLineSegment(sketch, "E271", {"start": v(-95.27, 56.32) * mm, "end": v(-96.55, 43.76) * mm});
            skLineSegment(sketch, "E272", {"start": v(-114.7, 62.95) * mm, "end": v(-114.7, 58.57) * mm});
            skLineSegment(sketch, "E273", {"start": v(-114.7, 58.57) * mm, "end": v(-105.63, 58.57) * mm});
            skLineSegment(sketch, "E274", {"start": v(-105.63, 58.57) * mm, "end": v(-105.63, 62.75) * mm});
            skLineSegment(sketch, "E275", {"start": v(-105.63, 62.75) * mm, "end": v(-114.7, 62.95) * mm});
            skLineSegment(sketch, "E276", {"start": v(-266.75, 90.67) * mm, "end": v(-267.01, 89.94) * mm});
            skLineSegment(sketch, "E277", {"start": v(-267.01, 89.94) * mm, "end": v(-228.27, 83.56) * mm});
            skLineSegment(sketch, "E278", {"start": v(-228.27, 83.56) * mm, "end": v(-225.12, 83.52) * mm});
            skLineSegment(sketch, "E279", {"start": v(-225.12, 83.52) * mm, "end": v(-266.75, 90.67) * mm});
            skLineSegment(sketch, "E280", {"start": v(-215.33, 81.45) * mm, "end": v(-211.88, 81.41) * mm});
            skLineSegment(sketch, "E281", {"start": v(-211.88, 81.41) * mm, "end": v(-181.8, 76.45) * mm});
            skLineSegment(sketch, "E282", {"start": v(-181.8, 76.45) * mm, "end": v(-185.36, 76.5) * mm});
            skLineSegment(sketch, "E283", {"start": v(-185.36, 76.5) * mm, "end": v(-215.33, 81.45) * mm});
            skLineSegment(sketch, "E284", {"start": v(-178.76, 75.41) * mm, "end": v(-177.01, 75.58) * mm});
            skLineSegment(sketch, "E285", {"start": v(-177.01, 75.58) * mm, "end": v(-95.82, 62.57) * mm});
            skLineSegment(sketch, "E286", {"start": v(-95.82, 62.57) * mm, "end": v(-95.82, 62.04) * mm});
            skLineSegment(sketch, "E287", {"start": v(-95.82, 62.04) * mm, "end": v(-178.76, 75.41) * mm});
            skLineSegment(sketch, "E288", {"start": v(-95.82, 62.57) * mm, "end": v(-35.38, 53.4) * mm});
            skLineSegment(sketch, "E289", {"start": v(-35.38, 53.4) * mm, "end": v(-35.38, 53.03) * mm});
            skLineSegment(sketch, "E290", {"start": v(-35.38, 53.03) * mm, "end": v(-95.82, 62.04) * mm});
            skLineSegment(sketch, "E291", {"start": v(-218.26, 67.1) * mm, "end": v(-209.36, 67.1) * mm});
            skLineSegment(sketch, "E292", {"start": v(-209.36, 67.1) * mm, "end": v(-209.36, 62.78) * mm});
            skLineSegment(sketch, "E293", {"start": v(-209.36, 62.78) * mm, "end": v(-218.45, 62.57) * mm});
            skLineSegment(sketch, "E294", {"start": v(-218.45, 62.57) * mm, "end": v(-218.26, 67.1) * mm});
            skLineSegment(sketch, "E295", {"start": v(-200.62, 75.41) * mm, "end": v(-197.5, 75.41) * mm});
            skLineSegment(sketch, "E296", {"start": v(-197.5, 75.41) * mm, "end": v(-197.5, 72.02) * mm});
            skLineSegment(sketch, "E297", {"start": v(-197.5, 72.02) * mm, "end": v(-200.66, 72.05) * mm});
            skLineSegment(sketch, "E298", {"start": v(-200.66, 72.05) * mm, "end": v(-200.62, 75.41) * mm});
            skLineSegment(sketch, "E299", {"start": v(-137.37, 107.83) * mm, "end": v(-134.04, 107.83) * mm});
            skLineSegment(sketch, "E300", {"start": v(-134.04, 107.83) * mm, "end": v(-134.04, 104.4) * mm});
            skLineSegment(sketch, "E301", {"start": v(-134.04, 104.4) * mm, "end": v(-137.37, 104.4) * mm});
            skLineSegment(sketch, "E302", {"start": v(-137.37, 104.4) * mm, "end": v(-137.37, 107.83) * mm});
            skLineSegment(sketch, "E303", {"start": v(-163.33, 111.87) * mm, "end": v(-163.38, 112.38) * mm});
            skLineSegment(sketch, "E304", {"start": v(-163.38, 112.38) * mm, "end": v(-163.93, 112.38) * mm});
            skLineSegment(sketch, "E305", {"start": v(-163.93, 112.38) * mm, "end": v(-163.93, 110.2) * mm});
            skLineSegment(sketch, "E306", {"start": v(-163.93, 110.2) * mm, "end": v(-163.4, 110.2) * mm});
            skLineSegment(sketch, "E307", {"start": v(-163.4, 110.2) * mm, "end": v(-163.4, 110.86) * mm});
            skLineSegment(sketch, "E308", {"start": v(-163.4, 110.86) * mm, "end": v(-162.89, 110.86) * mm});
            skLineSegment(sketch, "E309", {"start": v(-162.89, 110.86) * mm, "end": v(-162.9, 110.2) * mm});
            skLineSegment(sketch, "E310", {"start": v(-162.9, 110.2) * mm, "end": v(-162.36, 110.2) * mm});
            skLineSegment(sketch, "E311", {"start": v(-162.36, 110.2) * mm, "end": v(-162.36, 112.35) * mm});
            skLineSegment(sketch, "E312", {"start": v(-162.36, 112.35) * mm, "end": v(-162.9, 112.35) * mm});
            skLineSegment(sketch, "E313", {"start": v(-162.9, 112.35) * mm, "end": v(-162.85, 111.78) * mm});
            skLineSegment(sketch, "E314", {"start": v(-162.85, 111.78) * mm, "end": v(-163.33, 111.87) * mm});
            skLineSegment(sketch, "E315", {"start": v(-104.43, 108.65) * mm, "end": v(-102.76, 108.65) * mm});
            skLineSegment(sketch, "E316", {"start": v(-102.76, 108.65) * mm, "end": v(-102.58, 106.8) * mm});
            skLineSegment(sketch, "E317", {"start": v(-102.58, 106.8) * mm, "end": v(-104.28, 106.8) * mm});
            skLineSegment(sketch, "E318", {"start": v(-104.28, 106.8) * mm, "end": v(-104.43, 108.65) * mm});
            skLineSegment(sketch, "E319", {"start": v(-74.14, 105.1) * mm, "end": v(-74.14, 105.65) * mm});
            skLineSegment(sketch, "E320", {"start": v(-74.14, 105.65) * mm, "end": v(-74.78, 105.66) * mm});
            skLineSegment(sketch, "E321", {"start": v(-74.78, 105.66) * mm, "end": v(-74.8, 103.56) * mm});
            skLineSegment(sketch, "E322", {"start": v(-74.8, 103.56) * mm, "end": v(-74.16, 103.56) * mm});
            skLineSegment(sketch, "E323", {"start": v(-74.16, 103.56) * mm, "end": v(-74.16, 104.23) * mm});
            skLineSegment(sketch, "E324", {"start": v(-74.16, 104.23) * mm, "end": v(-73.7, 104.23) * mm});
            skLineSegment(sketch, "E325", {"start": v(-73.7, 104.23) * mm, "end": v(-73.7, 103.56) * mm});
            skLineSegment(sketch, "E326", {"start": v(-73.7, 103.56) * mm, "end": v(-73.11, 103.56) * mm});
            skLineSegment(sketch, "E327", {"start": v(-73.11, 103.56) * mm, "end": v(-73.11, 105.67) * mm});
            skLineSegment(sketch, "E328", {"start": v(-73.11, 105.67) * mm, "end": v(-73.69, 105.67) * mm});
            skLineSegment(sketch, "E329", {"start": v(-73.69, 105.67) * mm, "end": v(-73.69, 105.09) * mm});
            skLineSegment(sketch, "E330", {"start": v(-73.69, 105.09) * mm, "end": v(-74.14, 105.1) * mm});
            skLineSegment(sketch, "E331", {"start": v(-24.1, 90.8) * mm, "end": v(-24.73, 90.08) * mm});
            skLineSegment(sketch, "E332", {"start": v(-24.73, 90.08) * mm, "end": v(-25.45, 90.72) * mm});
            skLineSegment(sketch, "E333", {"start": v(-25.45, 90.72) * mm, "end": v(-25.45, 94.14) * mm});
            skLineSegment(sketch, "E334", {"start": v(-25.45, 94.14) * mm, "end": v(-24.6, 94.92) * mm});
            skLineSegment(sketch, "E335", {"start": v(-24.6, 94.92) * mm, "end": v(-20.44, 94.92) * mm});
            skLineSegment(sketch, "E336", {"start": v(-20.44, 94.92) * mm, "end": v(-19.72, 94.08) * mm});
            skLineSegment(sketch, "E337", {"start": v(-19.72, 94.08) * mm, "end": v(-19.72, 90.67) * mm});
            skLineSegment(sketch, "E338", {"start": v(-19.72, 90.67) * mm, "end": v(-20.4, 89.94) * mm});
            skLineSegment(sketch, "E339", {"start": v(-20.4, 89.94) * mm, "end": v(-23, 89.96) * mm});
            skLineSegment(sketch, "E340", {"start": v(-23, 89.96) * mm, "end": v(-23.2, 90.14) * mm});
            skLineSegment(sketch, "E341", {"start": v(-23.2, 90.14) * mm, "end": v(-23.2, 91.95) * mm});
            skLineSegment(sketch, "E342", {"start": v(-23.2, 91.95) * mm, "end": v(-22.35, 91.95) * mm});
            skLineSegment(sketch, "E343", {"start": v(-22.35, 91.95) * mm, "end": v(-22.35, 90.95) * mm});
            skLineSegment(sketch, "E344", {"start": v(-22.35, 90.95) * mm, "end": v(-20.91, 90.93) * mm});
            skLineSegment(sketch, "E345", {"start": v(-20.91, 90.93) * mm, "end": v(-20.74, 91.07) * mm});
            skLineSegment(sketch, "E346", {"start": v(-20.74, 91.07) * mm, "end": v(-20.74, 93.44) * mm});
            skLineSegment(sketch, "E347", {"start": v(-20.74, 93.44) * mm, "end": v(-20.98, 93.85) * mm});
            skLineSegment(sketch, "E348", {"start": v(-20.98, 93.85) * mm, "end": v(-24.02, 93.88) * mm});
            skLineSegment(sketch, "E349", {"start": v(-24.02, 93.88) * mm, "end": v(-24.41, 93.5) * mm});
            skLineSegment(sketch, "E350", {"start": v(-24.41, 93.5) * mm, "end": v(-24.53, 91.4) * mm});
            skLineSegment(sketch, "E351", {"start": v(-24.53, 91.4) * mm, "end": v(-24.1, 90.8) * mm});
            skLineSegment(sketch, "E352", {"start": v(-227, 97.95) * mm, "end": v(-227, 97.2) * mm});
            skLineSegment(sketch, "E353", {"start": v(-227, 97.2) * mm, "end": v(-105.3, 89.5) * mm});
            skLineSegment(sketch, "E354", {"start": v(-105.3, 89.5) * mm, "end": v(-105.26, 90.1) * mm});
            skLineSegment(sketch, "E355", {"start": v(-105.26, 90.1) * mm, "end": v(-227, 97.95) * mm});
            skLineSegment(sketch, "E356", {"start": v(-246.23, 93.13) * mm, "end": v(-246.23, 92.6) * mm});
            skLineSegment(sketch, "E357", {"start": v(-246.23, 92.6) * mm, "end": v(-123.36, 84.76) * mm});
            skLineSegment(sketch, "E358", {"start": v(-123.36, 84.76) * mm, "end": v(-123.36, 85.32) * mm});
            skLineSegment(sketch, "E359", {"start": v(-123.36, 85.32) * mm, "end": v(-246.23, 93.13) * mm});
            skLineSegment(sketch, "E360", {"start": v(-228.88, 45.38) * mm, "end": v(-228.49, 45.38) * mm});
            skLineSegment(sketch, "E361", {"start": v(-228.49, 45.38) * mm, "end": v(-228.53, 45.8) * mm});
            skLineSegment(sketch, "E362", {"start": v(-228.53, 45.8) * mm, "end": v(-227.83, 45.8) * mm});
            skLineSegment(sketch, "E363", {"start": v(-227.83, 45.8) * mm, "end": v(-227.87, 43.8) * mm});
            skLineSegment(sketch, "E364", {"start": v(-227.87, 43.8) * mm, "end": v(-228.4, 43.8) * mm});
            skLineSegment(sketch, "E365", {"start": v(-228.4, 43.8) * mm, "end": v(-228.47, 44.49) * mm});
            skLineSegment(sketch, "E366", {"start": v(-228.47, 44.49) * mm, "end": v(-228.83, 44.49) * mm});
            skLineSegment(sketch, "E367", {"start": v(-228.83, 44.49) * mm, "end": v(-228.83, 43.8) * mm});
            skLineSegment(sketch, "E368", {"start": v(-228.83, 43.8) * mm, "end": v(-229.5, 43.8) * mm});
            skLineSegment(sketch, "E369", {"start": v(-229.5, 43.8) * mm, "end": v(-229.5, 45.86) * mm});
            skLineSegment(sketch, "E370", {"start": v(-229.5, 45.86) * mm, "end": v(-228.92, 45.86) * mm});
            skLineSegment(sketch, "E371", {"start": v(-228.92, 45.86) * mm, "end": v(-228.88, 45.38) * mm});
            skLineSegment(sketch, "E372", {"start": v(-63.74, 70.94) * mm, "end": v(-63.84, 70.24) * mm});
            skLineSegment(sketch, "E373", {"start": v(-63.74, 70.94) * mm, "end": v(-58.84, 70.04) * mm});
            skLineSegment(sketch, "E374", {"start": v(-58.84, 70.04) * mm, "end": v(-58.84, 69.55) * mm});
            skLineSegment(sketch, "E375", {"start": v(-58.84, 69.55) * mm, "end": v(-63.84, 70.24) * mm});
            skLineSegment(sketch, "E376", {"start": v(-80.54, 72.67) * mm, "end": v(-75.47, 72.07) * mm});
            skLineSegment(sketch, "E377", {"start": v(-75.47, 72.07) * mm, "end": v(-75.53, 71.55) * mm});
            skLineSegment(sketch, "E378", {"start": v(-75.53, 71.55) * mm, "end": v(-80.54, 72.13) * mm});
            skLineSegment(sketch, "E379", {"start": v(-80.54, 72.13) * mm, "end": v(-80.54, 72.67) * mm});
            skLineSegment(sketch, "E380", {"start": v(-96.56, 74.45) * mm, "end": v(-91.54, 73.78) * mm});
            skLineSegment(sketch, "E381", {"start": v(-91.54, 73.78) * mm, "end": v(-91.54, 73.26) * mm});
            skLineSegment(sketch, "E382", {"start": v(-91.54, 73.26) * mm, "end": v(-96.61, 73.95) * mm});
            skLineSegment(sketch, "E383", {"start": v(-96.61, 73.95) * mm, "end": v(-96.56, 74.45) * mm});
            skLineSegment(sketch, "E384", {"start": v(-89.9, 86.46) * mm, "end": v(-94.9, 87.12) * mm});
            skLineSegment(sketch, "E385", {"start": v(-94.9, 87.12) * mm, "end": v(-94.96, 86.57) * mm});
            skLineSegment(sketch, "E386", {"start": v(-94.96, 86.57) * mm, "end": v(-89.9, 85.9) * mm});
            skLineSegment(sketch, "E387", {"start": v(-89.9, 85.9) * mm, "end": v(-89.9, 86.46) * mm});
            skLineSegment(sketch, "E388", {"start": v(-62.13, 83.43) * mm, "end": v(-57.18, 82.74) * mm});
            skLineSegment(sketch, "E389", {"start": v(-57.18, 82.74) * mm, "end": v(-57.18, 82.22) * mm});
            skLineSegment(sketch, "E390", {"start": v(-57.18, 82.22) * mm, "end": v(-62.22, 82.8) * mm});
            skLineSegment(sketch, "E391", {"start": v(-62.22, 82.8) * mm, "end": v(-62.13, 83.43) * mm});
            skLineSegment(sketch, "E392", {"start": v(-78.6, 85.39) * mm, "end": v(-73.8, 84.69) * mm});
            skLineSegment(sketch, "E393", {"start": v(-73.8, 84.69) * mm, "end": v(-73.87, 84.15) * mm});
            skLineSegment(sketch, "E394", {"start": v(-73.87, 84.15) * mm, "end": v(-78.83, 84.88) * mm});
            skLineSegment(sketch, "E395", {"start": v(-78.83, 84.88) * mm, "end": v(-78.6, 85.39) * mm});
            skLineSegment(sketch, "E396", {"start": v(-228.27, 83.56) * mm, "end": v(-281.42, 83.56) * mm});
            skLineSegment(sketch, "E397", {"start": v(-281.42, 83.56) * mm, "end": v(-281.42, 81.47) * mm});
            skLineSegment(sketch, "E398", {"start": v(-281.42, 81.47) * mm, "end": v(-215.33, 81.45) * mm});
            skLineSegment(sketch, "E399", {"start": v(-179.1, 81.45) * mm, "end": v(-179.1, 82.37) * mm});
            skLineSegment(sketch, "E400", {"start": v(-179.1, 82.37) * mm, "end": v(-156.58, 82.37) * mm});
            skLineSegment(sketch, "E401", {"start": v(-156.58, 82.37) * mm, "end": v(-156.58, 82.87) * mm});
            skLineSegment(sketch, "E402", {"start": v(-156.58, 82.87) * mm, "end": v(-178.85, 82.87) * mm});
            skLineSegment(sketch, "E403", {"start": v(-178.85, 82.87) * mm, "end": v(-178.85, 83.56) * mm});
            skLineSegment(sketch, "E404", {"start": v(-178.85, 83.56) * mm, "end": v(-228.27, 83.56) * mm});
            skSolve(sketch);
        }
        {
            var Q0;
            Q0 = qSketchRegion(id + "F11", true);
            extrude(context, id + "F12", {"entities" : qUnion([Q0]), "operationType" : NewBodyOperationType.REMOVE, "oppositeDirection" : true, "depth" : 2.1 * mm, "offsetDistance" : 25 * mm});
        }
        {
            var Q0;
            Q0=makeQuery(id+"F1.opExtrude","CAP_FACE",FACE,{"disambiguationData":[OSD([sQuery(id+"F0.wireOp",EDGE,"E0"),sQuery(id+"F0.wireOp",EDGE,"E1"),sQuery(id+"F0.wireOp",EDGE,"E2"),sQuery(id+"F0.wireOp",EDGE,"E3"),sQuery(id+"F0.wireOp",EDGE,"E4"),sQuery(id+"F0.wireOp",EDGE,"E5"),sQuery(id+"F0.wireOp",EDGE,"E6"),sQuery(id+"F0.wireOp",EDGE,"E7"),sQuery(id+"F0.wireOp",EDGE,"E8"),sQuery(id+"F0.wireOp",EDGE,"E9"),sQuery(id+"F0.wireOp",EDGE,"E10"),sQuery(id+"F0.wireOp",EDGE,"E11"),sQuery(id+"F0.wireOp",EDGE,"E12"),sQuery(id+"F0.wireOp",EDGE,"E13"),sQuery(id+"F0.wireOp",EDGE,"E14"),sQuery(id+"F0.wireOp",EDGE,"E15"),sQuery(id+"F0.wireOp",EDGE,"E16"),sQuery(id+"F0.wireOp",EDGE,"E17"),sQuery(id+"F0.wireOp",EDGE,"E18"),sQuery(id+"F0.wireOp",EDGE,"E19"),sQuery(id+"F0.wireOp",EDGE,"E20"),sQuery(id+"F0.wireOp",EDGE,"E21"),sQuery(id+"F0.wireOp",EDGE,"E22"),sQuery(id+"F0.wireOp",EDGE,"E23"),sQuery(id+"F0.wireOp",EDGE,"E24"),sQuery(id+"F0.wireOp",EDGE,"E25"),sQuery(id+"F0.wireOp",EDGE,"E26"),sQuery(id+"F0.wireOp",EDGE,"E27"),sQuery(id+"F0.wireOp",EDGE,"E28"),sQuery(id+"F0.wireOp",EDGE,"E29"),sQuery(id+"F0.wireOp",EDGE,"E30"),sQuery(id+"F0.wireOp",EDGE,"E31"),sQuery(id+"F0.wireOp",EDGE,"E32"),sQuery(id+"F0.wireOp",EDGE,"E33"),sQuery(id+"F0.wireOp",EDGE,"E34"),sQuery(id+"F0.wireOp",EDGE,"E35"),sQuery(id+"F0.wireOp",EDGE,"E36"),sQuery(id+"F0.wireOp",EDGE,"E37"),sQuery(id+"F0.wireOp",EDGE,"E38"),sQuery(id+"F0.wireOp",EDGE,"E39"),sQuery(id+"F0.wireOp",EDGE,"E40"),sQuery(id+"F0.wireOp",EDGE,"E41"),sQuery(id+"F0.wireOp",EDGE,"E42"),sQuery(id+"F0.wireOp",EDGE,"E43"),sQuery(id+"F0.wireOp",EDGE,"E44"),sQuery(id+"F0.wireOp",EDGE,"E45"),sQuery(id+"F0.wireOp",EDGE,"E46"),sQuery(id+"F0.wireOp",EDGE,"E47"),sQuery(id+"F0.wireOp",EDGE,"E48"),sQuery(id+"F0.wireOp",EDGE,"E49"),sQuery(id+"F0.wireOp",EDGE,"E50"),sQuery(id+"F0.wireOp",EDGE,"E51"),sQuery(id+"F0.wireOp",EDGE,"E52"),sQuery(id+"F0.wireOp",EDGE,"E53"),sQuery(id+"F0.wireOp",EDGE,"E54"),sQuery(id+"F0.wireOp",EDGE,"E55"),sQuery(id+"F0.wireOp",EDGE,"E56"),sQuery(id+"F0.wireOp",EDGE,"E57"),sQuery(id+"F0.wireOp",EDGE,"E58"),sQuery(id+"F0.wireOp",EDGE,"E59"),sQuery(id+"F0.wireOp",EDGE,"E60"),sQuery(id+"F0.wireOp",EDGE,"E61"),sQuery(id+"F0.wireOp",EDGE,"E62"),sQuery(id+"F0.wireOp",EDGE,"E63"),sQuery(id+"F0.wireOp",EDGE,"E64"),sQuery(id+"F0.wireOp",EDGE,"E65"),sQuery(id+"F0.wireOp",EDGE,"E66"),sQuery(id+"F0.wireOp",EDGE,"E67"),sQuery(id+"F0.wireOp",EDGE,"E68"),sQuery(id+"F0.wireOp",EDGE,"E69"),sQuery(id+"F0.wireOp",EDGE,"E70"),sQuery(id+"F0.wireOp",EDGE,"E71"),sQuery(id+"F0.wireOp",EDGE,"E72"),sQuery(id+"F0.wireOp",EDGE,"E73"),sQuery(id+"F0.wireOp",EDGE,"E74"),sQuery(id+"F0.wireOp",EDGE,"E75"),sQuery(id+"F0.wireOp",EDGE,"E76"),sQuery(id+"F0.wireOp",EDGE,"E77"),sQuery(id+"F0.wireOp",EDGE,"E78"),sQuery(id+"F0.wireOp",EDGE,"E79"),sQuery(id+"F0.wireOp",EDGE,"E80"),sQuery(id+"F0.wireOp",EDGE,"E81"),sQuery(id+"F0.wireOp",EDGE,"E82"),sQuery(id+"F0.wireOp",EDGE,"E83"),sQuery(id+"F0.wireOp",EDGE,"E84"),sQuery(id+"F0.wireOp",EDGE,"E85"),sQuery(id+"F0.wireOp",EDGE,"E86"),sQuery(id+"F0.wireOp",EDGE,"E87"),sQuery(id+"F0.wireOp",EDGE,"E88"),sQuery(id+"F0.wireOp",EDGE,"E89"),sQuery(id+"F0.wireOp",EDGE,"E90"),sQuery(id+"F0.wireOp",EDGE,"E91"),sQuery(id+"F0.wireOp",EDGE,"E92"),sQuery(id+"F0.wireOp",EDGE,"E93"),sQuery(id+"F0.wireOp",EDGE,"E94"),sQuery(id+"F0.wireOp",EDGE,"E95"),sQuery(id+"F0.wireOp",EDGE,"E96"),sQuery(id+"F0.wireOp",EDGE,"E97"),sQuery(id+"F0.wireOp",EDGE,"E98"),sQuery(id+"F0.wireOp",EDGE,"E99"),sQuery(id+"F0.wireOp",EDGE,"E100"),sQuery(id+"F0.wireOp",EDGE,"E101"),sQuery(id+"F0.wireOp",EDGE,"E102"),sQuery(id+"F0.wireOp",EDGE,"E103"),sQuery(id+"F0.wireOp",EDGE,"E104"),sQuery(id+"F0.wireOp",EDGE,"E105"),sQuery(id+"F0.wireOp",EDGE,"E106"),sQuery(id+"F0.wireOp",EDGE,"E107"),sQuery(id+"F0.wireOp",EDGE,"E108"),sQuery(id+"F0.wireOp",EDGE,"E109"),sQuery(id+"F0.wireOp",EDGE,"E110"),sQuery(id+"F0.wireOp",EDGE,"E111"),sQuery(id+"F0.wireOp",EDGE,"E112"),sQuery(id+"F0.wireOp",EDGE,"E113"),sQuery(id+"F0.wireOp",EDGE,"E114"),sQuery(id+"F0.wireOp",EDGE,"E115"),sQuery(id+"F0.wireOp",EDGE,"E116"),sQuery(id+"F0.wireOp",EDGE,"E117"),sQuery(id+"F0.wireOp",EDGE,"E118"),sQuery(id+"F0.wireOp",EDGE,"E119"),sQuery(id+"F0.wireOp",EDGE,"E120"),sQuery(id+"F0.wireOp",EDGE,"E121"),sQuery(id+"F0.wireOp",EDGE,"E122"),sQuery(id+"F0.wireOp",EDGE,"E123"),sQuery(id+"F0.wireOp",EDGE,"E124"),sQuery(id+"F0.wireOp",EDGE,"E125"),sQuery(id+"F0.wireOp",EDGE,"E126"),sQuery(id+"F0.wireOp",EDGE,"E127"),sQuery(id+"F0.wireOp",EDGE,"E128"),sQuery(id+"F0.wireOp",EDGE,"E129"),sQuery(id+"F0.wireOp",EDGE,"E130"),sQuery(id+"F0.wireOp",EDGE,"E131"),sQuery(id+"F0.wireOp",EDGE,"E132"),sQuery(id+"F0.wireOp",EDGE,"E133"),sQuery(id+"F0.wireOp",EDGE,"E134"),sQuery(id+"F0.wireOp",EDGE,"E135"),sQuery(id+"F0.wireOp",EDGE,"E136"),sQuery(id+"F0.wireOp",EDGE,"E137"),sQuery(id+"F0.wireOp",EDGE,"E138"),sQuery(id+"F0.wireOp",EDGE,"E139"),sQuery(id+"F0.wireOp",EDGE,"E140"),sQuery(id+"F0.wireOp",EDGE,"E141"),sQuery(id+"F0.wireOp",EDGE,"E142"),sQuery(id+"F0.wireOp",EDGE,"E143"),sQuery(id+"F0.wireOp",EDGE,"E144"),sQuery(id+"F0.wireOp",EDGE,"E145"),sQuery(id+"F0.wireOp",EDGE,"E146"),sQuery(id+"F0.wireOp",EDGE,"E147"),sQuery(id+"F0.wireOp",EDGE,"E148"),sQuery(id+"F0.wireOp",EDGE,"E149"),sQuery(id+"F0.wireOp",EDGE,"E150"),sQuery(id+"F0.wireOp",EDGE,"E151"),sQuery(id+"F0.wireOp",EDGE,"E152"),sQuery(id+"F0.wireOp",EDGE,"E153"),sQuery(id+"F0.wireOp",EDGE,"E154"),sQuery(id+"F0.wireOp",EDGE,"E155"),sQuery(id+"F0.wireOp",EDGE,"E156"),sQuery(id+"F0.wireOp",EDGE,"E157"),sQuery(id+"F0.wireOp",EDGE,"E158"),sQuery(id+"F0.wireOp",EDGE,"E159"),sQuery(id+"F0.wireOp",EDGE,"E160"),sQuery(id+"F0.wireOp",EDGE,"E161"),sQuery(id+"F0.wireOp",EDGE,"E162"),sQuery(id+"F0.wireOp",EDGE,"E163"),sQuery(id+"F0.wireOp",EDGE,"E164"),sQuery(id+"F0.wireOp",EDGE,"E165"),sQuery(id+"F0.wireOp",EDGE,"E166"),sQuery(id+"F0.wireOp",EDGE,"E167"),sQuery(id+"F0.wireOp",EDGE,"E168"),sQuery(id+"F0.wireOp",EDGE,"E169"),sQuery(id+"F0.wireOp",EDGE,"E170"),sQuery(id+"F0.wireOp",EDGE,"E171"),sQuery(id+"F0.wireOp",EDGE,"E172"),sQuery(id+"F0.wireOp",EDGE,"E173"),sQuery(id+"F0.wireOp",EDGE,"E174"),sQuery(id+"F0.wireOp",EDGE,"E175"),sQuery(id+"F0.wireOp",EDGE,"E176"),sQuery(id+"F0.wireOp",EDGE,"E177"),sQuery(id+"F0.wireOp",EDGE,"E178"),sQuery(id+"F0.wireOp",EDGE,"E179"),sQuery(id+"F0.wireOp",EDGE,"E180"),sQuery(id+"F0.wireOp",EDGE,"E181"),sQuery(id+"F0.wireOp",EDGE,"E182"),sQuery(id+"F0.wireOp",EDGE,"E183"),sQuery(id+"F0.wireOp",EDGE,"E184"),sQuery(id+"F0.wireOp",EDGE,"E185"),sQuery(id+"F0.wireOp",EDGE,"E186"),sQuery(id+"F0.wireOp",EDGE,"E187"),sQuery(id+"F0.wireOp",EDGE,"E188")])],"isStart":false});
            var sketch = newSketch(context, id + "F13", { "sketchPlane" : qUnion([Q0])});
            skLineSegment(sketch, "E405", {"start": v(-179.14, 82.4) * mm, "end": v(-156.88, 82.4) * mm});
            skLineSegment(sketch, "E406", {"start": v(-156.88, 82.4) * mm, "end": v(-156.88, 83.02) * mm});
            skLineSegment(sketch, "E407", {"start": v(-156.88, 83.02) * mm, "end": v(-179.02, 83.02) * mm});
            skLineSegment(sketch, "E408", {"start": v(-179.02, 83.02) * mm, "end": v(-179.02, 83.63) * mm});
            skLineSegment(sketch, "E409", {"start": v(-179.02, 83.63) * mm, "end": v(-281.26, 83.63) * mm});
            skLineSegment(sketch, "E410", {"start": v(-281.26, 83.63) * mm, "end": v(-281.26, 81.45) * mm});
            skLineSegment(sketch, "E411", {"start": v(-281.26, 81.45) * mm, "end": v(-178.95, 81.45) * mm});
            skLineSegment(sketch, "E412", {"start": v(-178.95, 81.45) * mm, "end": v(-179.14, 82.4) * mm});
            skSolve(sketch);
        }
        {
            var Q0;
            Q0=makeQuery(id+"F13.imprint","IMPRINT",FACE,{"disambiguationData":[TD([[makeQuery(id+"F13.imprint","IMPRINT",EDGE,{"derivedFrom":sQuery(id+"F13.wireOp",EDGE,"E405")}),-1.0]])]});
            var sketch = newSketch(context, id + "F14", { "sketchPlane" : qUnion([Q0])});
            skLineSegment(sketch, "E413", {"start": v(-211.1, 99.58) * mm, "end": v(-210.84, 101.37) * mm});
            skLineSegment(sketch, "E414", {"start": v(-210.84, 101.37) * mm, "end": v(-163.36, 102.72) * mm});
            skLineSegment(sketch, "E415", {"start": v(-163.36, 102.72) * mm, "end": v(-165.18, 91.93) * mm});
            skLineSegment(sketch, "E416", {"start": v(-165.18, 91.93) * mm, "end": v(-23.02, 71.78) * mm});
            skLineSegment(sketch, "E417", {"start": v(-23.02, 71.78) * mm, "end": v(-23.32, 69.67) * mm});
            skLineSegment(sketch, "E418", {"start": v(-23.32, 69.67) * mm, "end": v(-165.18, 90.38) * mm});
            skLineSegment(sketch, "E419", {"start": v(-165.18, 90.38) * mm, "end": v(-167.11, 80.92) * mm});
            skLineSegment(sketch, "E420", {"start": v(-167.11, 80.92) * mm, "end": v(-211.86, 93.88) * mm});
            skLineSegment(sketch, "E421", {"start": v(-211.86, 93.88) * mm, "end": v(-211.86, 95.32) * mm});
            skLineSegment(sketch, "E422", {"start": v(-211.86, 95.32) * mm, "end": v(-167.08, 89.8) * mm});
            skLineSegment(sketch, "E423", {"start": v(-167.08, 89.8) * mm, "end": v(-166.96, 90.53) * mm});
            skLineSegment(sketch, "E424", {"start": v(-166.96, 90.53) * mm, "end": v(-218.76, 97.87) * mm});
            skLineSegment(sketch, "E425", {"start": v(-218.76, 97.87) * mm, "end": v(-218.76, 99.8) * mm});
            skLineSegment(sketch, "E426", {"start": v(-218.76, 99.8) * mm, "end": v(-166.45, 92.39) * mm});
            skLineSegment(sketch, "E427", {"start": v(-166.45, 92.39) * mm, "end": v(-166.23, 94.15) * mm});
            skLineSegment(sketch, "E428", {"start": v(-166.23, 94.15) * mm, "end": v(-210.2, 99.58) * mm});
            skLineSegment(sketch, "E429", {"start": v(-210.2, 99.58) * mm, "end": v(-211.1, 99.58) * mm});
            skSolve(sketch);
        }
        {
            var Q0;
            Q0 = qSketchRegion(id + "F14", true);
            extrude(context, id + "F15", {"entities" : qUnion([Q0]), "operationType" : NewBodyOperationType.REMOVE, "oppositeDirection" : true, "depth" : 2.1 * mm, "offsetDistance" : 25 * mm});
        }
        {
            var Q0;
            Q0=makeQuery(id+"F13.imprint","IMPRINT",FACE,{"disambiguationData":[TD([[makeQuery(id+"F13.imprint","IMPRINT",EDGE,{"derivedFrom":sQuery(id+"F13.wireOp",EDGE,"E405")}),-1.0]])]});
            var sketch = newSketch(context, id + "F16", { "sketchPlane" : qUnion([Q0])});
            skLineSegment(sketch, "E430", {"start": v(-217.33, 50.36) * mm, "end": v(-217.33, 56.8) * mm});
            skLineSegment(sketch, "E431", {"start": v(-217.33, 56.8) * mm, "end": v(-214.4, 56.8) * mm});
            skLineSegment(sketch, "E432", {"start": v(-214.4, 56.8) * mm, "end": v(-209.33, 58.02) * mm});
            skLineSegment(sketch, "E433", {"start": v(-209.33, 58.02) * mm, "end": v(-209.33, 61.37) * mm});
            skLineSegment(sketch, "E434", {"start": v(-209.33, 61.37) * mm, "end": v(-205.67, 64.39) * mm});
            skLineSegment(sketch, "E435", {"start": v(-205.67, 64.39) * mm, "end": v(-187.2, 64.39) * mm});
            skLineSegment(sketch, "E436", {"start": v(-187.2, 64.39) * mm, "end": v(-187.2, 65.74) * mm});
            skLineSegment(sketch, "E437", {"start": v(-187.2, 65.74) * mm, "end": v(-186.2, 65.74) * mm});
            skLineSegment(sketch, "E438", {"start": v(-186.2, 65.74) * mm, "end": v(-186.2, 66.5) * mm});
            skLineSegment(sketch, "E439", {"start": v(-186.2, 66.5) * mm, "end": v(-186.2, 66.87) * mm});
            skLineSegment(sketch, "E440", {"start": v(-186.2, 66.87) * mm, "end": v(-185.82, 67.25) * mm});
            skLineSegment(sketch, "E441", {"start": v(-185.82, 67.25) * mm, "end": v(-185.47, 67.67) * mm});
            skLineSegment(sketch, "E442", {"start": v(-185.47, 67.67) * mm, "end": v(-185.02, 68) * mm});
            skLineSegment(sketch, "E443", {"start": v(-185.02, 68) * mm, "end": v(-184.31, 68.19) * mm});
            skLineSegment(sketch, "E444", {"start": v(-184.31, 68.19) * mm, "end": v(-183.08, 68.19) * mm});
            skLineSegment(sketch, "E445", {"start": v(-183.08, 68.19) * mm, "end": v(-182.16, 66.73) * mm});
            skLineSegment(sketch, "E446", {"start": v(-182.16, 66.73) * mm, "end": v(-181.95, 65.83) * mm});
            skLineSegment(sketch, "E447", {"start": v(-181.95, 65.83) * mm, "end": v(-181.95, 64.6) * mm});
            skLineSegment(sketch, "E448", {"start": v(-181.95, 64.6) * mm, "end": v(-181.76, 61.6) * mm});
            skLineSegment(sketch, "E449", {"start": v(-181.76, 61.6) * mm, "end": v(-177.1, 61.6) * mm});
            skLineSegment(sketch, "E450", {"start": v(-177.1, 61.6) * mm, "end": v(-171.85, 53.77) * mm});
            skLineSegment(sketch, "E451", {"start": v(-171.85, 53.77) * mm, "end": v(-181.62, 48.84) * mm});
            skLineSegment(sketch, "E452", {"start": v(-181.62, 48.84) * mm, "end": v(-181.62, 46.7) * mm});
            skLineSegment(sketch, "E453", {"start": v(-181.62, 46.7) * mm, "end": v(-200.51, 46.7) * mm});
            skLineSegment(sketch, "E454", {"start": v(-200.51, 46.7) * mm, "end": v(-200.51, 44.98) * mm});
            skLineSegment(sketch, "E455", {"start": v(-200.51, 44.98) * mm, "end": v(-205.24, 44.98) * mm});
            skLineSegment(sketch, "E456", {"start": v(-205.24, 44.98) * mm, "end": v(-205.24, 46.6) * mm});
            skLineSegment(sketch, "E457", {"start": v(-205.24, 46.6) * mm, "end": v(-206.23, 46.6) * mm});
            skLineSegment(sketch, "E458", {"start": v(-206.23, 46.6) * mm, "end": v(-209.47, 49) * mm});
            skLineSegment(sketch, "E459", {"start": v(-209.47, 49) * mm, "end": v(-209.47, 50.08) * mm});
            skLineSegment(sketch, "E460", {"start": v(-209.47, 50.08) * mm, "end": v(-217.33, 50.36) * mm});
            skSolve(sketch);
        }
        {
            var Q0;
            Q0 = qSketchRegion(id + "F16", true);
            extrude(context, id + "F17", {"entities" : qUnion([Q0]), "operationType" : NewBodyOperationType.ADD, "depth" : 7.1 * mm, "offsetDistance" : 25 * mm});
        }
        {
            var Q0;
            Q0=makeQuery(id+"F17.opExtrude","CAP_FACE",FACE,{"disambiguationData":[OSD([sQuery(id+"F16.wireOp",EDGE,"E430"),sQuery(id+"F16.wireOp",EDGE,"E431"),sQuery(id+"F16.wireOp",EDGE,"E432"),sQuery(id+"F16.wireOp",EDGE,"E433"),sQuery(id+"F16.wireOp",EDGE,"E434"),sQuery(id+"F16.wireOp",EDGE,"E435"),sQuery(id+"F16.wireOp",EDGE,"E436"),sQuery(id+"F16.wireOp",EDGE,"E437"),sQuery(id+"F16.wireOp",EDGE,"E438"),sQuery(id+"F16.wireOp",EDGE,"E439"),sQuery(id+"F16.wireOp",EDGE,"E440"),sQuery(id+"F16.wireOp",EDGE,"E441"),sQuery(id+"F16.wireOp",EDGE,"E442"),sQuery(id+"F16.wireOp",EDGE,"E443"),sQuery(id+"F16.wireOp",EDGE,"E444"),sQuery(id+"F16.wireOp",EDGE,"E445"),sQuery(id+"F16.wireOp",EDGE,"E446"),sQuery(id+"F16.wireOp",EDGE,"E447"),sQuery(id+"F16.wireOp",EDGE,"E448"),sQuery(id+"F16.wireOp",EDGE,"E449"),sQuery(id+"F16.wireOp",EDGE,"E450"),sQuery(id+"F16.wireOp",EDGE,"E451"),sQuery(id+"F16.wireOp",EDGE,"E452"),sQuery(id+"F16.wireOp",EDGE,"E453"),sQuery(id+"F16.wireOp",EDGE,"E454"),sQuery(id+"F16.wireOp",EDGE,"E455"),sQuery(id+"F16.wireOp",EDGE,"E456"),sQuery(id+"F16.wireOp",EDGE,"E457"),sQuery(id+"F16.wireOp",EDGE,"E458"),sQuery(id+"F16.wireOp",EDGE,"E459"),sQuery(id+"F16.wireOp",EDGE,"E460")])],"isStart":false});
            var sketch = newSketch(context, id + "F18", { "sketchPlane" : qUnion([Q0])});
            skLineSegment(sketch, "E461", {"start": v(-188.6, 51.66) * mm, "end": v(-182.22, 51.66) * mm});
            skLineSegment(sketch, "E462", {"start": v(-182.22, 51.66) * mm, "end": v(-181.76, 59.63) * mm});
            skLineSegment(sketch, "E463", {"start": v(-181.76, 59.63) * mm, "end": v(-188.7, 59.63) * mm});
            skLineSegment(sketch, "E464", {"start": v(-188.7, 59.63) * mm, "end": v(-188.7, 56.19) * mm});
            skLineSegment(sketch, "E465", {"start": v(-188.7, 56.19) * mm, "end": v(-190.25, 56.19) * mm});
            skLineSegment(sketch, "E466", {"start": v(-190.25, 56.19) * mm, "end": v(-190.25, 56.7) * mm});
            skLineSegment(sketch, "E467", {"start": v(-190.25, 56.7) * mm, "end": v(-191.51, 56.7) * mm});
            skLineSegment(sketch, "E468", {"start": v(-191.51, 56.7) * mm, "end": v(-191.51, 58.96) * mm});
            skLineSegment(sketch, "E469", {"start": v(-191.51, 58.96) * mm, "end": v(-203.1, 58.96) * mm});
            skLineSegment(sketch, "E470", {"start": v(-203.1, 58.96) * mm, "end": v(-203.6, 58.96) * mm});
            skLineSegment(sketch, "E471", {"start": v(-203.6, 58.96) * mm, "end": v(-203.51, 58.55) * mm});
            skLineSegment(sketch, "E472", {"start": v(-203.51, 58.55) * mm, "end": v(-205.87, 58.55) * mm});
            skLineSegment(sketch, "E473", {"start": v(-205.87, 58.55) * mm, "end": v(-205.87, 52.67) * mm});
            skLineSegment(sketch, "E474", {"start": v(-205.87, 52.67) * mm, "end": v(-203.51, 52.67) * mm});
            skLineSegment(sketch, "E475", {"start": v(-203.51, 52.67) * mm, "end": v(-203.51, 52.06) * mm});
            skLineSegment(sketch, "E476", {"start": v(-203.51, 52.06) * mm, "end": v(-191.46, 52.06) * mm});
            skLineSegment(sketch, "E477", {"start": v(-191.46, 52.06) * mm, "end": v(-191.46, 54.47) * mm});
            skLineSegment(sketch, "E478", {"start": v(-191.46, 54.47) * mm, "end": v(-190.25, 54.47) * mm});
            skLineSegment(sketch, "E479", {"start": v(-190.25, 54.47) * mm, "end": v(-190.25, 54.95) * mm});
            skLineSegment(sketch, "E480", {"start": v(-190.25, 54.95) * mm, "end": v(-188.92, 55.17) * mm});
            skLineSegment(sketch, "E481", {"start": v(-188.92, 55.17) * mm, "end": v(-188.92, 51.58) * mm});
            skLineSegment(sketch, "E482", {"start": v(-188.92, 51.58) * mm, "end": v(-188.6, 51.66) * mm});
            skSolve(sketch);
        }
        {
            var Q0;
            Q0=makeQuery(id+"F18.imprint","IMPRINT",FACE,{"disambiguationData":[TD([[makeQuery(id+"F18.imprint","IMPRINT",EDGE,{"derivedFrom":sQuery(id+"F18.wireOp",EDGE,"E461")}),1.0]])]});
            extrude(context, id + "F19", {"entities" : qUnion([Q0]), "operationType" : NewBodyOperationType.ADD, "depth" : 10.1 * mm, "offsetDistance" : 25 * mm});
        }
        {
            var Q0;
            Q0=makeQuery(id+"F19.opExtrude","CAP_FACE",FACE,{"disambiguationData":[OSD([sQuery(id+"F18.wireOp",EDGE,"E461"),sQuery(id+"F18.wireOp",EDGE,"E462"),sQuery(id+"F18.wireOp",EDGE,"E463"),sQuery(id+"F18.wireOp",EDGE,"E464"),sQuery(id+"F18.wireOp",EDGE,"E465"),sQuery(id+"F18.wireOp",EDGE,"E466"),sQuery(id+"F18.wireOp",EDGE,"E467"),sQuery(id+"F18.wireOp",EDGE,"E468"),sQuery(id+"F18.wireOp",EDGE,"E469"),sQuery(id+"F18.wireOp",EDGE,"E470"),sQuery(id+"F18.wireOp",EDGE,"E471"),sQuery(id+"F18.wireOp",EDGE,"E472"),sQuery(id+"F18.wireOp",EDGE,"E473"),sQuery(id+"F18.wireOp",EDGE,"E474"),sQuery(id+"F18.wireOp",EDGE,"E475"),sQuery(id+"F18.wireOp",EDGE,"E476"),sQuery(id+"F18.wireOp",EDGE,"E477"),sQuery(id+"F18.wireOp",EDGE,"E478"),sQuery(id+"F18.wireOp",EDGE,"E479"),sQuery(id+"F18.wireOp",EDGE,"E480"),sQuery(id+"F18.wireOp",EDGE,"E481"),sQuery(id+"F18.wireOp",EDGE,"E482")])],"isStart":false});
            var sketch = newSketch(context, id + "F20", { "sketchPlane" : qUnion([Q0])});
            skLineSegment(sketch, "E483", {"start": v(-188.22, 58.82) * mm, "end": v(-182.7, 58.82) * mm});
            skLineSegment(sketch, "E484", {"start": v(-182.7, 58.82) * mm, "end": v(-182.7, 52.7) * mm});
            skLineSegment(sketch, "E485", {"start": v(-182.7, 52.7) * mm, "end": v(-188.14, 52.7) * mm});
            skLineSegment(sketch, "E486", {"start": v(-188.14, 52.7) * mm, "end": v(-188.14, 55.15) * mm});
            skLineSegment(sketch, "E487", {"start": v(-188.14, 55.15) * mm, "end": v(-183.79, 55.15) * mm});
            skLineSegment(sketch, "E488", {"start": v(-183.79, 55.15) * mm, "end": v(-183.79, 56.19) * mm});
            skLineSegment(sketch, "E489", {"start": v(-183.79, 56.19) * mm, "end": v(-188.25, 56.19) * mm});
            skLineSegment(sketch, "E490", {"start": v(-188.25, 56.19) * mm, "end": v(-188.22, 58.82) * mm});
            skLineSegment(sketch, "E491", {"start": v(-191.73, 56.7) * mm, "end": v(-196.6, 56.7) * mm});
            skLineSegment(sketch, "E492", {"start": v(-196.6, 56.7) * mm, "end": v(-196.6, 57.6) * mm});
            skLineSegment(sketch, "E493", {"start": v(-196.6, 57.6) * mm, "end": v(-201.09, 57.6) * mm});
            skLineSegment(sketch, "E494", {"start": v(-201.09, 57.6) * mm, "end": v(-201.09, 58.58) * mm});
            skLineSegment(sketch, "E495", {"start": v(-201.09, 58.58) * mm, "end": v(-205.55, 58.2) * mm});
            skLineSegment(sketch, "E496", {"start": v(-205.55, 58.2) * mm, "end": v(-205.55, 53.2) * mm});
            skLineSegment(sketch, "E497", {"start": v(-205.55, 53.2) * mm, "end": v(-201.09, 52.76) * mm});
            skLineSegment(sketch, "E498", {"start": v(-201.09, 52.76) * mm, "end": v(-201.09, 53.36) * mm});
            skLineSegment(sketch, "E499", {"start": v(-201.09, 53.36) * mm, "end": v(-196.57, 53.36) * mm});
            skLineSegment(sketch, "E500", {"start": v(-196.57, 53.36) * mm, "end": v(-196.57, 54.55) * mm});
            skLineSegment(sketch, "E501", {"start": v(-196.57, 54.55) * mm, "end": v(-192.06, 54.47) * mm});
            skLineSegment(sketch, "E502", {"start": v(-192.06, 54.47) * mm, "end": v(-191.73, 56.7) * mm});
            skSolve(sketch);
        }
        {
            var Q0;
            Q0 = qSketchRegion(id + "F20", true);
            extrude(context, id + "F21", {"entities" : qUnion([Q0]), "operationType" : NewBodyOperationType.ADD, "depth" : 5.4 * mm, "offsetDistance" : 25 * mm});
        }
        {
            var Q0;
            Q0=makeQuery(id+"F21.opExtrude","CAP_FACE",FACE,{"disambiguationData":[OSD([sQuery(id+"F20.wireOp",EDGE,"E491"),sQuery(id+"F20.wireOp",EDGE,"E492"),sQuery(id+"F20.wireOp",EDGE,"E493"),sQuery(id+"F20.wireOp",EDGE,"E494"),sQuery(id+"F20.wireOp",EDGE,"E495"),sQuery(id+"F20.wireOp",EDGE,"E496"),sQuery(id+"F20.wireOp",EDGE,"E497"),sQuery(id+"F20.wireOp",EDGE,"E498"),sQuery(id+"F20.wireOp",EDGE,"E499"),sQuery(id+"F20.wireOp",EDGE,"E500"),sQuery(id+"F20.wireOp",EDGE,"E501"),sQuery(id+"F20.wireOp",EDGE,"E502")])],"isStart":false});
            var sketch = newSketch(context, id + "F22", { "sketchPlane" : qUnion([Q0])});
            skLineSegment(sketch, "E503", {"start": v(-197.96, 55) * mm, "end": v(-198.36, 54.78) * mm});
            skLineSegment(sketch, "E504", {"start": v(-198.36, 54.78) * mm, "end": v(-199.02, 54.96) * mm});
            skLineSegment(sketch, "E505", {"start": v(-199.02, 54.96) * mm, "end": v(-199.02, 55.53) * mm});
            skLineSegment(sketch, "E506", {"start": v(-199.02, 55.53) * mm, "end": v(-199.02, 56.1) * mm});
            skLineSegment(sketch, "E507", {"start": v(-199.02, 56.1) * mm, "end": v(-198.56, 56.45) * mm});
            skLineSegment(sketch, "E508", {"start": v(-198.56, 56.45) * mm, "end": v(-198.18, 56.45) * mm});
            skLineSegment(sketch, "E509", {"start": v(-198.18, 56.45) * mm, "end": v(-197.83, 56.05) * mm});
            skLineSegment(sketch, "E510", {"start": v(-197.83, 56.05) * mm, "end": v(-197.96, 55) * mm});
            skLineSegment(sketch, "E511", {"start": v(-196.78, 55.3) * mm, "end": v(-197, 55.7) * mm});
            skLineSegment(sketch, "E512", {"start": v(-197, 55.7) * mm, "end": v(-196.74, 56.1) * mm});
            skLineSegment(sketch, "E513", {"start": v(-196.74, 56.1) * mm, "end": v(-196.39, 56.1) * mm});
            skLineSegment(sketch, "E514", {"start": v(-196.39, 56.1) * mm, "end": v(-196.04, 55.79) * mm});
            skLineSegment(sketch, "E515", {"start": v(-196.04, 55.79) * mm, "end": v(-196.04, 55.48) * mm});
            skLineSegment(sketch, "E516", {"start": v(-196.04, 55.48) * mm, "end": v(-196.3, 55.18) * mm});
            skLineSegment(sketch, "E517", {"start": v(-196.3, 55.18) * mm, "end": v(-196.78, 55.3) * mm});
            skLineSegment(sketch, "E518", {"start": v(-193.71, 55) * mm, "end": v(-193.71, 55.53) * mm});
            skLineSegment(sketch, "E519", {"start": v(-193.71, 55.53) * mm, "end": v(-193.71, 56) * mm});
            skLineSegment(sketch, "E520", {"start": v(-193.71, 56) * mm, "end": v(-192.97, 56) * mm});
            skLineSegment(sketch, "E521", {"start": v(-192.97, 56) * mm, "end": v(-192.97, 55.3) * mm});
            skLineSegment(sketch, "E522", {"start": v(-192.97, 55.3) * mm, "end": v(-193.19, 55) * mm});
            skLineSegment(sketch, "E523", {"start": v(-193.19, 55) * mm, "end": v(-193.5, 55) * mm});
            skLineSegment(sketch, "E524", {"start": v(-193.5, 55) * mm, "end": v(-193.71, 55) * mm});
            skLineSegment(sketch, "E525", {"start": v(-204.71, 57.1) * mm, "end": v(-202.08, 57.1) * mm});
            skLineSegment(sketch, "E526", {"start": v(-202.08, 57.1) * mm, "end": v(-202.08, 54.39) * mm});
            skLineSegment(sketch, "E527", {"start": v(-202.08, 54.39) * mm, "end": v(-204.76, 54.39) * mm});
            skLineSegment(sketch, "E528", {"start": v(-204.76, 54.39) * mm, "end": v(-204.71, 57.1) * mm});
            skLineSegment(sketch, "E529", {"start": v(-188.1, 56.53) * mm, "end": v(-186.6, 58.37) * mm});
            skLineSegment(sketch, "E530", {"start": v(-186.6, 58.37) * mm, "end": v(-183.81, 58.37) * mm});
            skLineSegment(sketch, "E531", {"start": v(-183.81, 58.37) * mm, "end": v(-182.91, 56.7) * mm});
            skLineSegment(sketch, "E532", {"start": v(-182.91, 56.7) * mm, "end": v(-183.29, 53.8) * mm});
            skLineSegment(sketch, "E533", {"start": v(-183.29, 53.8) * mm, "end": v(-187.14, 53.1) * mm});
            skLineSegment(sketch, "E534", {"start": v(-187.14, 53.1) * mm, "end": v(-187.8, 55) * mm});
            skLineSegment(sketch, "E535", {"start": v(-187.8, 55) * mm, "end": v(-183.55, 55) * mm});
            skLineSegment(sketch, "E536", {"start": v(-183.55, 55) * mm, "end": v(-183.55, 56.53) * mm});
            skLineSegment(sketch, "E537", {"start": v(-183.55, 56.53) * mm, "end": v(-188.1, 56.53) * mm});
            skSolve(sketch);
        }
        {
            var Q0;
            Q0 = qSketchRegion(id + "F22", true);
            extrude(context, id + "F23", {"entities" : qUnion([Q0]), "operationType" : NewBodyOperationType.ADD, "depth" : 13.8 * mm, "offsetDistance" : 25 * mm});
        }
        {
            var Q0;
            Q0=makeQuery(id+"F23.opExtrude","CAP_FACE",FACE,{"disambiguationData":[OSD([sQuery(id+"F22.wireOp",EDGE,"E525"),sQuery(id+"F22.wireOp",EDGE,"E526"),sQuery(id+"F22.wireOp",EDGE,"E527"),sQuery(id+"F22.wireOp",EDGE,"E528")])],"isStart":false});
            var sketch = newSketch(context, id + "F24", { "sketchPlane" : qUnion([Q0])});
            skLineSegment(sketch, "E538.bottom", {"start": v(-182.14, 53.07) * mm, "end": v(-208.38, 53.07) * mm});
            skLineSegment(sketch, "E538.top", {"start": v(-182.14, 58.4) * mm, "end": v(-208.38, 58.4) * mm});
            skLineSegment(sketch, "E538.left", {"start": v(-182.14, 53.07) * mm, "end": v(-182.14, 58.4) * mm});
            skLineSegment(sketch, "E538.right", {"start": v(-208.38, 53.07) * mm, "end": v(-208.38, 58.4) * mm});
            skPoint(sketch, "E538.middle", {"position": v(-195.26, 55.73) * mm});
            skSolve(sketch);
        }
        {
            var Q0;
            Q0 = qSketchRegion(id + "F24", true);
            extrude(context, id + "F25", {"entities" : qUnion([Q0]), "operationType" : NewBodyOperationType.ADD, "depth" : 2 * mm, "offsetDistance" : 25 * mm});
        }
        {
            var Q0;
            Q0=makeQuery(id+"F25.opExtrude","CAP_FACE",FACE,{"disambiguationData":[OSD([sQuery(id+"F24.wireOp",EDGE,"E538.bottom"),sQuery(id+"F24.wireOp",EDGE,"E538.top"),sQuery(id+"F24.wireOp",EDGE,"E538.left"),sQuery(id+"F24.wireOp",EDGE,"E538.right")])],"isStart":false});
            var sketch = newSketch(context, id + "F26", { "sketchPlane" : qUnion([Q0])});
            skCircle(sketch, "E539", {"center": v(-204.45, 56.64) * mm, "radius": 1.5 * mm});
            skSolve(sketch);
        }
        {
            var Q0;
            Q0 = qSketchRegion(id + "F26", true);
            extrude(context, id + "F27", {"entities" : qUnion([Q0]), "operationType" : NewBodyOperationType.ADD, "depth" : 17 * mm, "offsetDistance" : 25 * mm});
        }
        {
            var Q0;
            Q0=makeQuery(id+"F13.imprint","IMPRINT",FACE,{"disambiguationData":[TD([[makeQuery(id+"F13.imprint","IMPRINT",EDGE,{"derivedFrom":sQuery(id+"F13.wireOp",EDGE,"E405")}),-1.0]])]});
            var sketch = newSketch(context, id + "F28", { "sketchPlane" : qUnion([Q0])});
            skLineSegment(sketch, "E540", {"start": v(-21.98, 84.86) * mm, "end": v(-217.97, 111.53) * mm});
            skLineSegment(sketch, "E541", {"start": v(-217.97, 111.53) * mm, "end": v(-217.63, 114.03) * mm});
            skLineSegment(sketch, "E542", {"start": v(-217.63, 114.03) * mm, "end": v(-20.33, 88.03) * mm});
            skLineSegment(sketch, "E543", {"start": v(-20.33, 88.03) * mm, "end": v(-23.14, 54.65) * mm});
            skLineSegment(sketch, "E544", {"start": v(-23.14, 54.65) * mm, "end": v(-222.24, 84.82) * mm});
            skLineSegment(sketch, "E545", {"start": v(-222.24, 84.82) * mm, "end": v(-221.8, 88.03) * mm});
            skLineSegment(sketch, "E546", {"start": v(-221.8, 88.03) * mm, "end": v(-24.04, 58.46) * mm});
            skLineSegment(sketch, "E547", {"start": v(-24.04, 58.46) * mm, "end": v(-21.98, 84.86) * mm});
            skSolve(sketch);
        }
        {
            var Q0;
            Q0 = qSketchRegion(id + "F28", true);
            extrude(context, id + "F29", {"entities" : qUnion([Q0]), "operationType" : NewBodyOperationType.REMOVE, "oppositeDirection" : true, "depth" : 2.1 * mm, "offsetDistance" : 25 * mm});
        }
        {
            var Q0;
            Q0=makeQuery(id+"F13.imprint","IMPRINT",FACE,{"disambiguationData":[TD([[makeQuery(id+"F13.imprint","IMPRINT",EDGE,{"derivedFrom":sQuery(id+"F13.wireOp",EDGE,"E405")}),-1.0]])]});
            var sketch = newSketch(context, id + "F30", { "sketchPlane" : qUnion([Q0])});
            skLineSegment(sketch, "E548", {"start": v(-281.34, 81.35) * mm, "end": v(-281.34, 83.65) * mm});
            skLineSegment(sketch, "E549", {"start": v(-281.34, 83.65) * mm, "end": v(-179.67, 83.65) * mm});
            skLineSegment(sketch, "E550", {"start": v(-179.67, 83.65) * mm, "end": v(-179.67, 81.32) * mm});
            skLineSegment(sketch, "E551", {"start": v(-179.67, 81.32) * mm, "end": v(-281.34, 81.35) * mm});
            skSolve(sketch);
        }
        {
            var Q0;
            Q0 = qSketchRegion(id + "F30", true);
            extrude(context, id + "F31", {"entities" : qUnion([Q0]), "operationType" : NewBodyOperationType.REMOVE, "oppositeDirection" : true, "depth" : 2.1 * mm, "offsetDistance" : 25 * mm});
        }
    });
